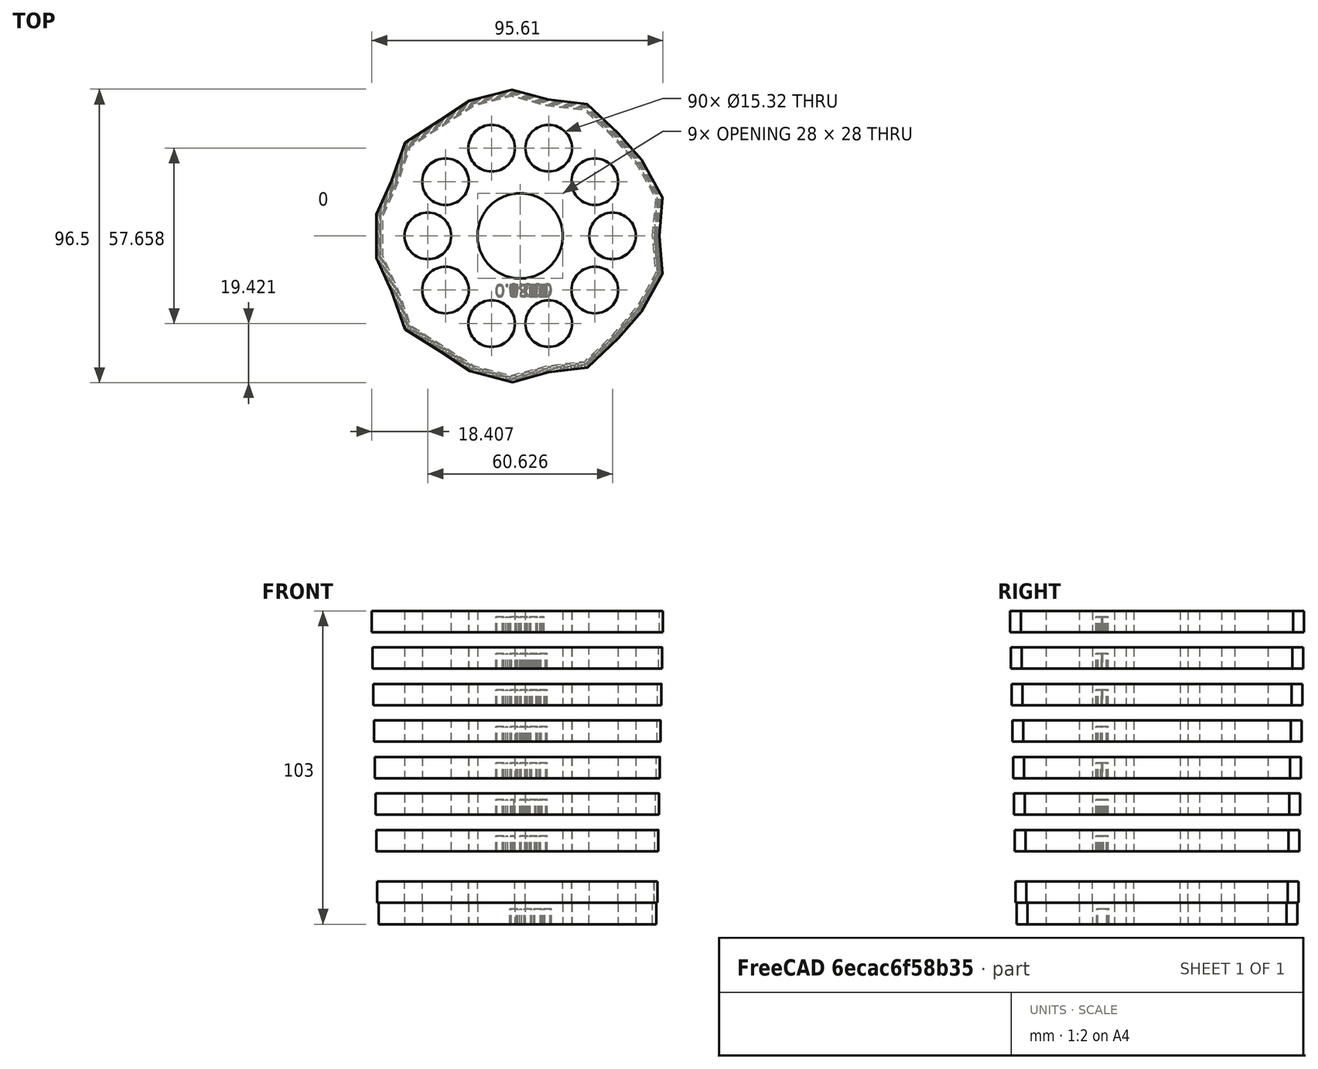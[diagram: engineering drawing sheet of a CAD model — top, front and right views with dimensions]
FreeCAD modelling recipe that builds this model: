
FCSTD DOCUMENT  (FreeCAD 1.0R39109 (Git))
Label: All gears
License: Creative Commons Attribution 4.0
LicenseURL: https://creativecommons.org/licenses/by/4.0/
objects: Sketcher::SketchObject×27, PartDesign::Pocket×17, PartDesign::Pad×9, PartDesign::PolarPattern×9, PartDesign::Body×9, Part::Part2DObjectPython×8
note: 167 computed .brp shape members not serialized (recipe doc carries the construction recipe); baked Part::Feature solids carry a one-line shape summary decoded from their .brp

FEATURE [Part::Part2DObjectPython] ShapeString  # Draft 2D object (typed FeaturePython)
  FontFile = <userpath>/Documents/DV_Projects/8_Cycloidal_gearbox_paper/0_Modelling_FILES/V 0_000/OpenSans-Regular.ttf
  Fuse = false
  Justification = 6
  JustificationReference = 0
  KeepLeftMargin = false
  MakeFace = true
  ObliqueAngle = 0
  Placement = pos=(-141.05,-92.68,0) rot=(-1,0,0;1.5708rad)
  ScaleToSize = true
  Size = 4
  String = 0
  Tracking = 0
FEATURE [Sketcher::SketchObject] Sketch  label="IF E Change001"
  ArcFitTolerance = 1e-06
  AttachmentSupport = -> [XZ_Plane]
  FullyConstrained = false
  MakeInternals = false
  MapMode = 5
  Placement = pos=(0,0,0) rot=(1,0,0;1.5708rad)
  sketch-geometry (7):
    g0: Circle CenterX=0 CenterY=0 CenterZ=0 NormalX=0 NormalY=0 NormalZ=1 AngleXU=0 Radius=14
    g1: Circle [constr] CenterX=0 CenterY=0 CenterZ=0 NormalX=0 NormalY=0 NormalZ=1 AngleXU=0 Radius=46.6255
    g2: LineSegment [constr] StartX=14 StartY=0 StartZ=0 EndX=46.6255 EndY=0 EndZ=0
    g3: GeomPoint [constr] X=30.3128 Y=0 Z=0
    g4: Circle [constr] CenterX=0 CenterY=0 CenterZ=0 NormalX=0 NormalY=0 NormalZ=1 AngleXU=0 Radius=30.3128
    g5: Circle CenterX=-30.3128 CenterY=0 CenterZ=0 NormalX=0 NormalY=0 NormalZ=1 AngleXU=0 Radius=7.66
    g6: Circle [constr] CenterX=-31.4728 CenterY=0 CenterZ=0 NormalX=0 NormalY=0 NormalZ=1 AngleXU=0 Radius=6.5
  constraints (20):
    c: Diameter(g0) = 28  'Dia Bearing'
    c: Coincident(g0,g-1)
    c: Coincident(g1,g0)
    c: PointOnObject(g2,g0)
    c: PointOnObject(g2,g1)
    c: PointOnObject(g2,g-1)
    c: PointOnObject(g2,g-1)
    c: Symmetric(g2,g2,g3)
    c: Coincident(g4,g0)
    c: PointOnObject(g3,g4)
    c: Diameter(g5) = 15.32  'DPinOut+E+2dc'
    c: Diameter(g1) = 93.251
    c: Block(g1)
    c: Block(g4)
    c: PointOnObject(g6,g-1)
    c: Diameter(g6) = 13
    c: Tangent(g5,g6)
    c: PointOnObject(g5,g4)
    c: DistanceX(g6,g5) = 1.16
    c: Diameter(g4) = 60.6255
FEATURE [Sketcher::SketchObject] USE_Macro_v6_gear_profile001
  ArcFitTolerance = 1e-06
  AttachmentSupport = -> [XZ_Plane]
  FullyConstrained = false
  MakeInternals = false
  MapMode = 5
  Placement = pos=(0,0,0) rot=(1,0,0;1.5708rad)
  sketch-geometry (1):
    g0: BSplineCurve PolesCount=3241 KnotsCount=3242 Degree=3 IsPeriodic=1
FEATURE [PartDesign::Pad] Pad  label="HERE"
  Direction = (0,-1,2e-16)
  Length = 7
  Length2 = 10
  Placement = pos=(0,0,0) rot=(1,0,0;1.5708rad)
  Profile = -> USE_Macro_v6_gear_profile001
  ReferenceAxis = -> USE_Macro_v6_gear_profile001 [N_Axis]
  Refine = true
  Suppressed = false
  Type = 0
FEATURE [PartDesign::Pocket] Pocket
  BaseFeature = -> Pad
  Direction = (0,1,-2e-16)
  Length = 5
  Length2 = 5
  Midplane = true
  Placement = pos=(0,0,0) rot=(1,0,0;1.5708rad)
  Profile = -> Sketch
  ReferenceAxis = -> Sketch [N_Axis]
  Refine = true
  Suppressed = false
  Type = 1
FEATURE [PartDesign::PolarPattern] PolarPattern
  Angle = 360
  Axis = -> Sketch [N_Axis]
  BaseFeature = -> Pocket
  Mode = 0
  Occurrences = 10
  Offset = 120
  Originals = -> [Pocket]
  Placement = pos=(0,0,0) rot=(1,0,0;1.5708rad)
  Refine = true
  Suppressed = false
  TransformMode = 0
FEATURE [Sketcher::SketchObject] Sketch037
  ArcFitTolerance = 1e-06
  AttachmentSupport = -> [PolarPattern]
  FullyConstrained = false
  MakeInternals = false
  MapMode = 5
  Placement = pos=(0,-7,0) rot=(1,0,0;1.5708rad)
  sketch-geometry (108):
    g0: BSplineCurve PolesCount=3 KnotsCount=2 Degree=2 IsPeriodic=0
    g1: BSplineCurve PolesCount=3 KnotsCount=2 Degree=2 IsPeriodic=0
    g2: BSplineCurve PolesCount=3 KnotsCount=2 Degree=2 IsPeriodic=0
    g3: BSplineCurve PolesCount=3 KnotsCount=2 Degree=2 IsPeriodic=0
    g4: BSplineCurve PolesCount=3 KnotsCount=2 Degree=2 IsPeriodic=0
    g5: BSplineCurve PolesCount=3 KnotsCount=2 Degree=2 IsPeriodic=0
    g6: BSplineCurve PolesCount=3 KnotsCount=2 Degree=2 IsPeriodic=0
    g7: BSplineCurve PolesCount=3 KnotsCount=2 Degree=2 IsPeriodic=0
    g8: BSplineCurve PolesCount=3 KnotsCount=2 Degree=2 IsPeriodic=0
    g9: BSplineCurve PolesCount=3 KnotsCount=2 Degree=2 IsPeriodic=0
    g10: BSplineCurve PolesCount=3 KnotsCount=2 Degree=2 IsPeriodic=0
    g11: BSplineCurve PolesCount=3 KnotsCount=2 Degree=2 IsPeriodic=0
    g12: BSplineCurve PolesCount=3 KnotsCount=2 Degree=2 IsPeriodic=0
    g13: BSplineCurve PolesCount=3 KnotsCount=2 Degree=2 IsPeriodic=0
    g14: BSplineCurve PolesCount=3 KnotsCount=2 Degree=2 IsPeriodic=0
    g15: BSplineCurve PolesCount=3 KnotsCount=2 Degree=2 IsPeriodic=0
    g16: BSplineCurve PolesCount=3 KnotsCount=2 Degree=2 IsPeriodic=0
    g17: BSplineCurve PolesCount=3 KnotsCount=2 Degree=2 IsPeriodic=0
    g18: BSplineCurve PolesCount=3 KnotsCount=2 Degree=2 IsPeriodic=0
    g19: BSplineCurve PolesCount=3 KnotsCount=2 Degree=2 IsPeriodic=0
    g20: BSplineCurve PolesCount=3 KnotsCount=2 Degree=2 IsPeriodic=0
    g21: BSplineCurve PolesCount=3 KnotsCount=2 Degree=2 IsPeriodic=0
    g22: BSplineCurve PolesCount=3 KnotsCount=2 Degree=2 IsPeriodic=0
    g23: BSplineCurve PolesCount=3 KnotsCount=2 Degree=2 IsPeriodic=0
    g24: BSplineCurve PolesCount=3 KnotsCount=2 Degree=2 IsPeriodic=0
    g25: BSplineCurve PolesCount=3 KnotsCount=2 Degree=2 IsPeriodic=0
    g26: BSplineCurve PolesCount=3 KnotsCount=2 Degree=2 IsPeriodic=0
    g27: BSplineCurve PolesCount=3 KnotsCount=2 Degree=2 IsPeriodic=0
    g28: BSplineCurve PolesCount=3 KnotsCount=2 Degree=2 IsPeriodic=0
    g29: BSplineCurve PolesCount=3 KnotsCount=2 Degree=2 IsPeriodic=0
    g30: BSplineCurve PolesCount=3 KnotsCount=2 Degree=2 IsPeriodic=0
    g31: BSplineCurve PolesCount=3 KnotsCount=2 Degree=2 IsPeriodic=0
    g32: BSplineCurve PolesCount=3 KnotsCount=2 Degree=2 IsPeriodic=0
    g33: BSplineCurve PolesCount=3 KnotsCount=2 Degree=2 IsPeriodic=0
    g34: BSplineCurve PolesCount=3 KnotsCount=2 Degree=2 IsPeriodic=0
    g35: BSplineCurve PolesCount=3 KnotsCount=2 Degree=2 IsPeriodic=0
    g36: BSplineCurve PolesCount=3 KnotsCount=2 Degree=2 IsPeriodic=0
    g37: BSplineCurve PolesCount=3 KnotsCount=2 Degree=2 IsPeriodic=0
    g38: BSplineCurve PolesCount=3 KnotsCount=2 Degree=2 IsPeriodic=0
    g39: BSplineCurve PolesCount=3 KnotsCount=2 Degree=2 IsPeriodic=0
    g40: BSplineCurve PolesCount=3 KnotsCount=2 Degree=2 IsPeriodic=0
    g41: BSplineCurve PolesCount=3 KnotsCount=2 Degree=2 IsPeriodic=0
    g42: BSplineCurve PolesCount=3 KnotsCount=2 Degree=2 IsPeriodic=0
    g43: BSplineCurve PolesCount=3 KnotsCount=2 Degree=2 IsPeriodic=0
    g44: BSplineCurve PolesCount=3 KnotsCount=2 Degree=2 IsPeriodic=0
    g45: BSplineCurve PolesCount=3 KnotsCount=2 Degree=2 IsPeriodic=0
    g46: BSplineCurve PolesCount=3 KnotsCount=2 Degree=2 IsPeriodic=0
    g47: BSplineCurve PolesCount=3 KnotsCount=2 Degree=2 IsPeriodic=0
    g48: BSplineCurve PolesCount=3 KnotsCount=2 Degree=2 IsPeriodic=0
    g49: BSplineCurve PolesCount=3 KnotsCount=2 Degree=2 IsPeriodic=0
    g50: BSplineCurve PolesCount=3 KnotsCount=2 Degree=2 IsPeriodic=0
    g51: BSplineCurve PolesCount=3 KnotsCount=2 Degree=2 IsPeriodic=0
    g52: BSplineCurve PolesCount=3 KnotsCount=2 Degree=2 IsPeriodic=0
    g53: BSplineCurve PolesCount=3 KnotsCount=2 Degree=2 IsPeriodic=0
    g54: BSplineCurve PolesCount=3 KnotsCount=2 Degree=2 IsPeriodic=0
    g55: BSplineCurve PolesCount=3 KnotsCount=2 Degree=2 IsPeriodic=0
    g56: BSplineCurve PolesCount=3 KnotsCount=2 Degree=2 IsPeriodic=0
    g57: BSplineCurve PolesCount=3 KnotsCount=2 Degree=2 IsPeriodic=0
    g58: BSplineCurve PolesCount=3 KnotsCount=2 Degree=2 IsPeriodic=0
    g59: BSplineCurve PolesCount=3 KnotsCount=2 Degree=2 IsPeriodic=0
    g60: BSplineCurve PolesCount=3 KnotsCount=2 Degree=2 IsPeriodic=0
    g61: BSplineCurve PolesCount=3 KnotsCount=2 Degree=2 IsPeriodic=0
    g62: BSplineCurve PolesCount=3 KnotsCount=2 Degree=2 IsPeriodic=0
    g63: BSplineCurve PolesCount=3 KnotsCount=2 Degree=2 IsPeriodic=0
    g64: BSplineCurve PolesCount=3 KnotsCount=2 Degree=2 IsPeriodic=0
    g65: BSplineCurve PolesCount=3 KnotsCount=2 Degree=2 IsPeriodic=0
    g66: BSplineCurve PolesCount=3 KnotsCount=2 Degree=2 IsPeriodic=0
    g67: BSplineCurve PolesCount=3 KnotsCount=2 Degree=2 IsPeriodic=0
    g68: BSplineCurve PolesCount=3 KnotsCount=2 Degree=2 IsPeriodic=0
    g69: BSplineCurve PolesCount=3 KnotsCount=2 Degree=2 IsPeriodic=0
    g70: BSplineCurve PolesCount=3 KnotsCount=2 Degree=2 IsPeriodic=0
    g71: BSplineCurve PolesCount=3 KnotsCount=2 Degree=2 IsPeriodic=0
    g72: BSplineCurve PolesCount=3 KnotsCount=2 Degree=2 IsPeriodic=0
    g73: BSplineCurve PolesCount=3 KnotsCount=2 Degree=2 IsPeriodic=0
    g74: BSplineCurve PolesCount=3 KnotsCount=2 Degree=2 IsPeriodic=0
    g75: BSplineCurve PolesCount=3 KnotsCount=2 Degree=2 IsPeriodic=0
    g76: BSplineCurve PolesCount=3 KnotsCount=2 Degree=2 IsPeriodic=0
    g77: BSplineCurve PolesCount=3 KnotsCount=2 Degree=2 IsPeriodic=0
    g78: BSplineCurve PolesCount=3 KnotsCount=2 Degree=2 IsPeriodic=0
    g79: BSplineCurve PolesCount=3 KnotsCount=2 Degree=2 IsPeriodic=0
    g80: BSplineCurve PolesCount=3 KnotsCount=2 Degree=2 IsPeriodic=0
    g81: BSplineCurve PolesCount=3 KnotsCount=2 Degree=2 IsPeriodic=0
    g82: BSplineCurve PolesCount=3 KnotsCount=2 Degree=2 IsPeriodic=0
    g83: BSplineCurve PolesCount=3 KnotsCount=2 Degree=2 IsPeriodic=0
    g84: BSplineCurve PolesCount=3 KnotsCount=2 Degree=2 IsPeriodic=0
    g85: BSplineCurve PolesCount=3 KnotsCount=2 Degree=2 IsPeriodic=0
    g86: BSplineCurve PolesCount=3 KnotsCount=2 Degree=2 IsPeriodic=0
    g87: BSplineCurve PolesCount=3 KnotsCount=2 Degree=2 IsPeriodic=0
    g88: BSplineCurve PolesCount=3 KnotsCount=2 Degree=2 IsPeriodic=0
    g89: BSplineCurve PolesCount=3 KnotsCount=2 Degree=2 IsPeriodic=0
    g90: BSplineCurve PolesCount=3 KnotsCount=2 Degree=2 IsPeriodic=0
    g91: BSplineCurve PolesCount=3 KnotsCount=2 Degree=2 IsPeriodic=0
    g92: BSplineCurve PolesCount=3 KnotsCount=2 Degree=2 IsPeriodic=0
    g93: BSplineCurve PolesCount=3 KnotsCount=2 Degree=2 IsPeriodic=0
    g94: BSplineCurve PolesCount=3 KnotsCount=2 Degree=2 IsPeriodic=0
    g95: BSplineCurve PolesCount=3 KnotsCount=2 Degree=2 IsPeriodic=0
    g96: BSplineCurve PolesCount=3 KnotsCount=2 Degree=2 IsPeriodic=0
    g97: BSplineCurve PolesCount=3 KnotsCount=2 Degree=2 IsPeriodic=0
    g98: BSplineCurve PolesCount=3 KnotsCount=2 Degree=2 IsPeriodic=0
    g99: BSplineCurve PolesCount=3 KnotsCount=2 Degree=2 IsPeriodic=0
    g100: BSplineCurve PolesCount=3 KnotsCount=2 Degree=2 IsPeriodic=0
    g101: BSplineCurve PolesCount=3 KnotsCount=2 Degree=2 IsPeriodic=0
    g102: BSplineCurve PolesCount=3 KnotsCount=2 Degree=2 IsPeriodic=0
    g103: BSplineCurve PolesCount=3 KnotsCount=2 Degree=2 IsPeriodic=0
    g104: BSplineCurve PolesCount=3 KnotsCount=2 Degree=2 IsPeriodic=0
    g105: BSplineCurve PolesCount=3 KnotsCount=2 Degree=2 IsPeriodic=0
    g106: BSplineCurve PolesCount=3 KnotsCount=2 Degree=2 IsPeriodic=0
    g107: BSplineCurve PolesCount=3 KnotsCount=2 Degree=2 IsPeriodic=0
  constraints (108):
    c: Coincident(g0,g1)
    c: Coincident(g1,g2)
    c: Coincident(g2,g3)
    c: Coincident(g3,g4)
    c: Coincident(g4,g5)
    c: Coincident(g5,g6)
    c: Coincident(g6,g7)
    c: Coincident(g7,g8)
    c: Coincident(g8,g9)
    c: Coincident(g9,g10)
    c: Coincident(g10,g11)
    c: Coincident(g11,g12)
    c: Coincident(g12,g0)
    c: Coincident(g13,g14)
    c: Coincident(g14,g15)
    c: Coincident(g15,g16)
    c: Coincident(g16,g17)
    c: Coincident(g17,g18)
    c: Coincident(g18,g19)
    c: Coincident(g19,g20)
    c: Coincident(g20,g21)
    c: Coincident(g21,g22)
    c: Coincident(g22,g23)
    c: Coincident(g23,g24)
    c: Coincident(g24,g13)
    c: Coincident(g25,g26)
    c: Coincident(g26,g27)
    c: Coincident(g27,g28)
    c: Coincident(g28,g29)
    c: Coincident(g29,g30)
    c: Coincident(g30,g31)
    c: Coincident(g31,g32)
    c: Coincident(g32,g25)
    c: Coincident(g33,g34)
    c: Coincident(g34,g35)
    c: Coincident(g35,g36)
    c: Coincident(g36,g37)
    c: Coincident(g37,g38)
    c: Coincident(g38,g39)
    c: Coincident(g39,g40)
    c: Coincident(g40,g41)
    c: Coincident(g41,g42)
    c: Coincident(g42,g43)
    c: Coincident(g43,g44)
    c: Coincident(g44,g45)
    c: Coincident(g45,g33)
    c: Coincident(g46,g47)
    c: Coincident(g47,g48)
    c: Coincident(g48,g49)
    c: Coincident(g49,g50)
    c: Coincident(g50,g51)
    c: Coincident(g51,g52)
    c: Coincident(g52,g53)
    c: Coincident(g53,g54)
    c: Coincident(g54,g55)
    c: Coincident(g55,g56)
    c: Coincident(g56,g57)
    c: Coincident(g57,g46)
    c: Coincident(g58,g59)
    c: Coincident(g59,g60)
    c: Coincident(g60,g61)
    c: Coincident(g61,g62)
    c: Coincident(g62,g63)
    c: Coincident(g63,g64)
    c: Coincident(g64,g65)
    c: Coincident(g65,g66)
    c: Coincident(g66,g67)
    c: Coincident(g67,g68)
    c: Coincident(g68,g69)
    c: Coincident(g69,g70)
    c: Coincident(g70,g58)
    c: Coincident(g71,g72)
    c: Coincident(g72,g73)
    c: Coincident(g73,g74)
    c: Coincident(g74,g75)
    c: Coincident(g75,g76)
    c: Coincident(g76,g77)
    c: Coincident(g77,g78)
    c: Coincident(g78,g79)
    c: Coincident(g79,g80)
    c: Coincident(g80,g81)
    c: Coincident(g81,g82)
    c: Coincident(g82,g71)
    c: Coincident(g83,g84)
    c: Coincident(g84,g85)
    c: Coincident(g85,g86)
    c: Coincident(g86,g87)
    c: Coincident(g87,g88)
    c: Coincident(g88,g89)
    c: Coincident(g89,g90)
    c: Coincident(g90,g91)
    c: Coincident(g91,g92)
    c: Coincident(g92,g93)
    c: Coincident(g93,g94)
    c: Coincident(g94,g95)
    c: Coincident(g95,g83)
    c: Coincident(g96,g97)
    c: Coincident(g97,g98)
    c: Coincident(g98,g99)
    c: Coincident(g99,g100)
    c: Coincident(g100,g101)
    c: Coincident(g101,g102)
    c: Coincident(g102,g103)
    c: Coincident(g103,g104)
    c: Coincident(g104,g105)
    c: Coincident(g105,g106)
    c: Coincident(g106,g107)
    c: Coincident(g107,g96)
FEATURE [PartDesign::Pocket] Pocket017
  BaseFeature = -> PolarPattern
  Direction = (0,1,-2e-16)
  Length = 5
  Length2 = 5
  Placement = pos=(0,0,0) rot=(1,0,0;1.5708rad)
  Profile = -> Sketch037
  ReferenceAxis = -> Sketch037 [N_Axis]
  Refine = true
  Suppressed = false
  Type = 0
FEATURE [PartDesign::Body] Body  label="Gear_0_0000"
  AllowCompound = false
  Group = -> [Sketch,USE_Macro_v6_gear_profile001,Pad,Pocket,PolarPattern,ShapeString,Sketch037,Pocket017]
  Origin = -> Origin
  Placement = pos=(0,-3,0) rot=(1,0,0;1.5708rad)
  Tip = -> Pocket017
FEATURE [Sketcher::SketchObject] Sketch038  label="IF E Change002"
  ArcFitTolerance = 1e-06
  AttachmentSupport = -> [XZ_Plane001]
  FullyConstrained = false
  MakeInternals = false
  MapMode = 5
  Placement = pos=(0,0,0) rot=(1,0,0;1.5708rad)
  sketch-geometry (7):
    g0: Circle CenterX=0 CenterY=0 CenterZ=0 NormalX=0 NormalY=0 NormalZ=1 AngleXU=0 Radius=14
    g1: Circle [constr] CenterX=0 CenterY=0 CenterZ=0 NormalX=0 NormalY=0 NormalZ=1 AngleXU=0 Radius=46.6255
    g2: LineSegment [constr] StartX=14 StartY=0 StartZ=0 EndX=46.6255 EndY=0 EndZ=0
    g3: GeomPoint [constr] X=30.3128 Y=0 Z=0
    g4: Circle [constr] CenterX=0 CenterY=0 CenterZ=0 NormalX=0 NormalY=0 NormalZ=1 AngleXU=0 Radius=30.3128
    g5: Circle CenterX=-30.3128 CenterY=0 CenterZ=0 NormalX=0 NormalY=0 NormalZ=1 AngleXU=0 Radius=7.66
    g6: Circle [constr] CenterX=-31.4728 CenterY=0 CenterZ=0 NormalX=0 NormalY=0 NormalZ=1 AngleXU=0 Radius=6.5
  constraints (20):
    c: Diameter(g0) = 28  'Dia Bearing'
    c: Coincident(g0,g-1)
    c: Coincident(g1,g0)
    c: PointOnObject(g2,g0)
    c: PointOnObject(g2,g1)
    c: PointOnObject(g2,g-1)
    c: PointOnObject(g2,g-1)
    c: Symmetric(g2,g2,g3)
    c: Coincident(g4,g0)
    c: PointOnObject(g3,g4)
    c: Diameter(g5) = 15.32  'DPinOut+E+2dc'
    c: Diameter(g1) = 93.251
    c: Block(g1)
    c: Block(g4)
    c: PointOnObject(g6,g-1)
    c: Diameter(g6) = 13
    c: Tangent(g5,g6)
    c: PointOnObject(g5,g4)
    c: DistanceX(g6,g5) = 1.16
    c: Diameter(g4) = 60.6255
FEATURE [Sketcher::SketchObject] USE_Macro_v6_gear_profile  label="USE_Macro_v6_gear_profile_N_6"
  ArcFitTolerance = 1e-06
  AttachmentSupport = -> [XZ_Plane001]
  FullyConstrained = false
  MakeInternals = false
  MapMode = 5
  Placement = pos=(0,0,0) rot=(1,0,0;1.5708rad)
  sketch-geometry (1):
    g0: BSplineCurve PolesCount=1801 KnotsCount=1801 Degree=3 IsPeriodic=1
FEATURE [Sketcher::SketchObject] USE_Macro_v6_gear_profile002
  ArcFitTolerance = 1e-06
  AttachmentSupport = -> [XZ_Plane001]
  FullyConstrained = false
  MakeInternals = false
  MapMode = 5
  Placement = pos=(0,0,0) rot=(1,0,0;1.5708rad)
  sketch-geometry (1):
    g0: BSplineCurve PolesCount=3241 KnotsCount=3241 Degree=3 IsPeriodic=1
FEATURE [PartDesign::Pad] Pad001
  Direction = (0,-1,2e-16)
  Length = 7
  Length2 = 10
  Placement = pos=(0,0,0) rot=(1,0,0;1.5708rad)
  Profile = -> USE_Macro_v6_gear_profile002
  ReferenceAxis = -> USE_Macro_v6_gear_profile002 [N_Axis]
  Refine = true
  Suppressed = false
  Type = 0
FEATURE [PartDesign::Pocket] Pocket018
  BaseFeature = -> Pad001
  Direction = (0,1,-2e-16)
  Length = 5
  Length2 = 5
  Midplane = true
  Placement = pos=(0,0,0) rot=(1,0,0;1.5708rad)
  Profile = -> Sketch038
  ReferenceAxis = -> Sketch038 [N_Axis]
  Refine = true
  Suppressed = false
  Type = 1
FEATURE [PartDesign::PolarPattern] PolarPattern001
  Angle = 360
  Axis = -> Sketch038 [N_Axis]
  BaseFeature = -> Pocket018
  Mode = 0
  Occurrences = 10
  Offset = 120
  Originals = -> [Pocket018]
  Placement = pos=(0,0,0) rot=(1,0,0;1.5708rad)
  Refine = true
  Suppressed = false
  TransformMode = 0
FEATURE [PartDesign::Body] Body001  label="Gear_0_083"
  AllowCompound = false
  Group = -> [USE_Macro_v6_gear_profile,Sketch038,USE_Macro_v6_gear_profile002,Pad001,Pocket018,PolarPattern001]
  Origin = -> Origin001
  Placement = pos=(0,-3,0) rot=(1,0,0;4.71239rad)
  Tip = -> PolarPattern001
FEATURE [Part::Part2DObjectPython] ShapeString001  # Draft 2D object (typed FeaturePython)
  FontFile = <userpath>/Documents/DV_Projects/8_Cycloidal_gearbox_paper/0_testbed/v0/V 0_1339/OpenSans-Regular.ttf
  Fuse = false
  Justification = 6
  JustificationReference = 0
  KeepLeftMargin = false
  MakeFace = true
  ObliqueAngle = 0
  Placement = pos=(-8,3.6e-15,-16) rot=(-1,0,0;1.5708rad)
  ScaleToSize = true
  Size = 4
  String = 0.1339
  Tracking = 0
FEATURE [Sketcher::SketchObject] Sketch039  label="IF E Change003"
  ArcFitTolerance = 1e-06
  AttachmentSupport = -> [XZ_Plane002]
  FullyConstrained = false
  MakeInternals = false
  MapMode = 5
  Placement = pos=(0,0,0) rot=(1,0,0;1.5708rad)
  sketch-geometry (7):
    g0: Circle CenterX=0 CenterY=0 CenterZ=0 NormalX=0 NormalY=0 NormalZ=1 AngleXU=0 Radius=14
    g1: Circle [constr] CenterX=0 CenterY=0 CenterZ=0 NormalX=0 NormalY=0 NormalZ=1 AngleXU=0 Radius=46.6255
    g2: LineSegment [constr] StartX=14 StartY=0 StartZ=0 EndX=46.6255 EndY=0 EndZ=0
    g3: GeomPoint [constr] X=30.3128 Y=0 Z=0
    g4: Circle [constr] CenterX=0 CenterY=0 CenterZ=0 NormalX=0 NormalY=0 NormalZ=1 AngleXU=0 Radius=30.3128
    g5: Circle CenterX=-30.3128 CenterY=0 CenterZ=0 NormalX=0 NormalY=0 NormalZ=1 AngleXU=0 Radius=7.66
    g6: Circle [constr] CenterX=-31.4728 CenterY=0 CenterZ=0 NormalX=0 NormalY=0 NormalZ=1 AngleXU=0 Radius=6.5
  constraints (20):
    c: Diameter(g0) = 28  'Dia Bearing'
    c: Coincident(g0,g-1)
    c: Coincident(g1,g0)
    c: PointOnObject(g2,g0)
    c: PointOnObject(g2,g1)
    c: PointOnObject(g2,g-1)
    c: PointOnObject(g2,g-1)
    c: Symmetric(g2,g2,g3)
    c: Coincident(g4,g0)
    c: PointOnObject(g3,g4)
    c: Diameter(g5) = 15.32  'DPinOut+E+2dc'
    c: Diameter(g1) = 93.251
    c: Block(g1)
    c: Block(g4)
    c: PointOnObject(g6,g-1)
    c: Diameter(g6) = 13
    c: Tangent(g5,g6)
    c: PointOnObject(g5,g4)
    c: DistanceX(g6,g5) = 1.16
    c: Diameter(g4) = 60.6255
FEATURE [Sketcher::SketchObject] USE_Macro_v6_gear_profile003
  ArcFitTolerance = 1e-06
  AttachmentSupport = -> [XZ_Plane002]
  FullyConstrained = false
  MakeInternals = false
  MapMode = 5
  Placement = pos=(0,0,0) rot=(1,0,0;1.5708rad)
  sketch-geometry (1):
    g0: BSplineCurve PolesCount=3241 KnotsCount=3242 Degree=3 IsPeriodic=1
FEATURE [PartDesign::Pad] Pad002
  Direction = (0,-1,2e-16)
  Length = 7
  Length2 = 10
  Placement = pos=(0,0,0) rot=(1,0,0;1.5708rad)
  Profile = -> USE_Macro_v6_gear_profile003
  ReferenceAxis = -> USE_Macro_v6_gear_profile003 [N_Axis]
  Refine = true
  Suppressed = false
  Type = 0
FEATURE [PartDesign::Pocket] Pocket019
  BaseFeature = -> Pad002
  Direction = (0,1,-2e-16)
  Length = 5
  Length2 = 5
  Midplane = true
  Placement = pos=(0,0,0) rot=(1,0,0;1.5708rad)
  Profile = -> Sketch039
  ReferenceAxis = -> Sketch039 [N_Axis]
  Refine = true
  Suppressed = false
  Type = 1
FEATURE [PartDesign::PolarPattern] PolarPattern002
  Angle = 360
  Axis = -> Sketch039 [N_Axis]
  BaseFeature = -> Pocket019
  Mode = 0
  Occurrences = 10
  Offset = 120
  Originals = -> [Pocket019]
  Placement = pos=(0,0,0) rot=(1,0,0;1.5708rad)
  Refine = true
  Suppressed = false
  TransformMode = 0
FEATURE [Sketcher::SketchObject] Sketch040
  ArcFitTolerance = 1e-06
  AttachmentSupport = -> [PolarPattern002]
  FullyConstrained = false
  MakeInternals = false
  MapMode = 5
  Placement = pos=(0,-7,0) rot=(1,0,0;1.5708rad)
  sketch-geometry (153):
    g0: BSplineCurve PolesCount=3 KnotsCount=2 Degree=2 IsPeriodic=0
    g1: BSplineCurve PolesCount=3 KnotsCount=2 Degree=2 IsPeriodic=0
    g2: BSplineCurve PolesCount=3 KnotsCount=2 Degree=2 IsPeriodic=0
    g3: BSplineCurve PolesCount=3 KnotsCount=2 Degree=2 IsPeriodic=0
    g4: BSplineCurve PolesCount=3 KnotsCount=2 Degree=2 IsPeriodic=0
    g5: BSplineCurve PolesCount=3 KnotsCount=2 Degree=2 IsPeriodic=0
    g6: BSplineCurve PolesCount=3 KnotsCount=2 Degree=2 IsPeriodic=0
    g7: BSplineCurve PolesCount=3 KnotsCount=2 Degree=2 IsPeriodic=0
    g8: BSplineCurve PolesCount=3 KnotsCount=2 Degree=2 IsPeriodic=0
    g9: BSplineCurve PolesCount=3 KnotsCount=2 Degree=2 IsPeriodic=0
    g10: BSplineCurve PolesCount=3 KnotsCount=2 Degree=2 IsPeriodic=0
    g11: BSplineCurve PolesCount=3 KnotsCount=2 Degree=2 IsPeriodic=0
    g12: BSplineCurve PolesCount=3 KnotsCount=2 Degree=2 IsPeriodic=0
    g13: BSplineCurve PolesCount=3 KnotsCount=2 Degree=2 IsPeriodic=0
    g14: BSplineCurve PolesCount=3 KnotsCount=2 Degree=2 IsPeriodic=0
    g15: BSplineCurve PolesCount=3 KnotsCount=2 Degree=2 IsPeriodic=0
    g16: BSplineCurve PolesCount=3 KnotsCount=2 Degree=2 IsPeriodic=0
    g17: BSplineCurve PolesCount=3 KnotsCount=2 Degree=2 IsPeriodic=0
    g18: BSplineCurve PolesCount=3 KnotsCount=2 Degree=2 IsPeriodic=0
    g19: BSplineCurve PolesCount=3 KnotsCount=2 Degree=2 IsPeriodic=0
    g20: BSplineCurve PolesCount=3 KnotsCount=2 Degree=2 IsPeriodic=0
    g21: BSplineCurve PolesCount=3 KnotsCount=2 Degree=2 IsPeriodic=0
    g22: BSplineCurve PolesCount=3 KnotsCount=2 Degree=2 IsPeriodic=0
    g23: BSplineCurve PolesCount=3 KnotsCount=2 Degree=2 IsPeriodic=0
    g24: BSplineCurve PolesCount=3 KnotsCount=2 Degree=2 IsPeriodic=0
    g25: BSplineCurve PolesCount=3 KnotsCount=2 Degree=2 IsPeriodic=0
    g26: BSplineCurve PolesCount=3 KnotsCount=2 Degree=2 IsPeriodic=0
    g27: BSplineCurve PolesCount=3 KnotsCount=2 Degree=2 IsPeriodic=0
    g28: BSplineCurve PolesCount=3 KnotsCount=2 Degree=2 IsPeriodic=0
    g29: BSplineCurve PolesCount=3 KnotsCount=2 Degree=2 IsPeriodic=0
    g30: BSplineCurve PolesCount=3 KnotsCount=2 Degree=2 IsPeriodic=0
    g31: BSplineCurve PolesCount=3 KnotsCount=2 Degree=2 IsPeriodic=0
    g32: BSplineCurve PolesCount=3 KnotsCount=2 Degree=2 IsPeriodic=0
    g33: LineSegment StartX=-1.6516 StartY=16 StartZ=0 EndX=-2.09439 EndY=16 EndZ=0
    g34: LineSegment StartX=-1.6516 StartY=20 StartZ=0 EndX=-1.6516 EndY=16 EndZ=0
    g35: LineSegment StartX=-2.02879 StartY=20 StartZ=0 EndX=-1.6516 EndY=20 EndZ=0
    g36: LineSegment StartX=-3.11115 StartY=19.166 StartZ=0 EndX=-2.02879 EndY=20 EndZ=0
    g37: LineSegment StartX=-2.87336 StartY=18.8571 StartZ=0 EndX=-3.11115 EndY=19.166 EndZ=0
    g38: LineSegment StartX=-2.41691 StartY=19.2236 StartZ=0 EndX=-2.87336 EndY=18.8571 EndZ=0
    g39: BSplineCurve PolesCount=3 KnotsCount=2 Degree=2 IsPeriodic=0
    g40: BSplineCurve PolesCount=3 KnotsCount=2 Degree=2 IsPeriodic=0
    g41: BSplineCurve PolesCount=3 KnotsCount=2 Degree=2 IsPeriodic=0
    g42: BSplineCurve PolesCount=3 KnotsCount=2 Degree=2 IsPeriodic=0
    g43: BSplineCurve PolesCount=3 KnotsCount=2 Degree=2 IsPeriodic=0
    g44: LineSegment StartX=-2.09439 StartY=16 StartZ=0 EndX=-2.09439 EndY=18.8349 EndZ=0
    g45: BSplineCurve PolesCount=3 KnotsCount=2 Degree=2 IsPeriodic=0
    g46: BSplineCurve PolesCount=3 KnotsCount=2 Degree=2 IsPeriodic=0
    g47: BSplineCurve PolesCount=3 KnotsCount=2 Degree=2 IsPeriodic=0
    g48: BSplineCurve PolesCount=3 KnotsCount=2 Degree=2 IsPeriodic=0
    g49: BSplineCurve PolesCount=3 KnotsCount=2 Degree=2 IsPeriodic=0
    g50: LineSegment StartX=0.0841838 StartY=19.3342 StartZ=0 EndX=-0.145408 EndY=19.6458 EndZ=0
    g51: BSplineCurve PolesCount=3 KnotsCount=2 Degree=2 IsPeriodic=0
    g52: BSplineCurve PolesCount=3 KnotsCount=2 Degree=2 IsPeriodic=0
    g53: BSplineCurve PolesCount=3 KnotsCount=2 Degree=2 IsPeriodic=0
    g54: BSplineCurve PolesCount=3 KnotsCount=2 Degree=2 IsPeriodic=0
    g55: BSplineCurve PolesCount=3 KnotsCount=2 Degree=2 IsPeriodic=0
    g56: BSplineCurve PolesCount=3 KnotsCount=2 Degree=2 IsPeriodic=0
    g57: BSplineCurve PolesCount=3 KnotsCount=2 Degree=2 IsPeriodic=0
    g58: BSplineCurve PolesCount=3 KnotsCount=2 Degree=2 IsPeriodic=0
    g59: LineSegment StartX=0.439504 StartY=18.254 StartZ=0 EndX=0.84129 EndY=18.254 EndZ=0
    g60: LineSegment StartX=0.439504 StartY=17.8659 StartZ=0 EndX=0.439504 EndY=18.254 EndZ=0
    g61: LineSegment StartX=0.838557 StartY=17.8659 StartZ=0 EndX=0.439504 EndY=17.8659 EndZ=0
    g62: BSplineCurve PolesCount=3 KnotsCount=2 Degree=2 IsPeriodic=0
    g63: BSplineCurve PolesCount=3 KnotsCount=2 Degree=2 IsPeriodic=0
    g64: BSplineCurve PolesCount=3 KnotsCount=2 Degree=2 IsPeriodic=0
    g65: BSplineCurve PolesCount=3 KnotsCount=2 Degree=2 IsPeriodic=0
    g66: BSplineCurve PolesCount=3 KnotsCount=2 Degree=2 IsPeriodic=0
    g67: BSplineCurve PolesCount=3 KnotsCount=2 Degree=2 IsPeriodic=0
    g68: BSplineCurve PolesCount=3 KnotsCount=2 Degree=2 IsPeriodic=0
    g69: LineSegment StartX=-0.170007 StartY=16.1574 StartZ=0 EndX=-0.170007 EndY=16.5838 EndZ=0
    g70: BSplineCurve PolesCount=3 KnotsCount=2 Degree=2 IsPeriodic=0
    g71: BSplineCurve PolesCount=3 KnotsCount=2 Degree=2 IsPeriodic=0
    g72: BSplineCurve PolesCount=3 KnotsCount=2 Degree=2 IsPeriodic=0
    g73: BSplineCurve PolesCount=3 KnotsCount=2 Degree=2 IsPeriodic=0
    g74: BSplineCurve PolesCount=3 KnotsCount=2 Degree=2 IsPeriodic=0
    g75: BSplineCurve PolesCount=3 KnotsCount=2 Degree=2 IsPeriodic=0
    g76: BSplineCurve PolesCount=3 KnotsCount=2 Degree=2 IsPeriodic=0
    g77: LineSegment StartX=1.49453 StartY=18.1009 StartZ=0 EndX=1.49453 EndY=18.0791 EndZ=0
    g78: BSplineCurve PolesCount=3 KnotsCount=2 Degree=2 IsPeriodic=0
    g79: BSplineCurve PolesCount=3 KnotsCount=2 Degree=2 IsPeriodic=0
    g80: BSplineCurve PolesCount=3 KnotsCount=2 Degree=2 IsPeriodic=0
    g81: BSplineCurve PolesCount=3 KnotsCount=2 Degree=2 IsPeriodic=0
    g82: BSplineCurve PolesCount=3 KnotsCount=2 Degree=2 IsPeriodic=0
    g83: BSplineCurve PolesCount=3 KnotsCount=2 Degree=2 IsPeriodic=0
    g84: BSplineCurve PolesCount=3 KnotsCount=2 Degree=2 IsPeriodic=0
    g85: LineSegment StartX=3.27952 StartY=19.3342 StartZ=0 EndX=3.04993 EndY=19.6458 EndZ=0
    g86: BSplineCurve PolesCount=3 KnotsCount=2 Degree=2 IsPeriodic=0
    g87: BSplineCurve PolesCount=3 KnotsCount=2 Degree=2 IsPeriodic=0
    g88: BSplineCurve PolesCount=3 KnotsCount=2 Degree=2 IsPeriodic=0
    g89: BSplineCurve PolesCount=3 KnotsCount=2 Degree=2 IsPeriodic=0
    g90: BSplineCurve PolesCount=3 KnotsCount=2 Degree=2 IsPeriodic=0
    g91: BSplineCurve PolesCount=3 KnotsCount=2 Degree=2 IsPeriodic=0
    g92: BSplineCurve PolesCount=3 KnotsCount=2 Degree=2 IsPeriodic=0
    g93: BSplineCurve PolesCount=3 KnotsCount=2 Degree=2 IsPeriodic=0
    g94: LineSegment StartX=3.63484 StartY=18.254 StartZ=0 EndX=4.03663 EndY=18.254 EndZ=0
    g95: LineSegment StartX=3.63484 StartY=17.8659 StartZ=0 EndX=3.63484 EndY=18.254 EndZ=0
    g96: LineSegment StartX=4.03389 StartY=17.8659 StartZ=0 EndX=3.63484 EndY=17.8659 EndZ=0
    g97: BSplineCurve PolesCount=3 KnotsCount=2 Degree=2 IsPeriodic=0
    g98: BSplineCurve PolesCount=3 KnotsCount=2 Degree=2 IsPeriodic=0
    g99: BSplineCurve PolesCount=3 KnotsCount=2 Degree=2 IsPeriodic=0
    g100: BSplineCurve PolesCount=3 KnotsCount=2 Degree=2 IsPeriodic=0
    g101: BSplineCurve PolesCount=3 KnotsCount=2 Degree=2 IsPeriodic=0
    g102: BSplineCurve PolesCount=3 KnotsCount=2 Degree=2 IsPeriodic=0
    g103: BSplineCurve PolesCount=3 KnotsCount=2 Degree=2 IsPeriodic=0
    g104: LineSegment StartX=3.02533 StartY=16.1574 StartZ=0 EndX=3.02533 EndY=16.5838 EndZ=0
    g105: BSplineCurve PolesCount=3 KnotsCount=2 Degree=2 IsPeriodic=0
    g106: BSplineCurve PolesCount=3 KnotsCount=2 Degree=2 IsPeriodic=0
    g107: BSplineCurve PolesCount=3 KnotsCount=2 Degree=2 IsPeriodic=0
    g108: BSplineCurve PolesCount=3 KnotsCount=2 Degree=2 IsPeriodic=0
    g109: BSplineCurve PolesCount=3 KnotsCount=2 Degree=2 IsPeriodic=0
    g110: BSplineCurve PolesCount=3 KnotsCount=2 Degree=2 IsPeriodic=0
    g111: BSplineCurve PolesCount=3 KnotsCount=2 Degree=2 IsPeriodic=0
    g112: LineSegment StartX=4.68987 StartY=18.1009 StartZ=0 EndX=4.68987 EndY=18.0791 EndZ=0
    g113: BSplineCurve PolesCount=3 KnotsCount=2 Degree=2 IsPeriodic=0
    g114: BSplineCurve PolesCount=3 KnotsCount=2 Degree=2 IsPeriodic=0
    g115: BSplineCurve PolesCount=3 KnotsCount=2 Degree=2 IsPeriodic=0
    g116: BSplineCurve PolesCount=3 KnotsCount=2 Degree=2 IsPeriodic=0
    g117: BSplineCurve PolesCount=3 KnotsCount=2 Degree=2 IsPeriodic=0
    g118: BSplineCurve PolesCount=3 KnotsCount=2 Degree=2 IsPeriodic=0
    g119: BSplineCurve PolesCount=3 KnotsCount=2 Degree=2 IsPeriodic=0
    g120: BSplineCurve PolesCount=3 KnotsCount=2 Degree=2 IsPeriodic=0
    g121: BSplineCurve PolesCount=3 KnotsCount=2 Degree=2 IsPeriodic=0
    g122: BSplineCurve PolesCount=3 KnotsCount=2 Degree=2 IsPeriodic=0
    g123: BSplineCurve PolesCount=3 KnotsCount=2 Degree=2 IsPeriodic=0
    g124: BSplineCurve PolesCount=3 KnotsCount=2 Degree=2 IsPeriodic=0
    g125: BSplineCurve PolesCount=3 KnotsCount=2 Degree=2 IsPeriodic=0
    g126: BSplineCurve PolesCount=3 KnotsCount=2 Degree=2 IsPeriodic=0
    g127: BSplineCurve PolesCount=3 KnotsCount=2 Degree=2 IsPeriodic=0
    g128: BSplineCurve PolesCount=3 KnotsCount=2 Degree=2 IsPeriodic=0
    g129: LineSegment StartX=8.40999 StartY=17.9909 StartZ=0 EndX=8.37719 EndY=17.9909 EndZ=0
    g130: BSplineCurve PolesCount=3 KnotsCount=2 Degree=2 IsPeriodic=0
    g131: BSplineCurve PolesCount=3 KnotsCount=2 Degree=2 IsPeriodic=0
    g132: BSplineCurve PolesCount=3 KnotsCount=2 Degree=2 IsPeriodic=0
    g133: BSplineCurve PolesCount=3 KnotsCount=2 Degree=2 IsPeriodic=0
    g134: BSplineCurve PolesCount=3 KnotsCount=2 Degree=2 IsPeriodic=0
    g135: LineSegment StartX=6.53499 StartY=15.9962 StartZ=0 EndX=6.53499 EndY=16.3898 EndZ=0
    g136: BSplineCurve PolesCount=3 KnotsCount=2 Degree=2 IsPeriodic=0
    g137: BSplineCurve PolesCount=3 KnotsCount=2 Degree=2 IsPeriodic=0
    g138: BSplineCurve PolesCount=3 KnotsCount=2 Degree=2 IsPeriodic=0
    g139: BSplineCurve PolesCount=3 KnotsCount=2 Degree=2 IsPeriodic=0
    g140: BSplineCurve PolesCount=3 KnotsCount=2 Degree=2 IsPeriodic=0
    g141: BSplineCurve PolesCount=3 KnotsCount=2 Degree=2 IsPeriodic=0
    g142: BSplineCurve PolesCount=3 KnotsCount=2 Degree=2 IsPeriodic=0
    g143: BSplineCurve PolesCount=3 KnotsCount=2 Degree=2 IsPeriodic=0
    g144: BSplineCurve PolesCount=3 KnotsCount=2 Degree=2 IsPeriodic=0
    g145: BSplineCurve PolesCount=3 KnotsCount=2 Degree=2 IsPeriodic=0
    g146: BSplineCurve PolesCount=3 KnotsCount=2 Degree=2 IsPeriodic=0
    g147: BSplineCurve PolesCount=3 KnotsCount=2 Degree=2 IsPeriodic=0
    g148: BSplineCurve PolesCount=3 KnotsCount=2 Degree=2 IsPeriodic=0
    g149: BSplineCurve PolesCount=3 KnotsCount=2 Degree=2 IsPeriodic=0
    g150: BSplineCurve PolesCount=3 KnotsCount=2 Degree=2 IsPeriodic=0
    g151: BSplineCurve PolesCount=3 KnotsCount=2 Degree=2 IsPeriodic=0
    g152: BSplineCurve PolesCount=3 KnotsCount=2 Degree=2 IsPeriodic=0
  constraints (169):
    c: Coincident(g0,g1)
    c: Coincident(g1,g2)
    c: Coincident(g2,g3)
    c: Coincident(g3,g4)
    c: Coincident(g4,g5)
    c: Coincident(g5,g6)
    c: Coincident(g6,g7)
    c: Coincident(g7,g8)
    c: Coincident(g8,g9)
    c: Coincident(g9,g10)
    c: Coincident(g10,g11)
    c: Coincident(g11,g12)
    c: Coincident(g12,g0)
    c: Coincident(g13,g14)
    c: Coincident(g14,g15)
    c: Coincident(g15,g16)
    c: Coincident(g16,g17)
    c: Coincident(g17,g18)
    c: Coincident(g18,g19)
    c: Coincident(g19,g20)
    c: Coincident(g20,g21)
    c: Coincident(g21,g22)
    c: Coincident(g22,g23)
    c: Coincident(g23,g24)
    c: Coincident(g24,g13)
    c: Coincident(g25,g26)
    c: Coincident(g26,g27)
    c: Coincident(g27,g28)
    c: Coincident(g28,g29)
    c: Coincident(g29,g30)
    c: Coincident(g30,g31)
    c: Coincident(g31,g32)
    c: Coincident(g32,g25)
    c: Horizontal(g33)
    c: Coincident(g33,g34)
    c: Vertical(g34)
    c: Coincident(g34,g35)
    c: Horizontal(g35)
    c: Coincident(g35,g36)
    c: Coincident(g36,g37)
    c: Coincident(g37,g38)
    c: Coincident(g38,g39)
    c: Coincident(g39,g40)
    c: Coincident(g40,g41)
    c: Coincident(g41,g42)
    c: Coincident(g42,g43)
    c: Coincident(g43,g44)
    c: Vertical(g44)
    c: Coincident(g44,g33)
    c: Coincident(g45,g46)
    c: Coincident(g46,g47)
    c: Coincident(g47,g48)
    c: Coincident(g48,g49)
    c: Coincident(g49,g50)
    c: Coincident(g50,g51)
    c: Coincident(g51,g52)
    c: Coincident(g52,g53)
    c: Coincident(g53,g54)
    c: Coincident(g54,g55)
    c: Coincident(g55,g56)
    c: Coincident(g56,g57)
    c: Coincident(g57,g58)
    c: Coincident(g58,g59)
    c: Horizontal(g59)
    c: Coincident(g59,g60)
    c: Vertical(g60)
    c: Coincident(g60,g61)
    c: Horizontal(g61)
    c: Coincident(g61,g62)
    c: Coincident(g62,g63)
    c: Coincident(g63,g64)
    c: Coincident(g64,g65)
    c: Coincident(g65,g66)
    c: Coincident(g66,g67)
    c: Coincident(g67,g68)
    c: Coincident(g68,g69)
    c: Vertical(g69)
    c: Coincident(g69,g70)
    c: Coincident(g70,g71)
    c: Coincident(g71,g72)
    c: Coincident(g72,g73)
    c: Coincident(g73,g74)
    c: Coincident(g74,g75)
    c: Coincident(g75,g76)
    c: Coincident(g76,g77)
    c: Vertical(g77)
    c: Coincident(g77,g78)
    c: Coincident(g78,g79)
    c: Coincident(g79,g45)
    c: Coincident(g80,g81)
    c: Coincident(g81,g82)
    c: Coincident(g82,g83)
    c: Coincident(g83,g84)
    c: Coincident(g84,g85)
    c: Coincident(g85,g86)
    c: Coincident(g86,g87)
    c: Coincident(g87,g88)
    c: Coincident(g88,g89)
    c: Coincident(g89,g90)
    c: Coincident(g90,g91)
    c: Coincident(g91,g92)
    c: Coincident(g92,g93)
    c: Coincident(g93,g94)
    c: Horizontal(g94)
    c: Coincident(g94,g95)
    c: Vertical(g95)
    c: Coincident(g95,g96)
    c: Horizontal(g96)
    c: Coincident(g96,g97)
    c: Coincident(g97,g98)
    c: Coincident(g98,g99)
    c: Coincident(g99,g100)
    c: Coincident(g100,g101)
    c: Coincident(g101,g102)
    c: Coincident(g102,g103)
    c: Coincident(g103,g104)
    c: Vertical(g104)
    c: Coincident(g104,g105)
    c: Coincident(g105,g106)
    c: Coincident(g106,g107)
    c: Coincident(g107,g108)
    c: Coincident(g108,g109)
    c: Coincident(g109,g110)
    c: Coincident(g110,g111)
    c: Coincident(g111,g112)
    c: Vertical(g112)
    c: Coincident(g112,g113)
    c: Coincident(g113,g114)
    c: Coincident(g114,g80)
    c: Coincident(g115,g116)
    c: Coincident(g116,g117)
    c: Coincident(g117,g118)
    c: Coincident(g118,g119)
    c: Coincident(g119,g120)
    c: Coincident(g120,g121)
    c: Coincident(g121,g122)
    c: Coincident(g122,g123)
    c: Coincident(g123,g124)
    c: Coincident(g124,g125)
    c: Coincident(g125,g126)
    c: Coincident(g126,g127)
    c: Coincident(g127,g128)
    c: Coincident(g128,g129)
    c: Horizontal(g129)
    c: Coincident(g129,g130)
    c: Coincident(g130,g131)
    c: Coincident(g131,g132)
    c: Coincident(g132,g133)
    c: Coincident(g133,g134)
    c: Coincident(g134,g135)
    c: Vertical(g135)
    c: Coincident(g135,g136)
    c: Coincident(g136,g137)
    c: Coincident(g137,g138)
    c: Coincident(g138,g139)
    c: Coincident(g139,g140)
    c: Coincident(g140,g141)
    c: Coincident(g141,g115)
    c: Coincident(g142,g143)
    c: Coincident(g143,g144)
    c: Coincident(g144,g145)
    c: Coincident(g145,g146)
    c: Coincident(g146,g147)
    c: Coincident(g147,g148)
    c: Coincident(g148,g149)
    c: Coincident(g149,g150)
    c: Coincident(g150,g151)
    c: Coincident(g151,g152)
    c: Coincident(g152,g142)
FEATURE [PartDesign::Pocket] Pocket020
  BaseFeature = -> PolarPattern002
  Direction = (0,1,-2e-16)
  Length = 5
  Length2 = 5
  Placement = pos=(0,0,0) rot=(1,0,0;1.5708rad)
  Profile = -> Sketch040
  ReferenceAxis = -> Sketch040 [N_Axis]
  Refine = true
  Suppressed = false
  Type = 0
FEATURE [PartDesign::Body] Body002  label="Gear_0_1339"
  AllowCompound = false
  Group = -> [Sketch039,USE_Macro_v6_gear_profile003,Pad002,Pocket019,PolarPattern002,ShapeString001,Sketch040,Pocket020]
  Origin = -> Origin002
  Placement = pos=(0,-3,24) rot=(1,0,0;1.5708rad)
  Tip = -> Pocket020
FEATURE [Part::Part2DObjectPython] ShapeString002  # Draft 2D object (typed FeaturePython)
  FontFile = <userpath>/Documents/DV_Projects/8_Cycloidal_gearbox_paper/0_testbed/v0/V 0_1339/OpenSans-Regular.ttf
  Fuse = false
  Justification = 6
  JustificationReference = 0
  KeepLeftMargin = false
  MakeFace = true
  ObliqueAngle = 0
  Placement = pos=(-8,0,-16) rot=(-1,0,0;1.5708rad)
  ScaleToSize = true
  Size = 4
  String = 0.1847
  Tracking = 0
FEATURE [Sketcher::SketchObject] Sketch041  label="IF E Change004"
  ArcFitTolerance = 1e-06
  AttachmentSupport = -> [XZ_Plane003]
  FullyConstrained = false
  MakeInternals = false
  MapMode = 5
  Placement = pos=(0,0,0) rot=(1,0,0;1.5708rad)
  sketch-geometry (7):
    g0: Circle CenterX=0 CenterY=0 CenterZ=0 NormalX=0 NormalY=0 NormalZ=1 AngleXU=0 Radius=14
    g1: Circle [constr] CenterX=0 CenterY=0 CenterZ=0 NormalX=0 NormalY=0 NormalZ=1 AngleXU=0 Radius=46.6255
    g2: LineSegment [constr] StartX=14 StartY=0 StartZ=0 EndX=46.6255 EndY=0 EndZ=0
    g3: GeomPoint [constr] X=30.3128 Y=0 Z=0
    g4: Circle [constr] CenterX=0 CenterY=0 CenterZ=0 NormalX=0 NormalY=0 NormalZ=1 AngleXU=0 Radius=30.3128
    g5: Circle CenterX=-30.3128 CenterY=0 CenterZ=0 NormalX=0 NormalY=0 NormalZ=1 AngleXU=0 Radius=7.66
    g6: Circle [constr] CenterX=-31.4728 CenterY=0 CenterZ=0 NormalX=0 NormalY=0 NormalZ=1 AngleXU=0 Radius=6.5
  constraints (20):
    c: Diameter(g0) = 28  'Dia Bearing'
    c: Coincident(g0,g-1)
    c: Coincident(g1,g0)
    c: PointOnObject(g2,g0)
    c: PointOnObject(g2,g1)
    c: PointOnObject(g2,g-1)
    c: PointOnObject(g2,g-1)
    c: Symmetric(g2,g2,g3)
    c: Coincident(g4,g0)
    c: PointOnObject(g3,g4)
    c: Diameter(g5) = 15.32  'DPinOut+E+2dc'
    c: Diameter(g1) = 93.251
    c: Block(g1)
    c: Block(g4)
    c: PointOnObject(g6,g-1)
    c: Diameter(g6) = 13
    c: Tangent(g5,g6)
    c: PointOnObject(g5,g4)
    c: DistanceX(g6,g5) = 1.16
    c: Diameter(g4) = 60.6255
FEATURE [Sketcher::SketchObject] USE_Macro_v6_gear_profile004
  ArcFitTolerance = 1e-06
  AttachmentSupport = -> [XZ_Plane003]
  FullyConstrained = false
  MakeInternals = false
  MapMode = 5
  Placement = pos=(0,0,0) rot=(1,0,0;1.5708rad)
  sketch-geometry (1):
    g0: BSplineCurve PolesCount=3241 KnotsCount=3242 Degree=3 IsPeriodic=1
FEATURE [PartDesign::Pad] Pad003
  Direction = (0,-1,2e-16)
  Length = 7
  Length2 = 10
  Placement = pos=(0,0,0) rot=(1,0,0;1.5708rad)
  Profile = -> USE_Macro_v6_gear_profile004
  ReferenceAxis = -> USE_Macro_v6_gear_profile004 [N_Axis]
  Refine = true
  Suppressed = false
  Type = 0
FEATURE [PartDesign::Pocket] Pocket021
  BaseFeature = -> Pad003
  Direction = (0,1,-2e-16)
  Length = 5
  Length2 = 5
  Midplane = true
  Placement = pos=(0,0,0) rot=(1,0,0;1.5708rad)
  Profile = -> Sketch041
  ReferenceAxis = -> Sketch041 [N_Axis]
  Refine = true
  Suppressed = false
  Type = 1
FEATURE [PartDesign::PolarPattern] PolarPattern003
  Angle = 360
  Axis = -> Sketch041 [N_Axis]
  BaseFeature = -> Pocket021
  Mode = 0
  Occurrences = 10
  Offset = 120
  Originals = -> [Pocket021]
  Placement = pos=(0,0,0) rot=(1,0,0;1.5708rad)
  Refine = true
  Suppressed = false
  TransformMode = 0
FEATURE [Sketcher::SketchObject] Sketch042
  ArcFitTolerance = 1e-06
  AttachmentSupport = -> [PolarPattern003]
  FullyConstrained = false
  MakeInternals = false
  MapMode = 5
  Placement = pos=(0,-7,0) rot=(1,0,0;1.5708rad)
  sketch-geometry (118):
    g0: BSplineCurve PolesCount=3 KnotsCount=2 Degree=2 IsPeriodic=0
    g1: BSplineCurve PolesCount=3 KnotsCount=2 Degree=2 IsPeriodic=0
    g2: BSplineCurve PolesCount=3 KnotsCount=2 Degree=2 IsPeriodic=0
    g3: BSplineCurve PolesCount=3 KnotsCount=2 Degree=2 IsPeriodic=0
    g4: BSplineCurve PolesCount=3 KnotsCount=2 Degree=2 IsPeriodic=0
    g5: BSplineCurve PolesCount=3 KnotsCount=2 Degree=2 IsPeriodic=0
    g6: BSplineCurve PolesCount=3 KnotsCount=2 Degree=2 IsPeriodic=0
    g7: BSplineCurve PolesCount=3 KnotsCount=2 Degree=2 IsPeriodic=0
    g8: BSplineCurve PolesCount=3 KnotsCount=2 Degree=2 IsPeriodic=0
    g9: BSplineCurve PolesCount=3 KnotsCount=2 Degree=2 IsPeriodic=0
    g10: BSplineCurve PolesCount=3 KnotsCount=2 Degree=2 IsPeriodic=0
    g11: BSplineCurve PolesCount=3 KnotsCount=2 Degree=2 IsPeriodic=0
    g12: BSplineCurve PolesCount=3 KnotsCount=2 Degree=2 IsPeriodic=0
    g13: BSplineCurve PolesCount=3 KnotsCount=2 Degree=2 IsPeriodic=0
    g14: BSplineCurve PolesCount=3 KnotsCount=2 Degree=2 IsPeriodic=0
    g15: BSplineCurve PolesCount=3 KnotsCount=2 Degree=2 IsPeriodic=0
    g16: BSplineCurve PolesCount=3 KnotsCount=2 Degree=2 IsPeriodic=0
    g17: BSplineCurve PolesCount=3 KnotsCount=2 Degree=2 IsPeriodic=0
    g18: BSplineCurve PolesCount=3 KnotsCount=2 Degree=2 IsPeriodic=0
    g19: BSplineCurve PolesCount=3 KnotsCount=2 Degree=2 IsPeriodic=0
    g20: BSplineCurve PolesCount=3 KnotsCount=2 Degree=2 IsPeriodic=0
    g21: BSplineCurve PolesCount=3 KnotsCount=2 Degree=2 IsPeriodic=0
    g22: BSplineCurve PolesCount=3 KnotsCount=2 Degree=2 IsPeriodic=0
    g23: BSplineCurve PolesCount=3 KnotsCount=2 Degree=2 IsPeriodic=0
    g24: BSplineCurve PolesCount=3 KnotsCount=2 Degree=2 IsPeriodic=0
    g25: BSplineCurve PolesCount=3 KnotsCount=2 Degree=2 IsPeriodic=0
    g26: BSplineCurve PolesCount=3 KnotsCount=2 Degree=2 IsPeriodic=0
    g27: BSplineCurve PolesCount=3 KnotsCount=2 Degree=2 IsPeriodic=0
    g28: BSplineCurve PolesCount=3 KnotsCount=2 Degree=2 IsPeriodic=0
    g29: BSplineCurve PolesCount=3 KnotsCount=2 Degree=2 IsPeriodic=0
    g30: BSplineCurve PolesCount=3 KnotsCount=2 Degree=2 IsPeriodic=0
    g31: BSplineCurve PolesCount=3 KnotsCount=2 Degree=2 IsPeriodic=0
    g32: BSplineCurve PolesCount=3 KnotsCount=2 Degree=2 IsPeriodic=0
    g33: LineSegment StartX=-1.6516 StartY=16 StartZ=0 EndX=-2.09439 EndY=16 EndZ=0
    g34: LineSegment StartX=-1.6516 StartY=20 StartZ=0 EndX=-1.6516 EndY=16 EndZ=0
    g35: LineSegment StartX=-2.02879 StartY=20 StartZ=0 EndX=-1.6516 EndY=20 EndZ=0
    g36: LineSegment StartX=-3.11115 StartY=19.166 StartZ=0 EndX=-2.02879 EndY=20 EndZ=0
    g37: LineSegment StartX=-2.87336 StartY=18.8571 StartZ=0 EndX=-3.11115 EndY=19.166 EndZ=0
    g38: LineSegment StartX=-2.41691 StartY=19.2236 StartZ=0 EndX=-2.87336 EndY=18.8571 EndZ=0
    g39: BSplineCurve PolesCount=3 KnotsCount=2 Degree=2 IsPeriodic=0
    g40: BSplineCurve PolesCount=3 KnotsCount=2 Degree=2 IsPeriodic=0
    g41: BSplineCurve PolesCount=3 KnotsCount=2 Degree=2 IsPeriodic=0
    g42: BSplineCurve PolesCount=3 KnotsCount=2 Degree=2 IsPeriodic=0
    g43: BSplineCurve PolesCount=3 KnotsCount=2 Degree=2 IsPeriodic=0
    g44: LineSegment StartX=-2.09439 StartY=16 StartZ=0 EndX=-2.09439 EndY=18.8349 EndZ=0
    g45: BSplineCurve PolesCount=3 KnotsCount=2 Degree=2 IsPeriodic=0
    g46: BSplineCurve PolesCount=3 KnotsCount=2 Degree=2 IsPeriodic=0
    g47: BSplineCurve PolesCount=3 KnotsCount=2 Degree=2 IsPeriodic=0
    g48: BSplineCurve PolesCount=3 KnotsCount=2 Degree=2 IsPeriodic=0
    g49: BSplineCurve PolesCount=3 KnotsCount=2 Degree=2 IsPeriodic=0
    g50: BSplineCurve PolesCount=3 KnotsCount=2 Degree=2 IsPeriodic=0
    g51: BSplineCurve PolesCount=3 KnotsCount=2 Degree=2 IsPeriodic=0
    g52: BSplineCurve PolesCount=3 KnotsCount=2 Degree=2 IsPeriodic=0
    g53: BSplineCurve PolesCount=3 KnotsCount=2 Degree=2 IsPeriodic=0
    g54: BSplineCurve PolesCount=3 KnotsCount=2 Degree=2 IsPeriodic=0
    g55: BSplineCurve PolesCount=3 KnotsCount=2 Degree=2 IsPeriodic=0
    g56: BSplineCurve PolesCount=3 KnotsCount=2 Degree=2 IsPeriodic=0
    g57: BSplineCurve PolesCount=3 KnotsCount=2 Degree=2 IsPeriodic=0
    g58: BSplineCurve PolesCount=3 KnotsCount=2 Degree=2 IsPeriodic=0
    g59: BSplineCurve PolesCount=3 KnotsCount=2 Degree=2 IsPeriodic=0
    g60: BSplineCurve PolesCount=3 KnotsCount=2 Degree=2 IsPeriodic=0
    g61: BSplineCurve PolesCount=3 KnotsCount=2 Degree=2 IsPeriodic=0
    g62: BSplineCurve PolesCount=3 KnotsCount=2 Degree=2 IsPeriodic=0
    g63: BSplineCurve PolesCount=3 KnotsCount=2 Degree=2 IsPeriodic=0
    g64: BSplineCurve PolesCount=3 KnotsCount=2 Degree=2 IsPeriodic=0
    g65: BSplineCurve PolesCount=3 KnotsCount=2 Degree=2 IsPeriodic=0
    g66: BSplineCurve PolesCount=3 KnotsCount=2 Degree=2 IsPeriodic=0
    g67: BSplineCurve PolesCount=3 KnotsCount=2 Degree=2 IsPeriodic=0
    g68: BSplineCurve PolesCount=3 KnotsCount=2 Degree=2 IsPeriodic=0
    g69: BSplineCurve PolesCount=3 KnotsCount=2 Degree=2 IsPeriodic=0
    g70: BSplineCurve PolesCount=3 KnotsCount=2 Degree=2 IsPeriodic=0
    g71: BSplineCurve PolesCount=3 KnotsCount=2 Degree=2 IsPeriodic=0
    g72: BSplineCurve PolesCount=3 KnotsCount=2 Degree=2 IsPeriodic=0
    g73: LineSegment StartX=1.19388 StartY=17.8697 StartZ=0 EndX=1.09548 EndY=17.9054 EndZ=0
    g74: BSplineCurve PolesCount=3 KnotsCount=2 Degree=2 IsPeriodic=0
    g75: BSplineCurve PolesCount=3 KnotsCount=2 Degree=2 IsPeriodic=0
    g76: BSplineCurve PolesCount=3 KnotsCount=2 Degree=2 IsPeriodic=0
    g77: BSplineCurve PolesCount=3 KnotsCount=2 Degree=2 IsPeriodic=0
    g78: BSplineCurve PolesCount=3 KnotsCount=2 Degree=2 IsPeriodic=0
    g79: BSplineCurve PolesCount=3 KnotsCount=2 Degree=2 IsPeriodic=0
    g80: BSplineCurve PolesCount=3 KnotsCount=2 Degree=2 IsPeriodic=0
    g81: BSplineCurve PolesCount=3 KnotsCount=2 Degree=2 IsPeriodic=0
    g82: BSplineCurve PolesCount=3 KnotsCount=2 Degree=2 IsPeriodic=0
    g83: BSplineCurve PolesCount=3 KnotsCount=2 Degree=2 IsPeriodic=0
    g84: BSplineCurve PolesCount=3 KnotsCount=2 Degree=2 IsPeriodic=0
    g85: BSplineCurve PolesCount=3 KnotsCount=2 Degree=2 IsPeriodic=0
    g86: BSplineCurve PolesCount=3 KnotsCount=2 Degree=2 IsPeriodic=0
    g87: BSplineCurve PolesCount=3 KnotsCount=2 Degree=2 IsPeriodic=0
    g88: BSplineCurve PolesCount=3 KnotsCount=2 Degree=2 IsPeriodic=0
    g89: BSplineCurve PolesCount=3 KnotsCount=2 Degree=2 IsPeriodic=0
    g90: LineSegment StartX=5.86789 StartY=16.9213 StartZ=0 EndX=5.26931 EndY=16.9213 EndZ=0
    g91: LineSegment StartX=5.86789 StartY=17.3313 StartZ=0 EndX=5.86789 EndY=16.9213 EndZ=0
    g92: LineSegment StartX=5.26931 StartY=17.3313 StartZ=0 EndX=5.86789 EndY=17.3313 EndZ=0
    g93: LineSegment StartX=5.26931 StartY=20 StartZ=0 EndX=5.26931 EndY=17.3313 EndZ=0
    g94: LineSegment StartX=4.79647 StartY=20 StartZ=0 EndX=5.26931 EndY=20 EndZ=0
    g95: LineSegment StartX=2.89413 StartY=17.3039 StartZ=0 EndX=4.79647 EndY=20 EndZ=0
    g96: LineSegment StartX=2.89413 StartY=16.9213 StartZ=0 EndX=2.89413 EndY=17.3039 EndZ=0
    g97: LineSegment StartX=4.82653 StartY=16.9213 StartZ=0 EndX=2.89413 EndY=16.9213 EndZ=0
    g98: LineSegment StartX=4.82653 StartY=16 StartZ=0 EndX=4.82653 EndY=16.9213 EndZ=0
    g99: LineSegment StartX=5.26931 StartY=16 StartZ=0 EndX=4.82653 EndY=16 EndZ=0
    g100: LineSegment StartX=5.26931 StartY=16.9213 StartZ=0 EndX=5.26931 EndY=16 EndZ=0
    g101: LineSegment StartX=4.82653 StartY=17.3313 StartZ=0 EndX=4.82653 EndY=18.6303 EndZ=0
    g102: LineSegment StartX=3.34512 StartY=17.3313 StartZ=0 EndX=4.82653 EndY=17.3313 EndZ=0
    g103: LineSegment StartX=4.57781 StartY=19.0678 StartZ=0 EndX=3.34512 EndY=17.3313 EndZ=0
    g104: BSplineCurve PolesCount=3 KnotsCount=2 Degree=2 IsPeriodic=0
    g105: BSplineCurve PolesCount=3 KnotsCount=2 Degree=2 IsPeriodic=0
    g106: LineSegment StartX=4.85386 StartY=19.5135 StartZ=0 EndX=4.832 EndY=19.5135 EndZ=0
    g107: BSplineCurve PolesCount=3 KnotsCount=2 Degree=2 IsPeriodic=0
    g108: BSplineCurve PolesCount=3 KnotsCount=2 Degree=2 IsPeriodic=0
    g109: BSplineCurve PolesCount=3 KnotsCount=2 Degree=2 IsPeriodic=0
    g110: BSplineCurve PolesCount=3 KnotsCount=2 Degree=2 IsPeriodic=0
    g111: LineSegment StartX=6.76184 StartY=16 StartZ=0 EndX=8.40179 EndY=19.5845 EndZ=0
    g112: LineSegment StartX=7.25929 StartY=16 StartZ=0 EndX=6.76184 EndY=16 EndZ=0
    g113: LineSegment StartX=8.8883 StartY=19.6501 StartZ=0 EndX=7.25929 EndY=16 EndZ=0
    g114: LineSegment StartX=8.8883 StartY=20 StartZ=0 EndX=8.8883 EndY=19.6501 EndZ=0
    g115: LineSegment StartX=6.2234 StartY=20 StartZ=0 EndX=8.8883 EndY=20 EndZ=0
    g116: LineSegment StartX=6.2234 StartY=19.5845 StartZ=0 EndX=6.2234 EndY=20 EndZ=0
    g117: LineSegment StartX=8.40179 StartY=19.5845 StartZ=0 EndX=6.2234 EndY=19.5845 EndZ=0
  constraints (140):
    c: Coincident(g0,g1)
    c: Coincident(g1,g2)
    c: Coincident(g2,g3)
    c: Coincident(g3,g4)
    c: Coincident(g4,g5)
    c: Coincident(g5,g6)
    c: Coincident(g6,g7)
    c: Coincident(g7,g8)
    c: Coincident(g8,g9)
    c: Coincident(g9,g10)
    c: Coincident(g10,g11)
    c: Coincident(g11,g12)
    c: Coincident(g12,g0)
    c: Coincident(g13,g14)
    c: Coincident(g14,g15)
    c: Coincident(g15,g16)
    c: Coincident(g16,g17)
    c: Coincident(g17,g18)
    c: Coincident(g18,g19)
    c: Coincident(g19,g20)
    c: Coincident(g20,g21)
    c: Coincident(g21,g22)
    c: Coincident(g22,g23)
    c: Coincident(g23,g24)
    c: Coincident(g24,g13)
    c: Coincident(g25,g26)
    c: Coincident(g26,g27)
    c: Coincident(g27,g28)
    c: Coincident(g28,g29)
    c: Coincident(g29,g30)
    c: Coincident(g30,g31)
    c: Coincident(g31,g32)
    c: Coincident(g32,g25)
    c: Horizontal(g33)
    c: Coincident(g33,g34)
    c: Vertical(g34)
    c: Coincident(g34,g35)
    c: Horizontal(g35)
    c: Coincident(g35,g36)
    c: Coincident(g36,g37)
    c: Coincident(g37,g38)
    c: Coincident(g38,g39)
    c: Coincident(g39,g40)
    c: Coincident(g40,g41)
    c: Coincident(g41,g42)
    c: Coincident(g42,g43)
    c: Coincident(g43,g44)
    c: Vertical(g44)
    c: Coincident(g44,g33)
    c: Coincident(g45,g46)
    c: Coincident(g46,g47)
    c: Coincident(g47,g48)
    c: Coincident(g48,g49)
    c: Coincident(g49,g50)
    c: Coincident(g50,g51)
    c: Coincident(g51,g52)
    c: Coincident(g52,g53)
    c: Coincident(g53,g54)
    c: Coincident(g54,g55)
    c: Coincident(g55,g56)
    c: Coincident(g56,g57)
    c: Coincident(g57,g58)
    c: Coincident(g58,g59)
    c: Coincident(g59,g60)
    c: Coincident(g60,g61)
    c: Coincident(g61,g62)
    c: Coincident(g62,g63)
    c: Coincident(g63,g64)
    c: Coincident(g64,g65)
    c: Coincident(g65,g66)
    c: Coincident(g66,g67)
    c: Coincident(g67,g68)
    c: Coincident(g68,g45)
    c: Coincident(g69,g70)
    c: Coincident(g70,g71)
    c: Coincident(g71,g72)
    c: Coincident(g72,g73)
    c: Coincident(g73,g74)
    c: Coincident(g74,g75)
    c: Coincident(g75,g76)
    c: Coincident(g76,g77)
    c: Coincident(g77,g78)
    c: Coincident(g78,g79)
    c: Coincident(g79,g69)
    c: Coincident(g80,g81)
    c: Coincident(g81,g82)
    c: Coincident(g82,g83)
    c: Coincident(g83,g84)
    c: Coincident(g84,g85)
    c: Coincident(g85,g86)
    c: Coincident(g86,g87)
    c: Coincident(g87,g88)
    c: Coincident(g88,g89)
    c: Coincident(g89,g80)
    c: Horizontal(g90)
    c: Coincident(g90,g91)
    c: Vertical(g91)
    c: Coincident(g91,g92)
    c: Horizontal(g92)
    c: Coincident(g92,g93)
    c: Vertical(g93)
    c: Coincident(g93,g94)
    c: Horizontal(g94)
    c: Coincident(g94,g95)
    c: Coincident(g95,g96)
    c: Vertical(g96)
    c: Coincident(g96,g97)
    c: Horizontal(g97)
    c: Coincident(g97,g98)
    c: Vertical(g98)
    c: Coincident(g98,g99)
    c: Horizontal(g99)
    c: Coincident(g99,g100)
    c: Vertical(g100)
    c: Coincident(g100,g90)
    c: Vertical(g101)
    c: Coincident(g101,g102)
    c: Horizontal(g102)
    c: Coincident(g102,g103)
    c: Coincident(g103,g104)
    c: Coincident(g104,g105)
    c: Coincident(g105,g106)
    c: Horizontal(g106)
    c: Coincident(g106,g107)
    c: Coincident(g107,g108)
    c: Coincident(g108,g109)
    c: Coincident(g109,g110)
    c: Coincident(g110,g101)
    c: Coincident(g111,g112)
    c: Horizontal(g112)
    c: Coincident(g112,g113)
    c: Coincident(g113,g114)
    c: Vertical(g114)
    c: Coincident(g114,g115)
    c: Horizontal(g115)
    c: Coincident(g115,g116)
    c: Vertical(g116)
    c: Coincident(g116,g117)
    c: Horizontal(g117)
    c: Coincident(g117,g111)
FEATURE [PartDesign::Pocket] Pocket022
  BaseFeature = -> PolarPattern003
  Direction = (0,1,-2e-16)
  Length = 5
  Length2 = 5
  Placement = pos=(0,0,0) rot=(1,0,0;1.5708rad)
  Profile = -> Sketch042
  ReferenceAxis = -> Sketch042 [N_Axis]
  Refine = true
  Suppressed = false
  Type = 0
FEATURE [PartDesign::Body] Body003  label="Gear_0_1847"
  AllowCompound = false
  Group = -> [Sketch041,USE_Macro_v6_gear_profile004,Pad003,Pocket021,PolarPattern003,ShapeString002,Sketch042,Pocket022]
  Origin = -> Origin003
  Placement = pos=(0,-3,36) rot=(1,0,0;1.5708rad)
  Tip = -> Pocket022
FEATURE [Part::Part2DObjectPython] ShapeString003  # Draft 2D object (typed FeaturePython)
  FontFile = <userpath>/Documents/DV_Projects/8_Cycloidal_gearbox_paper/0_testbed/v0/V 0_1339/OpenSans-Regular.ttf
  Fuse = false
  Justification = 6
  JustificationReference = 0
  KeepLeftMargin = false
  MakeFace = true
  ObliqueAngle = 0
  Placement = pos=(-8,0,-16) rot=(-1,0,0;1.5708rad)
  ScaleToSize = true
  Size = 4
  String = 0.2356
  Tracking = 0
FEATURE [Sketcher::SketchObject] Sketch043  label="IF E Change005"
  ArcFitTolerance = 1e-06
  AttachmentSupport = -> [XZ_Plane004]
  FullyConstrained = false
  MakeInternals = false
  MapMode = 5
  Placement = pos=(0,0,0) rot=(1,0,0;1.5708rad)
  sketch-geometry (7):
    g0: Circle CenterX=0 CenterY=0 CenterZ=0 NormalX=0 NormalY=0 NormalZ=1 AngleXU=0 Radius=14
    g1: Circle [constr] CenterX=0 CenterY=0 CenterZ=0 NormalX=0 NormalY=0 NormalZ=1 AngleXU=0 Radius=46.6255
    g2: LineSegment [constr] StartX=14 StartY=0 StartZ=0 EndX=46.6255 EndY=0 EndZ=0
    g3: GeomPoint [constr] X=30.3128 Y=0 Z=0
    g4: Circle [constr] CenterX=0 CenterY=0 CenterZ=0 NormalX=0 NormalY=0 NormalZ=1 AngleXU=0 Radius=30.3128
    g5: Circle CenterX=-30.3128 CenterY=0 CenterZ=0 NormalX=0 NormalY=0 NormalZ=1 AngleXU=0 Radius=7.66
    g6: Circle [constr] CenterX=-31.4728 CenterY=0 CenterZ=0 NormalX=0 NormalY=0 NormalZ=1 AngleXU=0 Radius=6.5
  constraints (20):
    c: Diameter(g0) = 28  'Dia Bearing'
    c: Coincident(g0,g-1)
    c: Coincident(g1,g0)
    c: PointOnObject(g2,g0)
    c: PointOnObject(g2,g1)
    c: PointOnObject(g2,g-1)
    c: PointOnObject(g2,g-1)
    c: Symmetric(g2,g2,g3)
    c: Coincident(g4,g0)
    c: PointOnObject(g3,g4)
    c: Diameter(g5) = 15.32  'DPinOut+E+2dc'
    c: Diameter(g1) = 93.251
    c: Block(g1)
    c: Block(g4)
    c: PointOnObject(g6,g-1)
    c: Diameter(g6) = 13
    c: Tangent(g5,g6)
    c: PointOnObject(g5,g4)
    c: DistanceX(g6,g5) = 1.16
    c: Diameter(g4) = 60.6255
FEATURE [Sketcher::SketchObject] USE_Macro_v6_gear_profile005
  ArcFitTolerance = 1e-06
  AttachmentSupport = -> [XZ_Plane004]
  FullyConstrained = false
  MakeInternals = false
  MapMode = 5
  Placement = pos=(0,0,0) rot=(1,0,0;1.5708rad)
  sketch-geometry (1):
    g0: BSplineCurve PolesCount=3241 KnotsCount=3242 Degree=3 IsPeriodic=1
FEATURE [PartDesign::Pad] Pad004
  Direction = (0,-1,2e-16)
  Length = 7
  Length2 = 10
  Placement = pos=(0,0,0) rot=(1,0,0;1.5708rad)
  Profile = -> USE_Macro_v6_gear_profile005
  ReferenceAxis = -> USE_Macro_v6_gear_profile005 [N_Axis]
  Refine = true
  Suppressed = false
  Type = 0
FEATURE [PartDesign::Pocket] Pocket023
  BaseFeature = -> Pad004
  Direction = (0,1,-2e-16)
  Length = 5
  Length2 = 5
  Midplane = true
  Placement = pos=(0,0,0) rot=(1,0,0;1.5708rad)
  Profile = -> Sketch043
  ReferenceAxis = -> Sketch043 [N_Axis]
  Refine = true
  Suppressed = false
  Type = 1
FEATURE [PartDesign::PolarPattern] PolarPattern004
  Angle = 360
  Axis = -> Sketch043 [N_Axis]
  BaseFeature = -> Pocket023
  Mode = 0
  Occurrences = 10
  Offset = 120
  Originals = -> [Pocket023]
  Placement = pos=(0,0,0) rot=(1,0,0;1.5708rad)
  Refine = true
  Suppressed = false
  TransformMode = 0
FEATURE [Sketcher::SketchObject] Sketch044
  ArcFitTolerance = 1e-06
  AttachmentSupport = -> [PolarPattern004]
  FullyConstrained = false
  MakeInternals = false
  MapMode = 5
  Placement = pos=(0,-7,0) rot=(1,0,0;1.5708rad)
  sketch-geometry (156):
    g0: BSplineCurve PolesCount=3 KnotsCount=2 Degree=2 IsPeriodic=0
    g1: BSplineCurve PolesCount=3 KnotsCount=2 Degree=2 IsPeriodic=0
    g2: BSplineCurve PolesCount=3 KnotsCount=2 Degree=2 IsPeriodic=0
    g3: BSplineCurve PolesCount=3 KnotsCount=2 Degree=2 IsPeriodic=0
    g4: BSplineCurve PolesCount=3 KnotsCount=2 Degree=2 IsPeriodic=0
    g5: BSplineCurve PolesCount=3 KnotsCount=2 Degree=2 IsPeriodic=0
    g6: BSplineCurve PolesCount=3 KnotsCount=2 Degree=2 IsPeriodic=0
    g7: BSplineCurve PolesCount=3 KnotsCount=2 Degree=2 IsPeriodic=0
    g8: BSplineCurve PolesCount=3 KnotsCount=2 Degree=2 IsPeriodic=0
    g9: BSplineCurve PolesCount=3 KnotsCount=2 Degree=2 IsPeriodic=0
    g10: BSplineCurve PolesCount=3 KnotsCount=2 Degree=2 IsPeriodic=0
    g11: BSplineCurve PolesCount=3 KnotsCount=2 Degree=2 IsPeriodic=0
    g12: BSplineCurve PolesCount=3 KnotsCount=2 Degree=2 IsPeriodic=0
    g13: BSplineCurve PolesCount=3 KnotsCount=2 Degree=2 IsPeriodic=0
    g14: BSplineCurve PolesCount=3 KnotsCount=2 Degree=2 IsPeriodic=0
    g15: BSplineCurve PolesCount=3 KnotsCount=2 Degree=2 IsPeriodic=0
    g16: BSplineCurve PolesCount=3 KnotsCount=2 Degree=2 IsPeriodic=0
    g17: BSplineCurve PolesCount=3 KnotsCount=2 Degree=2 IsPeriodic=0
    g18: BSplineCurve PolesCount=3 KnotsCount=2 Degree=2 IsPeriodic=0
    g19: BSplineCurve PolesCount=3 KnotsCount=2 Degree=2 IsPeriodic=0
    g20: BSplineCurve PolesCount=3 KnotsCount=2 Degree=2 IsPeriodic=0
    g21: BSplineCurve PolesCount=3 KnotsCount=2 Degree=2 IsPeriodic=0
    g22: BSplineCurve PolesCount=3 KnotsCount=2 Degree=2 IsPeriodic=0
    g23: BSplineCurve PolesCount=3 KnotsCount=2 Degree=2 IsPeriodic=0
    g24: BSplineCurve PolesCount=3 KnotsCount=2 Degree=2 IsPeriodic=0
    g25: BSplineCurve PolesCount=3 KnotsCount=2 Degree=2 IsPeriodic=0
    g26: BSplineCurve PolesCount=3 KnotsCount=2 Degree=2 IsPeriodic=0
    g27: BSplineCurve PolesCount=3 KnotsCount=2 Degree=2 IsPeriodic=0
    g28: BSplineCurve PolesCount=3 KnotsCount=2 Degree=2 IsPeriodic=0
    g29: BSplineCurve PolesCount=3 KnotsCount=2 Degree=2 IsPeriodic=0
    g30: BSplineCurve PolesCount=3 KnotsCount=2 Degree=2 IsPeriodic=0
    g31: BSplineCurve PolesCount=3 KnotsCount=2 Degree=2 IsPeriodic=0
    g32: BSplineCurve PolesCount=3 KnotsCount=2 Degree=2 IsPeriodic=0
    g33: LineSegment StartX=-0.722303 StartY=16 StartZ=0 EndX=-3.34074 EndY=16 EndZ=0
    g34: LineSegment StartX=-0.722303 StartY=16.4155 StartZ=0 EndX=-0.722303 EndY=16 EndZ=0
    g35: LineSegment StartX=-2.76403 StartY=16.4155 StartZ=0 EndX=-0.722303 EndY=16.4155 EndZ=0
    g36: LineSegment StartX=-2.76403 StartY=16.4346 StartZ=0 EndX=-2.76403 EndY=16.4155 EndZ=0
    g37: LineSegment StartX=-1.89486 StartY=17.3028 StartZ=0 EndX=-2.76403 EndY=16.4346 EndZ=0
    g38: BSplineCurve PolesCount=3 KnotsCount=2 Degree=2 IsPeriodic=0
    g39: BSplineCurve PolesCount=3 KnotsCount=2 Degree=2 IsPeriodic=0
    g40: BSplineCurve PolesCount=3 KnotsCount=2 Degree=2 IsPeriodic=0
    g41: BSplineCurve PolesCount=3 KnotsCount=2 Degree=2 IsPeriodic=0
    g42: BSplineCurve PolesCount=3 KnotsCount=2 Degree=2 IsPeriodic=0
    g43: BSplineCurve PolesCount=3 KnotsCount=2 Degree=2 IsPeriodic=0
    g44: BSplineCurve PolesCount=3 KnotsCount=2 Degree=2 IsPeriodic=0
    g45: BSplineCurve PolesCount=3 KnotsCount=2 Degree=2 IsPeriodic=0
    g46: BSplineCurve PolesCount=3 KnotsCount=2 Degree=2 IsPeriodic=0
    g47: LineSegment StartX=-3.04555 StartY=19.2932 StartZ=0 EndX=-3.28881 EndY=19.5993 EndZ=0
    g48: BSplineCurve PolesCount=3 KnotsCount=2 Degree=2 IsPeriodic=0
    g49: BSplineCurve PolesCount=3 KnotsCount=2 Degree=2 IsPeriodic=0
    g50: BSplineCurve PolesCount=3 KnotsCount=2 Degree=2 IsPeriodic=0
    g51: BSplineCurve PolesCount=3 KnotsCount=2 Degree=2 IsPeriodic=0
    g52: BSplineCurve PolesCount=3 KnotsCount=2 Degree=2 IsPeriodic=0
    g53: BSplineCurve PolesCount=3 KnotsCount=2 Degree=2 IsPeriodic=0
    g54: BSplineCurve PolesCount=3 KnotsCount=2 Degree=2 IsPeriodic=0
    g55: LineSegment StartX=-3.34074 StartY=16.3799 StartZ=0 EndX=-2.27205 EndY=17.4676 EndZ=0
    g56: LineSegment StartX=-3.34074 StartY=16 StartZ=0 EndX=-3.34074 EndY=16.3799 EndZ=0
    g57: BSplineCurve PolesCount=3 KnotsCount=2 Degree=2 IsPeriodic=0
    g58: BSplineCurve PolesCount=3 KnotsCount=2 Degree=2 IsPeriodic=0
    g59: BSplineCurve PolesCount=3 KnotsCount=2 Degree=2 IsPeriodic=0
    g60: BSplineCurve PolesCount=3 KnotsCount=2 Degree=2 IsPeriodic=0
    g61: BSplineCurve PolesCount=3 KnotsCount=2 Degree=2 IsPeriodic=0
    g62: LineSegment StartX=0.084184 StartY=19.3342 StartZ=0 EndX=-0.145408 EndY=19.6458 EndZ=0
    g63: BSplineCurve PolesCount=3 KnotsCount=2 Degree=2 IsPeriodic=0
    g64: BSplineCurve PolesCount=3 KnotsCount=2 Degree=2 IsPeriodic=0
    g65: BSplineCurve PolesCount=3 KnotsCount=2 Degree=2 IsPeriodic=0
    g66: BSplineCurve PolesCount=3 KnotsCount=2 Degree=2 IsPeriodic=0
    g67: BSplineCurve PolesCount=3 KnotsCount=2 Degree=2 IsPeriodic=0
    g68: BSplineCurve PolesCount=3 KnotsCount=2 Degree=2 IsPeriodic=0
    g69: BSplineCurve PolesCount=3 KnotsCount=2 Degree=2 IsPeriodic=0
    g70: BSplineCurve PolesCount=3 KnotsCount=2 Degree=2 IsPeriodic=0
    g71: LineSegment StartX=0.439504 StartY=18.254 StartZ=0 EndX=0.84129 EndY=18.254 EndZ=0
    g72: LineSegment StartX=0.439504 StartY=17.8659 StartZ=0 EndX=0.439504 EndY=18.254 EndZ=0
    g73: LineSegment StartX=0.838557 StartY=17.8659 StartZ=0 EndX=0.439504 EndY=17.8659 EndZ=0
    g74: BSplineCurve PolesCount=3 KnotsCount=2 Degree=2 IsPeriodic=0
    g75: BSplineCurve PolesCount=3 KnotsCount=2 Degree=2 IsPeriodic=0
    g76: BSplineCurve PolesCount=3 KnotsCount=2 Degree=2 IsPeriodic=0
    g77: BSplineCurve PolesCount=3 KnotsCount=2 Degree=2 IsPeriodic=0
    g78: BSplineCurve PolesCount=3 KnotsCount=2 Degree=2 IsPeriodic=0
    g79: BSplineCurve PolesCount=3 KnotsCount=2 Degree=2 IsPeriodic=0
    g80: BSplineCurve PolesCount=3 KnotsCount=2 Degree=2 IsPeriodic=0
    g81: LineSegment StartX=-0.170007 StartY=16.1574 StartZ=0 EndX=-0.170007 EndY=16.5838 EndZ=0
    g82: BSplineCurve PolesCount=3 KnotsCount=2 Degree=2 IsPeriodic=0
    g83: BSplineCurve PolesCount=3 KnotsCount=2 Degree=2 IsPeriodic=0
    g84: BSplineCurve PolesCount=3 KnotsCount=2 Degree=2 IsPeriodic=0
    g85: BSplineCurve PolesCount=3 KnotsCount=2 Degree=2 IsPeriodic=0
    g86: BSplineCurve PolesCount=3 KnotsCount=2 Degree=2 IsPeriodic=0
    g87: BSplineCurve PolesCount=3 KnotsCount=2 Degree=2 IsPeriodic=0
    g88: BSplineCurve PolesCount=3 KnotsCount=2 Degree=2 IsPeriodic=0
    g89: LineSegment StartX=1.49453 StartY=18.1009 StartZ=0 EndX=1.49453 EndY=18.0791 EndZ=0
    g90: BSplineCurve PolesCount=3 KnotsCount=2 Degree=2 IsPeriodic=0
    g91: BSplineCurve PolesCount=3 KnotsCount=2 Degree=2 IsPeriodic=0
    g92: BSplineCurve PolesCount=3 KnotsCount=2 Degree=2 IsPeriodic=0
    g93: BSplineCurve PolesCount=3 KnotsCount=2 Degree=2 IsPeriodic=0
    g94: BSplineCurve PolesCount=3 KnotsCount=2 Degree=2 IsPeriodic=0
    g95: LineSegment StartX=3.77424 StartY=19.5845 StartZ=0 EndX=3.67311 EndY=18.3806 EndZ=0
    g96: LineSegment StartX=5.37318 StartY=19.5845 StartZ=0 EndX=3.77424 EndY=19.5845 EndZ=0
    g97: LineSegment StartX=5.37318 StartY=20 StartZ=0 EndX=5.37318 EndY=19.5845 EndZ=0
    g98: LineSegment StartX=3.38612 StartY=20 StartZ=0 EndX=5.37318 EndY=20 EndZ=0
    g99: LineSegment StartX=3.23305 StartY=18.1265 StartZ=0 EndX=3.38612 EndY=20 EndZ=0
    g100: LineSegment StartX=3.46265 StartY=17.9761 StartZ=0 EndX=3.23305 EndY=18.1265 EndZ=0
    g101: BSplineCurve PolesCount=3 KnotsCount=2 Degree=2 IsPeriodic=0
    g102: BSplineCurve PolesCount=3 KnotsCount=2 Degree=2 IsPeriodic=0
    g103: BSplineCurve PolesCount=3 KnotsCount=2 Degree=2 IsPeriodic=0
    g104: BSplineCurve PolesCount=3 KnotsCount=2 Degree=2 IsPeriodic=0
    g105: BSplineCurve PolesCount=3 KnotsCount=2 Degree=2 IsPeriodic=0
    g106: BSplineCurve PolesCount=3 KnotsCount=2 Degree=2 IsPeriodic=0
    g107: BSplineCurve PolesCount=3 KnotsCount=2 Degree=2 IsPeriodic=0
    g108: BSplineCurve PolesCount=3 KnotsCount=2 Degree=2 IsPeriodic=0
    g109: BSplineCurve PolesCount=3 KnotsCount=2 Degree=2 IsPeriodic=0
    g110: LineSegment StartX=3.13466 StartY=16.1574 StartZ=0 EndX=3.13466 EndY=16.5893 EndZ=0
    g111: BSplineCurve PolesCount=3 KnotsCount=2 Degree=2 IsPeriodic=0
    g112: BSplineCurve PolesCount=3 KnotsCount=2 Degree=2 IsPeriodic=0
    g113: BSplineCurve PolesCount=3 KnotsCount=2 Degree=2 IsPeriodic=0
    g114: BSplineCurve PolesCount=3 KnotsCount=2 Degree=2 IsPeriodic=0
    g115: BSplineCurve PolesCount=3 KnotsCount=2 Degree=2 IsPeriodic=0
    g116: BSplineCurve PolesCount=3 KnotsCount=2 Degree=2 IsPeriodic=0
    g117: BSplineCurve PolesCount=3 KnotsCount=2 Degree=2 IsPeriodic=0
    g118: BSplineCurve PolesCount=3 KnotsCount=2 Degree=2 IsPeriodic=0
    g119: BSplineCurve PolesCount=3 KnotsCount=2 Degree=2 IsPeriodic=0
    g120: BSplineCurve PolesCount=3 KnotsCount=2 Degree=2 IsPeriodic=0
    g121: BSplineCurve PolesCount=3 KnotsCount=2 Degree=2 IsPeriodic=0
    g122: BSplineCurve PolesCount=3 KnotsCount=2 Degree=2 IsPeriodic=0
    g123: BSplineCurve PolesCount=3 KnotsCount=2 Degree=2 IsPeriodic=0
    g124: BSplineCurve PolesCount=3 KnotsCount=2 Degree=2 IsPeriodic=0
    g125: BSplineCurve PolesCount=3 KnotsCount=2 Degree=2 IsPeriodic=0
    g126: BSplineCurve PolesCount=3 KnotsCount=2 Degree=2 IsPeriodic=0
    g127: BSplineCurve PolesCount=3 KnotsCount=2 Degree=2 IsPeriodic=0
    g128: BSplineCurve PolesCount=3 KnotsCount=2 Degree=2 IsPeriodic=0
    g129: BSplineCurve PolesCount=3 KnotsCount=2 Degree=2 IsPeriodic=0
    g130: BSplineCurve PolesCount=3 KnotsCount=2 Degree=2 IsPeriodic=0
    g131: BSplineCurve PolesCount=3 KnotsCount=2 Degree=2 IsPeriodic=0
    g132: LineSegment StartX=6.73998 StartY=18.0064 StartZ=0 EndX=6.77004 EndY=18.0064 EndZ=0
    g133: BSplineCurve PolesCount=3 KnotsCount=2 Degree=2 IsPeriodic=0
    g134: BSplineCurve PolesCount=3 KnotsCount=2 Degree=2 IsPeriodic=0
    g135: BSplineCurve PolesCount=3 KnotsCount=2 Degree=2 IsPeriodic=0
    g136: BSplineCurve PolesCount=3 KnotsCount=2 Degree=2 IsPeriodic=0
    g137: BSplineCurve PolesCount=3 KnotsCount=2 Degree=2 IsPeriodic=0
    g138: LineSegment StartX=8.59858 StartY=20.0093 StartZ=0 EndX=8.59858 EndY=19.6184 EndZ=0
    g139: BSplineCurve PolesCount=3 KnotsCount=2 Degree=2 IsPeriodic=0
    g140: BSplineCurve PolesCount=3 KnotsCount=2 Degree=2 IsPeriodic=0
    g141: BSplineCurve PolesCount=3 KnotsCount=2 Degree=2 IsPeriodic=0
    g142: BSplineCurve PolesCount=3 KnotsCount=2 Degree=2 IsPeriodic=0
    g143: BSplineCurve PolesCount=3 KnotsCount=2 Degree=2 IsPeriodic=0
    g144: BSplineCurve PolesCount=3 KnotsCount=2 Degree=2 IsPeriodic=0
    g145: BSplineCurve PolesCount=3 KnotsCount=2 Degree=2 IsPeriodic=0
    g146: BSplineCurve PolesCount=3 KnotsCount=2 Degree=2 IsPeriodic=0
    g147: BSplineCurve PolesCount=3 KnotsCount=2 Degree=2 IsPeriodic=0
    g148: BSplineCurve PolesCount=3 KnotsCount=2 Degree=2 IsPeriodic=0
    g149: BSplineCurve PolesCount=3 KnotsCount=2 Degree=2 IsPeriodic=0
    g150: BSplineCurve PolesCount=3 KnotsCount=2 Degree=2 IsPeriodic=0
    g151: BSplineCurve PolesCount=3 KnotsCount=2 Degree=2 IsPeriodic=0
    g152: BSplineCurve PolesCount=3 KnotsCount=2 Degree=2 IsPeriodic=0
    g153: BSplineCurve PolesCount=3 KnotsCount=2 Degree=2 IsPeriodic=0
    g154: BSplineCurve PolesCount=3 KnotsCount=2 Degree=2 IsPeriodic=0
    g155: BSplineCurve PolesCount=3 KnotsCount=2 Degree=2 IsPeriodic=0
  constraints (172):
    c: Coincident(g0,g1)
    c: Coincident(g1,g2)
    c: Coincident(g2,g3)
    c: Coincident(g3,g4)
    c: Coincident(g4,g5)
    c: Coincident(g5,g6)
    c: Coincident(g6,g7)
    c: Coincident(g7,g8)
    c: Coincident(g8,g9)
    c: Coincident(g9,g10)
    c: Coincident(g10,g11)
    c: Coincident(g11,g12)
    c: Coincident(g12,g0)
    c: Coincident(g13,g14)
    c: Coincident(g14,g15)
    c: Coincident(g15,g16)
    c: Coincident(g16,g17)
    c: Coincident(g17,g18)
    c: Coincident(g18,g19)
    c: Coincident(g19,g20)
    c: Coincident(g20,g21)
    c: Coincident(g21,g22)
    c: Coincident(g22,g23)
    c: Coincident(g23,g24)
    c: Coincident(g24,g13)
    c: Coincident(g25,g26)
    c: Coincident(g26,g27)
    c: Coincident(g27,g28)
    c: Coincident(g28,g29)
    c: Coincident(g29,g30)
    c: Coincident(g30,g31)
    c: Coincident(g31,g32)
    c: Coincident(g32,g25)
    c: Horizontal(g33)
    c: Coincident(g33,g34)
    c: Vertical(g34)
    c: Coincident(g34,g35)
    c: Horizontal(g35)
    c: Coincident(g35,g36)
    c: Vertical(g36)
    c: Coincident(g36,g37)
    c: Coincident(g37,g38)
    c: Coincident(g38,g39)
    c: Coincident(g39,g40)
    c: Coincident(g40,g41)
    c: Coincident(g41,g42)
    c: Coincident(g42,g43)
    c: Coincident(g43,g44)
    c: Coincident(g44,g45)
    c: Coincident(g45,g46)
    c: Coincident(g46,g47)
    c: Coincident(g47,g48)
    c: Coincident(g48,g49)
    c: Coincident(g49,g50)
    c: Coincident(g50,g51)
    c: Coincident(g51,g52)
    c: Coincident(g52,g53)
    c: Coincident(g53,g54)
    c: Coincident(g54,g55)
    c: Coincident(g55,g56)
    c: Vertical(g56)
    c: Coincident(g56,g33)
    c: Coincident(g57,g58)
    c: Coincident(g58,g59)
    c: Coincident(g59,g60)
    c: Coincident(g60,g61)
    c: Coincident(g61,g62)
    c: Coincident(g62,g63)
    c: Coincident(g63,g64)
    c: Coincident(g64,g65)
    c: Coincident(g65,g66)
    c: Coincident(g66,g67)
    c: Coincident(g67,g68)
    c: Coincident(g68,g69)
    c: Coincident(g69,g70)
    c: Coincident(g70,g71)
    c: Horizontal(g71)
    c: Coincident(g71,g72)
    c: Vertical(g72)
    c: Coincident(g72,g73)
    c: Horizontal(g73)
    c: Coincident(g73,g74)
    c: Coincident(g74,g75)
    c: Coincident(g75,g76)
    c: Coincident(g76,g77)
    c: Coincident(g77,g78)
    c: Coincident(g78,g79)
    c: Coincident(g79,g80)
    c: Coincident(g80,g81)
    c: Vertical(g81)
    c: Coincident(g81,g82)
    c: Coincident(g82,g83)
    c: Coincident(g83,g84)
    c: Coincident(g84,g85)
    c: Coincident(g85,g86)
    c: Coincident(g86,g87)
    c: Coincident(g87,g88)
    c: Coincident(g88,g89)
    c: Vertical(g89)
    c: Coincident(g89,g90)
    c: Coincident(g90,g91)
    c: Coincident(g91,g57)
    c: Coincident(g92,g93)
    c: Coincident(g93,g94)
    c: Coincident(g94,g95)
    c: Coincident(g95,g96)
    c: Horizontal(g96)
    c: Coincident(g96,g97)
    c: Vertical(g97)
    c: Coincident(g97,g98)
    c: Horizontal(g98)
    c: Coincident(g98,g99)
    c: Coincident(g99,g100)
    c: Coincident(g100,g101)
    c: Coincident(g101,g102)
    c: Coincident(g102,g103)
    c: Coincident(g103,g104)
    c: Coincident(g104,g105)
    c: Coincident(g105,g106)
    c: Coincident(g106,g107)
    c: Coincident(g107,g108)
    c: Coincident(g108,g109)
    c: Coincident(g109,g110)
    c: Vertical(g110)
    c: Coincident(g110,g111)
    c: Coincident(g111,g112)
    c: Coincident(g112,g113)
    c: Coincident(g113,g114)
    c: Coincident(g114,g115)
    c: Coincident(g115,g116)
    c: Coincident(g116,g117)
    c: Coincident(g117,g92)
    c: Coincident(g118,g119)
    c: Coincident(g119,g120)
    c: Coincident(g120,g121)
    c: Coincident(g121,g122)
    c: Coincident(g122,g123)
    c: Coincident(g123,g124)
    c: Coincident(g124,g125)
    c: Coincident(g125,g126)
    c: Coincident(g126,g127)
    c: Coincident(g127,g128)
    c: Coincident(g128,g129)
    c: Coincident(g129,g130)
    c: Coincident(g130,g131)
    c: Coincident(g131,g132)
    c: Horizontal(g132)
    c: Coincident(g132,g133)
    c: Coincident(g133,g134)
    c: Coincident(g134,g135)
    c: Coincident(g135,g136)
    c: Coincident(g136,g137)
    c: Coincident(g137,g138)
    c: Vertical(g138)
    c: Coincident(g138,g139)
    c: Coincident(g139,g140)
    c: Coincident(g140,g141)
    c: Coincident(g141,g142)
    c: Coincident(g142,g143)
    c: Coincident(g143,g144)
    c: Coincident(g144,g118)
    c: Coincident(g145,g146)
    c: Coincident(g146,g147)
    c: Coincident(g147,g148)
    c: Coincident(g148,g149)
    c: Coincident(g149,g150)
    c: Coincident(g150,g151)
    c: Coincident(g151,g152)
    c: Coincident(g152,g153)
    c: Coincident(g153,g154)
    c: Coincident(g154,g155)
    c: Coincident(g155,g145)
FEATURE [PartDesign::Pocket] Pocket024
  BaseFeature = -> PolarPattern004
  Direction = (0,1,-2e-16)
  Length = 5
  Length2 = 5
  Placement = pos=(0,0,0) rot=(1,0,0;1.5708rad)
  Profile = -> Sketch044
  ReferenceAxis = -> Sketch044 [N_Axis]
  Refine = true
  Suppressed = false
  Type = 0
FEATURE [PartDesign::Body] Body004  label="Gear_0_2356"
  AllowCompound = false
  Group = -> [Sketch043,USE_Macro_v6_gear_profile005,Pad004,Pocket023,PolarPattern004,ShapeString003,Sketch044,Pocket024]
  Origin = -> Origin004
  Placement = pos=(0,-3,48) rot=(1,0,0;1.5708rad)
  Tip = -> Pocket024
FEATURE [Part::Part2DObjectPython] ShapeString004  # Draft 2D object (typed FeaturePython)
  FontFile = <userpath>/Documents/DV_Projects/8_Cycloidal_gearbox_paper/0_testbed/v0/V 0_1339/OpenSans-Regular.ttf
  Fuse = false
  Justification = 6
  JustificationReference = 0
  KeepLeftMargin = false
  MakeFace = true
  ObliqueAngle = 0
  Placement = pos=(-8,0,-16) rot=(-1,0,0;1.5708rad)
  ScaleToSize = true
  Size = 4
  String = 0.2865
  Tracking = 0
FEATURE [Sketcher::SketchObject] Sketch045  label="IF E Change006"
  ArcFitTolerance = 1e-06
  AttachmentSupport = -> [XZ_Plane005]
  FullyConstrained = false
  MakeInternals = false
  MapMode = 5
  Placement = pos=(0,0,0) rot=(1,0,0;1.5708rad)
  sketch-geometry (7):
    g0: Circle CenterX=0 CenterY=0 CenterZ=0 NormalX=0 NormalY=0 NormalZ=1 AngleXU=0 Radius=14
    g1: Circle [constr] CenterX=0 CenterY=0 CenterZ=0 NormalX=0 NormalY=0 NormalZ=1 AngleXU=0 Radius=46.6255
    g2: LineSegment [constr] StartX=14 StartY=0 StartZ=0 EndX=46.6255 EndY=0 EndZ=0
    g3: GeomPoint [constr] X=30.3128 Y=0 Z=0
    g4: Circle [constr] CenterX=0 CenterY=0 CenterZ=0 NormalX=0 NormalY=0 NormalZ=1 AngleXU=0 Radius=30.3128
    g5: Circle CenterX=-30.3128 CenterY=0 CenterZ=0 NormalX=0 NormalY=0 NormalZ=1 AngleXU=0 Radius=7.66
    g6: Circle [constr] CenterX=-31.4728 CenterY=0 CenterZ=0 NormalX=0 NormalY=0 NormalZ=1 AngleXU=0 Radius=6.5
  constraints (20):
    c: Diameter(g0) = 28  'Dia Bearing'
    c: Coincident(g0,g-1)
    c: Coincident(g1,g0)
    c: PointOnObject(g2,g0)
    c: PointOnObject(g2,g1)
    c: PointOnObject(g2,g-1)
    c: PointOnObject(g2,g-1)
    c: Symmetric(g2,g2,g3)
    c: Coincident(g4,g0)
    c: PointOnObject(g3,g4)
    c: Diameter(g5) = 15.32  'DPinOut+E+2dc'
    c: Diameter(g1) = 93.251
    c: Block(g1)
    c: Block(g4)
    c: PointOnObject(g6,g-1)
    c: Diameter(g6) = 13
    c: Tangent(g5,g6)
    c: PointOnObject(g5,g4)
    c: DistanceX(g6,g5) = 1.16
    c: Diameter(g4) = 60.6255
FEATURE [Sketcher::SketchObject] USE_Macro_v6_gear_profile006
  ArcFitTolerance = 1e-06
  AttachmentSupport = -> [XZ_Plane005]
  FullyConstrained = false
  MakeInternals = false
  MapMode = 5
  Placement = pos=(0,0,0) rot=(1,0,0;1.5708rad)
  sketch-geometry (1):
    g0: BSplineCurve PolesCount=3241 KnotsCount=3242 Degree=3 IsPeriodic=1
FEATURE [PartDesign::Pad] Pad005
  Direction = (0,-1,2e-16)
  Length = 7
  Length2 = 10
  Placement = pos=(0,0,0) rot=(1,0,0;1.5708rad)
  Profile = -> USE_Macro_v6_gear_profile006
  ReferenceAxis = -> USE_Macro_v6_gear_profile006 [N_Axis]
  Refine = true
  Suppressed = false
  Type = 0
FEATURE [PartDesign::Pocket] Pocket025
  BaseFeature = -> Pad005
  Direction = (0,1,-2e-16)
  Length = 5
  Length2 = 5
  Midplane = true
  Placement = pos=(0,0,0) rot=(1,0,0;1.5708rad)
  Profile = -> Sketch045
  ReferenceAxis = -> Sketch045 [N_Axis]
  Refine = true
  Suppressed = false
  Type = 1
FEATURE [PartDesign::PolarPattern] PolarPattern005
  Angle = 360
  Axis = -> Sketch045 [N_Axis]
  BaseFeature = -> Pocket025
  Mode = 0
  Occurrences = 10
  Offset = 120
  Originals = -> [Pocket025]
  Placement = pos=(0,0,0) rot=(1,0,0;1.5708rad)
  Refine = true
  Suppressed = false
  TransformMode = 0
FEATURE [Sketcher::SketchObject] Sketch046
  ArcFitTolerance = 1e-06
  AttachmentSupport = -> [PolarPattern005]
  FullyConstrained = false
  MakeInternals = false
  MapMode = 5
  Placement = pos=(0,-7,0) rot=(1,0,0;1.5708rad)
  sketch-geometry (166):
    g0: BSplineCurve PolesCount=3 KnotsCount=2 Degree=2 IsPeriodic=0
    g1: BSplineCurve PolesCount=3 KnotsCount=2 Degree=2 IsPeriodic=0
    g2: BSplineCurve PolesCount=3 KnotsCount=2 Degree=2 IsPeriodic=0
    g3: BSplineCurve PolesCount=3 KnotsCount=2 Degree=2 IsPeriodic=0
    g4: BSplineCurve PolesCount=3 KnotsCount=2 Degree=2 IsPeriodic=0
    g5: BSplineCurve PolesCount=3 KnotsCount=2 Degree=2 IsPeriodic=0
    g6: BSplineCurve PolesCount=3 KnotsCount=2 Degree=2 IsPeriodic=0
    g7: BSplineCurve PolesCount=3 KnotsCount=2 Degree=2 IsPeriodic=0
    g8: BSplineCurve PolesCount=3 KnotsCount=2 Degree=2 IsPeriodic=0
    g9: BSplineCurve PolesCount=3 KnotsCount=2 Degree=2 IsPeriodic=0
    g10: BSplineCurve PolesCount=3 KnotsCount=2 Degree=2 IsPeriodic=0
    g11: BSplineCurve PolesCount=3 KnotsCount=2 Degree=2 IsPeriodic=0
    g12: BSplineCurve PolesCount=3 KnotsCount=2 Degree=2 IsPeriodic=0
    g13: BSplineCurve PolesCount=3 KnotsCount=2 Degree=2 IsPeriodic=0
    g14: BSplineCurve PolesCount=3 KnotsCount=2 Degree=2 IsPeriodic=0
    g15: BSplineCurve PolesCount=3 KnotsCount=2 Degree=2 IsPeriodic=0
    g16: BSplineCurve PolesCount=3 KnotsCount=2 Degree=2 IsPeriodic=0
    g17: BSplineCurve PolesCount=3 KnotsCount=2 Degree=2 IsPeriodic=0
    g18: BSplineCurve PolesCount=3 KnotsCount=2 Degree=2 IsPeriodic=0
    g19: BSplineCurve PolesCount=3 KnotsCount=2 Degree=2 IsPeriodic=0
    g20: BSplineCurve PolesCount=3 KnotsCount=2 Degree=2 IsPeriodic=0
    g21: BSplineCurve PolesCount=3 KnotsCount=2 Degree=2 IsPeriodic=0
    g22: BSplineCurve PolesCount=3 KnotsCount=2 Degree=2 IsPeriodic=0
    g23: BSplineCurve PolesCount=3 KnotsCount=2 Degree=2 IsPeriodic=0
    g24: BSplineCurve PolesCount=3 KnotsCount=2 Degree=2 IsPeriodic=0
    g25: BSplineCurve PolesCount=3 KnotsCount=2 Degree=2 IsPeriodic=0
    g26: BSplineCurve PolesCount=3 KnotsCount=2 Degree=2 IsPeriodic=0
    g27: BSplineCurve PolesCount=3 KnotsCount=2 Degree=2 IsPeriodic=0
    g28: BSplineCurve PolesCount=3 KnotsCount=2 Degree=2 IsPeriodic=0
    g29: BSplineCurve PolesCount=3 KnotsCount=2 Degree=2 IsPeriodic=0
    g30: BSplineCurve PolesCount=3 KnotsCount=2 Degree=2 IsPeriodic=0
    g31: BSplineCurve PolesCount=3 KnotsCount=2 Degree=2 IsPeriodic=0
    g32: BSplineCurve PolesCount=3 KnotsCount=2 Degree=2 IsPeriodic=0
    g33: LineSegment StartX=-0.722303 StartY=16 StartZ=0 EndX=-3.34074 EndY=16 EndZ=0
    g34: LineSegment StartX=-0.722303 StartY=16.4155 StartZ=0 EndX=-0.722303 EndY=16 EndZ=0
    g35: LineSegment StartX=-2.76403 StartY=16.4155 StartZ=0 EndX=-0.722303 EndY=16.4155 EndZ=0
    g36: LineSegment StartX=-2.76403 StartY=16.4346 StartZ=0 EndX=-2.76403 EndY=16.4155 EndZ=0
    g37: LineSegment StartX=-1.89486 StartY=17.3028 StartZ=0 EndX=-2.76403 EndY=16.4346 EndZ=0
    g38: BSplineCurve PolesCount=3 KnotsCount=2 Degree=2 IsPeriodic=0
    g39: BSplineCurve PolesCount=3 KnotsCount=2 Degree=2 IsPeriodic=0
    g40: BSplineCurve PolesCount=3 KnotsCount=2 Degree=2 IsPeriodic=0
    g41: BSplineCurve PolesCount=3 KnotsCount=2 Degree=2 IsPeriodic=0
    g42: BSplineCurve PolesCount=3 KnotsCount=2 Degree=2 IsPeriodic=0
    g43: BSplineCurve PolesCount=3 KnotsCount=2 Degree=2 IsPeriodic=0
    g44: BSplineCurve PolesCount=3 KnotsCount=2 Degree=2 IsPeriodic=0
    g45: BSplineCurve PolesCount=3 KnotsCount=2 Degree=2 IsPeriodic=0
    g46: BSplineCurve PolesCount=3 KnotsCount=2 Degree=2 IsPeriodic=0
    g47: LineSegment StartX=-3.04555 StartY=19.2932 StartZ=0 EndX=-3.28881 EndY=19.5993 EndZ=0
    g48: BSplineCurve PolesCount=3 KnotsCount=2 Degree=2 IsPeriodic=0
    g49: BSplineCurve PolesCount=3 KnotsCount=2 Degree=2 IsPeriodic=0
    g50: BSplineCurve PolesCount=3 KnotsCount=2 Degree=2 IsPeriodic=0
    g51: BSplineCurve PolesCount=3 KnotsCount=2 Degree=2 IsPeriodic=0
    g52: BSplineCurve PolesCount=3 KnotsCount=2 Degree=2 IsPeriodic=0
    g53: BSplineCurve PolesCount=3 KnotsCount=2 Degree=2 IsPeriodic=0
    g54: BSplineCurve PolesCount=3 KnotsCount=2 Degree=2 IsPeriodic=0
    g55: LineSegment StartX=-3.34074 StartY=16.3799 StartZ=0 EndX=-2.27205 EndY=17.4676 EndZ=0
    g56: LineSegment StartX=-3.34074 StartY=16 StartZ=0 EndX=-3.34074 EndY=16.3799 EndZ=0
    g57: BSplineCurve PolesCount=3 KnotsCount=2 Degree=2 IsPeriodic=0
    g58: BSplineCurve PolesCount=3 KnotsCount=2 Degree=2 IsPeriodic=0
    g59: BSplineCurve PolesCount=3 KnotsCount=2 Degree=2 IsPeriodic=0
    g60: BSplineCurve PolesCount=3 KnotsCount=2 Degree=2 IsPeriodic=0
    g61: BSplineCurve PolesCount=3 KnotsCount=2 Degree=2 IsPeriodic=0
    g62: BSplineCurve PolesCount=3 KnotsCount=2 Degree=2 IsPeriodic=0
    g63: BSplineCurve PolesCount=3 KnotsCount=2 Degree=2 IsPeriodic=0
    g64: BSplineCurve PolesCount=3 KnotsCount=2 Degree=2 IsPeriodic=0
    g65: BSplineCurve PolesCount=3 KnotsCount=2 Degree=2 IsPeriodic=0
    g66: BSplineCurve PolesCount=3 KnotsCount=2 Degree=2 IsPeriodic=0
    g67: BSplineCurve PolesCount=3 KnotsCount=2 Degree=2 IsPeriodic=0
    g68: BSplineCurve PolesCount=3 KnotsCount=2 Degree=2 IsPeriodic=0
    g69: BSplineCurve PolesCount=3 KnotsCount=2 Degree=2 IsPeriodic=0
    g70: BSplineCurve PolesCount=3 KnotsCount=2 Degree=2 IsPeriodic=0
    g71: BSplineCurve PolesCount=3 KnotsCount=2 Degree=2 IsPeriodic=0
    g72: BSplineCurve PolesCount=3 KnotsCount=2 Degree=2 IsPeriodic=0
    g73: BSplineCurve PolesCount=3 KnotsCount=2 Degree=2 IsPeriodic=0
    g74: BSplineCurve PolesCount=3 KnotsCount=2 Degree=2 IsPeriodic=0
    g75: BSplineCurve PolesCount=3 KnotsCount=2 Degree=2 IsPeriodic=0
    g76: BSplineCurve PolesCount=3 KnotsCount=2 Degree=2 IsPeriodic=0
    g77: BSplineCurve PolesCount=3 KnotsCount=2 Degree=2 IsPeriodic=0
    g78: BSplineCurve PolesCount=3 KnotsCount=2 Degree=2 IsPeriodic=0
    g79: BSplineCurve PolesCount=3 KnotsCount=2 Degree=2 IsPeriodic=0
    g80: BSplineCurve PolesCount=3 KnotsCount=2 Degree=2 IsPeriodic=0
    g81: BSplineCurve PolesCount=3 KnotsCount=2 Degree=2 IsPeriodic=0
    g82: BSplineCurve PolesCount=3 KnotsCount=2 Degree=2 IsPeriodic=0
    g83: BSplineCurve PolesCount=3 KnotsCount=2 Degree=2 IsPeriodic=0
    g84: BSplineCurve PolesCount=3 KnotsCount=2 Degree=2 IsPeriodic=0
    g85: LineSegment StartX=1.19388 StartY=17.8697 StartZ=0 EndX=1.09548 EndY=17.9054 EndZ=0
    g86: BSplineCurve PolesCount=3 KnotsCount=2 Degree=2 IsPeriodic=0
    g87: BSplineCurve PolesCount=3 KnotsCount=2 Degree=2 IsPeriodic=0
    g88: BSplineCurve PolesCount=3 KnotsCount=2 Degree=2 IsPeriodic=0
    g89: BSplineCurve PolesCount=3 KnotsCount=2 Degree=2 IsPeriodic=0
    g90: BSplineCurve PolesCount=3 KnotsCount=2 Degree=2 IsPeriodic=0
    g91: BSplineCurve PolesCount=3 KnotsCount=2 Degree=2 IsPeriodic=0
    g92: BSplineCurve PolesCount=3 KnotsCount=2 Degree=2 IsPeriodic=0
    g93: BSplineCurve PolesCount=3 KnotsCount=2 Degree=2 IsPeriodic=0
    g94: BSplineCurve PolesCount=3 KnotsCount=2 Degree=2 IsPeriodic=0
    g95: BSplineCurve PolesCount=3 KnotsCount=2 Degree=2 IsPeriodic=0
    g96: BSplineCurve PolesCount=3 KnotsCount=2 Degree=2 IsPeriodic=0
    g97: BSplineCurve PolesCount=3 KnotsCount=2 Degree=2 IsPeriodic=0
    g98: BSplineCurve PolesCount=3 KnotsCount=2 Degree=2 IsPeriodic=0
    g99: BSplineCurve PolesCount=3 KnotsCount=2 Degree=2 IsPeriodic=0
    g100: BSplineCurve PolesCount=3 KnotsCount=2 Degree=2 IsPeriodic=0
    g101: BSplineCurve PolesCount=3 KnotsCount=2 Degree=2 IsPeriodic=0
    g102: BSplineCurve PolesCount=3 KnotsCount=2 Degree=2 IsPeriodic=0
    g103: BSplineCurve PolesCount=3 KnotsCount=2 Degree=2 IsPeriodic=0
    g104: BSplineCurve PolesCount=3 KnotsCount=2 Degree=2 IsPeriodic=0
    g105: BSplineCurve PolesCount=3 KnotsCount=2 Degree=2 IsPeriodic=0
    g106: BSplineCurve PolesCount=3 KnotsCount=2 Degree=2 IsPeriodic=0
    g107: BSplineCurve PolesCount=3 KnotsCount=2 Degree=2 IsPeriodic=0
    g108: BSplineCurve PolesCount=3 KnotsCount=2 Degree=2 IsPeriodic=0
    g109: BSplineCurve PolesCount=3 KnotsCount=2 Degree=2 IsPeriodic=0
    g110: BSplineCurve PolesCount=3 KnotsCount=2 Degree=2 IsPeriodic=0
    g111: BSplineCurve PolesCount=3 KnotsCount=2 Degree=2 IsPeriodic=0
    g112: BSplineCurve PolesCount=3 KnotsCount=2 Degree=2 IsPeriodic=0
    g113: BSplineCurve PolesCount=3 KnotsCount=2 Degree=2 IsPeriodic=0
    g114: BSplineCurve PolesCount=3 KnotsCount=2 Degree=2 IsPeriodic=0
    g115: BSplineCurve PolesCount=3 KnotsCount=2 Degree=2 IsPeriodic=0
    g116: LineSegment StartX=3.54464 StartY=18.0064 StartZ=0 EndX=3.57471 EndY=18.0064 EndZ=0
    g117: BSplineCurve PolesCount=3 KnotsCount=2 Degree=2 IsPeriodic=0
    g118: BSplineCurve PolesCount=3 KnotsCount=2 Degree=2 IsPeriodic=0
    g119: BSplineCurve PolesCount=3 KnotsCount=2 Degree=2 IsPeriodic=0
    g120: BSplineCurve PolesCount=3 KnotsCount=2 Degree=2 IsPeriodic=0
    g121: BSplineCurve PolesCount=3 KnotsCount=2 Degree=2 IsPeriodic=0
    g122: LineSegment StartX=5.40324 StartY=20.0093 StartZ=0 EndX=5.40324 EndY=19.6184 EndZ=0
    g123: BSplineCurve PolesCount=3 KnotsCount=2 Degree=2 IsPeriodic=0
    g124: BSplineCurve PolesCount=3 KnotsCount=2 Degree=2 IsPeriodic=0
    g125: BSplineCurve PolesCount=3 KnotsCount=2 Degree=2 IsPeriodic=0
    g126: BSplineCurve PolesCount=3 KnotsCount=2 Degree=2 IsPeriodic=0
    g127: BSplineCurve PolesCount=3 KnotsCount=2 Degree=2 IsPeriodic=0
    g128: BSplineCurve PolesCount=3 KnotsCount=2 Degree=2 IsPeriodic=0
    g129: BSplineCurve PolesCount=3 KnotsCount=2 Degree=2 IsPeriodic=0
    g130: BSplineCurve PolesCount=3 KnotsCount=2 Degree=2 IsPeriodic=0
    g131: BSplineCurve PolesCount=3 KnotsCount=2 Degree=2 IsPeriodic=0
    g132: BSplineCurve PolesCount=3 KnotsCount=2 Degree=2 IsPeriodic=0
    g133: BSplineCurve PolesCount=3 KnotsCount=2 Degree=2 IsPeriodic=0
    g134: BSplineCurve PolesCount=3 KnotsCount=2 Degree=2 IsPeriodic=0
    g135: BSplineCurve PolesCount=3 KnotsCount=2 Degree=2 IsPeriodic=0
    g136: BSplineCurve PolesCount=3 KnotsCount=2 Degree=2 IsPeriodic=0
    g137: BSplineCurve PolesCount=3 KnotsCount=2 Degree=2 IsPeriodic=0
    g138: BSplineCurve PolesCount=3 KnotsCount=2 Degree=2 IsPeriodic=0
    g139: BSplineCurve PolesCount=3 KnotsCount=2 Degree=2 IsPeriodic=0
    g140: BSplineCurve PolesCount=3 KnotsCount=2 Degree=2 IsPeriodic=0
    g141: BSplineCurve PolesCount=3 KnotsCount=2 Degree=2 IsPeriodic=0
    g142: BSplineCurve PolesCount=3 KnotsCount=2 Degree=2 IsPeriodic=0
    g143: LineSegment StartX=6.96957 StartY=19.5845 StartZ=0 EndX=6.86844 EndY=18.3806 EndZ=0
    g144: LineSegment StartX=8.56851 StartY=19.5845 StartZ=0 EndX=6.96957 EndY=19.5845 EndZ=0
    g145: LineSegment StartX=8.56851 StartY=20 StartZ=0 EndX=8.56851 EndY=19.5845 EndZ=0
    g146: LineSegment StartX=6.58145 StartY=20 StartZ=0 EndX=8.56851 EndY=20 EndZ=0
    g147: LineSegment StartX=6.42839 StartY=18.1265 StartZ=0 EndX=6.58145 EndY=20 EndZ=0
    g148: LineSegment StartX=6.65798 StartY=17.9761 StartZ=0 EndX=6.42839 EndY=18.1265 EndZ=0
    g149: BSplineCurve PolesCount=3 KnotsCount=2 Degree=2 IsPeriodic=0
    g150: BSplineCurve PolesCount=3 KnotsCount=2 Degree=2 IsPeriodic=0
    g151: BSplineCurve PolesCount=3 KnotsCount=2 Degree=2 IsPeriodic=0
    g152: BSplineCurve PolesCount=3 KnotsCount=2 Degree=2 IsPeriodic=0
    g153: BSplineCurve PolesCount=3 KnotsCount=2 Degree=2 IsPeriodic=0
    g154: BSplineCurve PolesCount=3 KnotsCount=2 Degree=2 IsPeriodic=0
    g155: BSplineCurve PolesCount=3 KnotsCount=2 Degree=2 IsPeriodic=0
    g156: BSplineCurve PolesCount=3 KnotsCount=2 Degree=2 IsPeriodic=0
    g157: BSplineCurve PolesCount=3 KnotsCount=2 Degree=2 IsPeriodic=0
    g158: LineSegment StartX=6.32999 StartY=16.1574 StartZ=0 EndX=6.32999 EndY=16.5893 EndZ=0
    g159: BSplineCurve PolesCount=3 KnotsCount=2 Degree=2 IsPeriodic=0
    g160: BSplineCurve PolesCount=3 KnotsCount=2 Degree=2 IsPeriodic=0
    g161: BSplineCurve PolesCount=3 KnotsCount=2 Degree=2 IsPeriodic=0
    g162: BSplineCurve PolesCount=3 KnotsCount=2 Degree=2 IsPeriodic=0
    g163: BSplineCurve PolesCount=3 KnotsCount=2 Degree=2 IsPeriodic=0
    g164: BSplineCurve PolesCount=3 KnotsCount=2 Degree=2 IsPeriodic=0
    g165: BSplineCurve PolesCount=3 KnotsCount=2 Degree=2 IsPeriodic=0
  constraints (177):
    c: Coincident(g0,g1)
    c: Coincident(g1,g2)
    c: Coincident(g2,g3)
    c: Coincident(g3,g4)
    c: Coincident(g4,g5)
    c: Coincident(g5,g6)
    c: Coincident(g6,g7)
    c: Coincident(g7,g8)
    c: Coincident(g8,g9)
    c: Coincident(g9,g10)
    c: Coincident(g10,g11)
    c: Coincident(g11,g12)
    c: Coincident(g12,g0)
    c: Coincident(g13,g14)
    c: Coincident(g14,g15)
    c: Coincident(g15,g16)
    c: Coincident(g16,g17)
    c: Coincident(g17,g18)
    c: Coincident(g18,g19)
    c: Coincident(g19,g20)
    c: Coincident(g20,g21)
    c: Coincident(g21,g22)
    c: Coincident(g22,g23)
    c: Coincident(g23,g24)
    c: Coincident(g24,g13)
    c: Coincident(g25,g26)
    c: Coincident(g26,g27)
    c: Coincident(g27,g28)
    c: Coincident(g28,g29)
    c: Coincident(g29,g30)
    c: Coincident(g30,g31)
    c: Coincident(g31,g32)
    c: Coincident(g32,g25)
    c: Horizontal(g33)
    c: Coincident(g33,g34)
    c: Vertical(g34)
    c: Coincident(g34,g35)
    c: Horizontal(g35)
    c: Coincident(g35,g36)
    c: Vertical(g36)
    c: Coincident(g36,g37)
    c: Coincident(g37,g38)
    c: Coincident(g38,g39)
    c: Coincident(g39,g40)
    c: Coincident(g40,g41)
    c: Coincident(g41,g42)
    c: Coincident(g42,g43)
    c: Coincident(g43,g44)
    c: Coincident(g44,g45)
    c: Coincident(g45,g46)
    c: Coincident(g46,g47)
    c: Coincident(g47,g48)
    c: Coincident(g48,g49)
    c: Coincident(g49,g50)
    c: Coincident(g50,g51)
    c: Coincident(g51,g52)
    c: Coincident(g52,g53)
    c: Coincident(g53,g54)
    c: Coincident(g54,g55)
    c: Coincident(g55,g56)
    c: Vertical(g56)
    c: Coincident(g56,g33)
    c: Coincident(g57,g58)
    c: Coincident(g58,g59)
    c: Coincident(g59,g60)
    c: Coincident(g60,g61)
    c: Coincident(g61,g62)
    c: Coincident(g62,g63)
    c: Coincident(g63,g64)
    c: Coincident(g64,g65)
    c: Coincident(g65,g66)
    c: Coincident(g66,g67)
    c: Coincident(g67,g68)
    c: Coincident(g68,g69)
    c: Coincident(g69,g70)
    c: Coincident(g70,g71)
    c: Coincident(g71,g72)
    c: Coincident(g72,g73)
    c: Coincident(g73,g74)
    c: Coincident(g74,g75)
    c: Coincident(g75,g76)
    c: Coincident(g76,g77)
    c: Coincident(g77,g78)
    c: Coincident(g78,g79)
    c: Coincident(g79,g80)
    c: Coincident(g80,g57)
    c: Coincident(g81,g82)
    c: Coincident(g82,g83)
    c: Coincident(g83,g84)
    c: Coincident(g84,g85)
    c: Coincident(g85,g86)
    c: Coincident(g86,g87)
    c: Coincident(g87,g88)
    c: Coincident(g88,g89)
    c: Coincident(g89,g90)
    c: Coincident(g90,g91)
    c: Coincident(g91,g81)
    c: Coincident(g92,g93)
    c: Coincident(g93,g94)
    c: Coincident(g94,g95)
    c: Coincident(g95,g96)
    c: Coincident(g96,g97)
    c: Coincident(g97,g98)
    c: Coincident(g98,g99)
    c: Coincident(g99,g100)
    c: Coincident(g100,g101)
    c: Coincident(g101,g92)
    c: Coincident(g102,g103)
    c: Coincident(g103,g104)
    c: Coincident(g104,g105)
    c: Coincident(g105,g106)
    c: Coincident(g106,g107)
    c: Coincident(g107,g108)
    c: Coincident(g108,g109)
    c: Coincident(g109,g110)
    c: Coincident(g110,g111)
    c: Coincident(g111,g112)
    c: Coincident(g112,g113)
    c: Coincident(g113,g114)
    c: Coincident(g114,g115)
    c: Coincident(g115,g116)
    c: Horizontal(g116)
    c: Coincident(g116,g117)
    c: Coincident(g117,g118)
    c: Coincident(g118,g119)
    c: Coincident(g119,g120)
    c: Coincident(g120,g121)
    c: Coincident(g121,g122)
    c: Vertical(g122)
    c: Coincident(g122,g123)
    c: Coincident(g123,g124)
    c: Coincident(g124,g125)
    c: Coincident(g125,g126)
    c: Coincident(g126,g127)
    c: Coincident(g127,g128)
    c: Coincident(g128,g102)
    c: Coincident(g129,g130)
    c: Coincident(g130,g131)
    c: Coincident(g131,g132)
    c: Coincident(g132,g133)
    c: Coincident(g133,g134)
    c: Coincident(g134,g135)
    c: Coincident(g135,g136)
    c: Coincident(g136,g137)
    c: Coincident(g137,g138)
    c: Coincident(g138,g139)
    c: Coincident(g139,g129)
    c: Coincident(g140,g141)
    c: Coincident(g141,g142)
    c: Coincident(g142,g143)
    c: Coincident(g143,g144)
    c: Horizontal(g144)
    c: Coincident(g144,g145)
    c: Vertical(g145)
    c: Coincident(g145,g146)
    c: Horizontal(g146)
    c: Coincident(g146,g147)
    c: Coincident(g147,g148)
    c: Coincident(g148,g149)
    c: Coincident(g149,g150)
    c: Coincident(g150,g151)
    c: Coincident(g151,g152)
    c: Coincident(g152,g153)
    c: Coincident(g153,g154)
    c: Coincident(g154,g155)
    c: Coincident(g155,g156)
    c: Coincident(g156,g157)
    c: Coincident(g157,g158)
    c: Vertical(g158)
    c: Coincident(g158,g159)
    c: Coincident(g159,g160)
    c: Coincident(g160,g161)
    c: Coincident(g161,g162)
    c: Coincident(g162,g163)
    c: Coincident(g163,g164)
    c: Coincident(g164,g165)
    c: Coincident(g165,g140)
FEATURE [PartDesign::Pocket] Pocket026
  BaseFeature = -> PolarPattern005
  Direction = (0,1,-2e-16)
  Length = 5
  Length2 = 5
  Placement = pos=(0,0,0) rot=(1,0,0;1.5708rad)
  Profile = -> Sketch046
  ReferenceAxis = -> Sketch046 [N_Axis]
  Refine = true
  Suppressed = false
  Type = 0
FEATURE [PartDesign::Body] Body005  label="Gear_0_2865"
  AllowCompound = false
  Group = -> [Sketch045,USE_Macro_v6_gear_profile006,Pad005,Pocket025,PolarPattern005,ShapeString004,Sketch046,Pocket026]
  Origin = -> Origin005
  Placement = pos=(0,-3,60) rot=(1,0,0;1.5708rad)
  Tip = -> Pocket026
FEATURE [Part::Part2DObjectPython] ShapeString005  # Draft 2D object (typed FeaturePython)
  FontFile = <userpath>/Documents/DV_Projects/8_Cycloidal_gearbox_paper/0_testbed/v0/V 0_1339/OpenSans-Regular.ttf
  Fuse = false
  Justification = 6
  JustificationReference = 0
  KeepLeftMargin = false
  MakeFace = true
  ObliqueAngle = 0
  Placement = pos=(-8,0,-16) rot=(-1,0,0;1.5708rad)
  ScaleToSize = true
  Size = 4
  String = 0.3373
  Tracking = 0
FEATURE [Sketcher::SketchObject] Sketch047  label="IF E Change007"
  ArcFitTolerance = 1e-06
  AttachmentSupport = -> [XZ_Plane006]
  FullyConstrained = false
  MakeInternals = false
  MapMode = 5
  Placement = pos=(0,0,0) rot=(1,0,0;1.5708rad)
  sketch-geometry (7):
    g0: Circle CenterX=0 CenterY=0 CenterZ=0 NormalX=0 NormalY=0 NormalZ=1 AngleXU=0 Radius=14
    g1: Circle [constr] CenterX=0 CenterY=0 CenterZ=0 NormalX=0 NormalY=0 NormalZ=1 AngleXU=0 Radius=46.6255
    g2: LineSegment [constr] StartX=14 StartY=0 StartZ=0 EndX=46.6255 EndY=0 EndZ=0
    g3: GeomPoint [constr] X=30.3128 Y=0 Z=0
    g4: Circle [constr] CenterX=0 CenterY=0 CenterZ=0 NormalX=0 NormalY=0 NormalZ=1 AngleXU=0 Radius=30.3128
    g5: Circle CenterX=-30.3128 CenterY=0 CenterZ=0 NormalX=0 NormalY=0 NormalZ=1 AngleXU=0 Radius=7.66
    g6: Circle [constr] CenterX=-31.4728 CenterY=0 CenterZ=0 NormalX=0 NormalY=0 NormalZ=1 AngleXU=0 Radius=6.5
  constraints (20):
    c: Diameter(g0) = 28  'Dia Bearing'
    c: Coincident(g0,g-1)
    c: Coincident(g1,g0)
    c: PointOnObject(g2,g0)
    c: PointOnObject(g2,g1)
    c: PointOnObject(g2,g-1)
    c: PointOnObject(g2,g-1)
    c: Symmetric(g2,g2,g3)
    c: Coincident(g4,g0)
    c: PointOnObject(g3,g4)
    c: Diameter(g5) = 15.32  'DPinOut+E+2dc'
    c: Diameter(g1) = 93.251
    c: Block(g1)
    c: Block(g4)
    c: PointOnObject(g6,g-1)
    c: Diameter(g6) = 13
    c: Tangent(g5,g6)
    c: PointOnObject(g5,g4)
    c: DistanceX(g6,g5) = 1.16
    c: Diameter(g4) = 60.6255
FEATURE [Sketcher::SketchObject] USE_Macro_v6_gear_profile007
  ArcFitTolerance = 1e-06
  AttachmentSupport = -> [XZ_Plane006]
  FullyConstrained = false
  MakeInternals = false
  MapMode = 5
  Placement = pos=(0,0,0) rot=(1,0,0;1.5708rad)
  sketch-geometry (1):
    g0: BSplineCurve PolesCount=3241 KnotsCount=3242 Degree=3 IsPeriodic=1
FEATURE [PartDesign::Pad] Pad006  label="HERE001"
  Direction = (0,-1,2e-16)
  Length = 7
  Length2 = 10
  Placement = pos=(0,0,0) rot=(1,0,0;1.5708rad)
  Profile = -> USE_Macro_v6_gear_profile007
  ReferenceAxis = -> USE_Macro_v6_gear_profile007 [N_Axis]
  Refine = true
  Suppressed = false
  Type = 0
FEATURE [PartDesign::Pocket] Pocket027
  BaseFeature = -> Pad006
  Direction = (0,1,-2e-16)
  Length = 5
  Length2 = 5
  Midplane = true
  Placement = pos=(0,0,0) rot=(1,0,0;1.5708rad)
  Profile = -> Sketch047
  ReferenceAxis = -> Sketch047 [N_Axis]
  Refine = true
  Suppressed = false
  Type = 1
FEATURE [PartDesign::PolarPattern] PolarPattern006
  Angle = 360
  Axis = -> Sketch047 [N_Axis]
  BaseFeature = -> Pocket027
  Mode = 0
  Occurrences = 10
  Offset = 120
  Originals = -> [Pocket027]
  Placement = pos=(0,0,0) rot=(1,0,0;1.5708rad)
  Refine = true
  Suppressed = false
  TransformMode = 0
FEATURE [Sketcher::SketchObject] Sketch048
  ArcFitTolerance = 1e-06
  AttachmentSupport = -> [PolarPattern006]
  FullyConstrained = false
  MakeInternals = false
  MapMode = 5
  Placement = pos=(0,-7,0) rot=(1,0,0;1.5708rad)
  sketch-geometry (145):
    g0: BSplineCurve PolesCount=3 KnotsCount=2 Degree=2 IsPeriodic=0
    g1: BSplineCurve PolesCount=3 KnotsCount=2 Degree=2 IsPeriodic=0
    g2: BSplineCurve PolesCount=3 KnotsCount=2 Degree=2 IsPeriodic=0
    g3: BSplineCurve PolesCount=3 KnotsCount=2 Degree=2 IsPeriodic=0
    g4: BSplineCurve PolesCount=3 KnotsCount=2 Degree=2 IsPeriodic=0
    g5: BSplineCurve PolesCount=3 KnotsCount=2 Degree=2 IsPeriodic=0
    g6: BSplineCurve PolesCount=3 KnotsCount=2 Degree=2 IsPeriodic=0
    g7: BSplineCurve PolesCount=3 KnotsCount=2 Degree=2 IsPeriodic=0
    g8: BSplineCurve PolesCount=3 KnotsCount=2 Degree=2 IsPeriodic=0
    g9: BSplineCurve PolesCount=3 KnotsCount=2 Degree=2 IsPeriodic=0
    g10: BSplineCurve PolesCount=3 KnotsCount=2 Degree=2 IsPeriodic=0
    g11: BSplineCurve PolesCount=3 KnotsCount=2 Degree=2 IsPeriodic=0
    g12: BSplineCurve PolesCount=3 KnotsCount=2 Degree=2 IsPeriodic=0
    g13: BSplineCurve PolesCount=3 KnotsCount=2 Degree=2 IsPeriodic=0
    g14: BSplineCurve PolesCount=3 KnotsCount=2 Degree=2 IsPeriodic=0
    g15: BSplineCurve PolesCount=3 KnotsCount=2 Degree=2 IsPeriodic=0
    g16: BSplineCurve PolesCount=3 KnotsCount=2 Degree=2 IsPeriodic=0
    g17: BSplineCurve PolesCount=3 KnotsCount=2 Degree=2 IsPeriodic=0
    g18: BSplineCurve PolesCount=3 KnotsCount=2 Degree=2 IsPeriodic=0
    g19: BSplineCurve PolesCount=3 KnotsCount=2 Degree=2 IsPeriodic=0
    g20: BSplineCurve PolesCount=3 KnotsCount=2 Degree=2 IsPeriodic=0
    g21: BSplineCurve PolesCount=3 KnotsCount=2 Degree=2 IsPeriodic=0
    g22: BSplineCurve PolesCount=3 KnotsCount=2 Degree=2 IsPeriodic=0
    g23: BSplineCurve PolesCount=3 KnotsCount=2 Degree=2 IsPeriodic=0
    g24: BSplineCurve PolesCount=3 KnotsCount=2 Degree=2 IsPeriodic=0
    g25: BSplineCurve PolesCount=3 KnotsCount=2 Degree=2 IsPeriodic=0
    g26: BSplineCurve PolesCount=3 KnotsCount=2 Degree=2 IsPeriodic=0
    g27: BSplineCurve PolesCount=3 KnotsCount=2 Degree=2 IsPeriodic=0
    g28: BSplineCurve PolesCount=3 KnotsCount=2 Degree=2 IsPeriodic=0
    g29: BSplineCurve PolesCount=3 KnotsCount=2 Degree=2 IsPeriodic=0
    g30: BSplineCurve PolesCount=3 KnotsCount=2 Degree=2 IsPeriodic=0
    g31: BSplineCurve PolesCount=3 KnotsCount=2 Degree=2 IsPeriodic=0
    g32: BSplineCurve PolesCount=3 KnotsCount=2 Degree=2 IsPeriodic=0
    g33: BSplineCurve PolesCount=3 KnotsCount=2 Degree=2 IsPeriodic=0
    g34: BSplineCurve PolesCount=3 KnotsCount=2 Degree=2 IsPeriodic=0
    g35: BSplineCurve PolesCount=3 KnotsCount=2 Degree=2 IsPeriodic=0
    g36: BSplineCurve PolesCount=3 KnotsCount=2 Degree=2 IsPeriodic=0
    g37: BSplineCurve PolesCount=3 KnotsCount=2 Degree=2 IsPeriodic=0
    g38: LineSegment StartX=-3.11115 StartY=19.3342 StartZ=0 EndX=-3.34074 EndY=19.6458 EndZ=0
    g39: BSplineCurve PolesCount=3 KnotsCount=2 Degree=2 IsPeriodic=0
    g40: BSplineCurve PolesCount=3 KnotsCount=2 Degree=2 IsPeriodic=0
    g41: BSplineCurve PolesCount=3 KnotsCount=2 Degree=2 IsPeriodic=0
    g42: BSplineCurve PolesCount=3 KnotsCount=2 Degree=2 IsPeriodic=0
    g43: BSplineCurve PolesCount=3 KnotsCount=2 Degree=2 IsPeriodic=0
    g44: BSplineCurve PolesCount=3 KnotsCount=2 Degree=2 IsPeriodic=0
    g45: BSplineCurve PolesCount=3 KnotsCount=2 Degree=2 IsPeriodic=0
    g46: BSplineCurve PolesCount=3 KnotsCount=2 Degree=2 IsPeriodic=0
    g47: LineSegment StartX=-2.75583 StartY=18.254 StartZ=0 EndX=-2.35405 EndY=18.254 EndZ=0
    g48: LineSegment StartX=-2.75583 StartY=17.8659 StartZ=0 EndX=-2.75583 EndY=18.254 EndZ=0
    g49: LineSegment StartX=-2.35678 StartY=17.8659 StartZ=0 EndX=-2.75583 EndY=17.8659 EndZ=0
    g50: BSplineCurve PolesCount=3 KnotsCount=2 Degree=2 IsPeriodic=0
    g51: BSplineCurve PolesCount=3 KnotsCount=2 Degree=2 IsPeriodic=0
    g52: BSplineCurve PolesCount=3 KnotsCount=2 Degree=2 IsPeriodic=0
    g53: BSplineCurve PolesCount=3 KnotsCount=2 Degree=2 IsPeriodic=0
    g54: BSplineCurve PolesCount=3 KnotsCount=2 Degree=2 IsPeriodic=0
    g55: BSplineCurve PolesCount=3 KnotsCount=2 Degree=2 IsPeriodic=0
    g56: BSplineCurve PolesCount=3 KnotsCount=2 Degree=2 IsPeriodic=0
    g57: LineSegment StartX=-3.36534 StartY=16.1574 StartZ=0 EndX=-3.36534 EndY=16.5838 EndZ=0
    g58: BSplineCurve PolesCount=3 KnotsCount=2 Degree=2 IsPeriodic=0
    g59: BSplineCurve PolesCount=3 KnotsCount=2 Degree=2 IsPeriodic=0
    g60: BSplineCurve PolesCount=3 KnotsCount=2 Degree=2 IsPeriodic=0
    g61: BSplineCurve PolesCount=3 KnotsCount=2 Degree=2 IsPeriodic=0
    g62: BSplineCurve PolesCount=3 KnotsCount=2 Degree=2 IsPeriodic=0
    g63: BSplineCurve PolesCount=3 KnotsCount=2 Degree=2 IsPeriodic=0
    g64: BSplineCurve PolesCount=3 KnotsCount=2 Degree=2 IsPeriodic=0
    g65: LineSegment StartX=-1.7008 StartY=18.1009 StartZ=0 EndX=-1.7008 EndY=18.0791 EndZ=0
    g66: BSplineCurve PolesCount=3 KnotsCount=2 Degree=2 IsPeriodic=0
    g67: BSplineCurve PolesCount=3 KnotsCount=2 Degree=2 IsPeriodic=0
    g68: BSplineCurve PolesCount=3 KnotsCount=2 Degree=2 IsPeriodic=0
    g69: BSplineCurve PolesCount=3 KnotsCount=2 Degree=2 IsPeriodic=0
    g70: BSplineCurve PolesCount=3 KnotsCount=2 Degree=2 IsPeriodic=0
    g71: BSplineCurve PolesCount=3 KnotsCount=2 Degree=2 IsPeriodic=0
    g72: BSplineCurve PolesCount=3 KnotsCount=2 Degree=2 IsPeriodic=0
    g73: LineSegment StartX=0.084184 StartY=19.3342 StartZ=0 EndX=-0.145408 EndY=19.6458 EndZ=0
    g74: BSplineCurve PolesCount=3 KnotsCount=2 Degree=2 IsPeriodic=0
    g75: BSplineCurve PolesCount=3 KnotsCount=2 Degree=2 IsPeriodic=0
    g76: BSplineCurve PolesCount=3 KnotsCount=2 Degree=2 IsPeriodic=0
    g77: BSplineCurve PolesCount=3 KnotsCount=2 Degree=2 IsPeriodic=0
    g78: BSplineCurve PolesCount=3 KnotsCount=2 Degree=2 IsPeriodic=0
    g79: BSplineCurve PolesCount=3 KnotsCount=2 Degree=2 IsPeriodic=0
    g80: BSplineCurve PolesCount=3 KnotsCount=2 Degree=2 IsPeriodic=0
    g81: BSplineCurve PolesCount=3 KnotsCount=2 Degree=2 IsPeriodic=0
    g82: LineSegment StartX=0.439504 StartY=18.254 StartZ=0 EndX=0.84129 EndY=18.254 EndZ=0
    g83: LineSegment StartX=0.439504 StartY=17.8659 StartZ=0 EndX=0.439504 EndY=18.254 EndZ=0
    g84: LineSegment StartX=0.838557 StartY=17.8659 StartZ=0 EndX=0.439504 EndY=17.8659 EndZ=0
    g85: BSplineCurve PolesCount=3 KnotsCount=2 Degree=2 IsPeriodic=0
    g86: BSplineCurve PolesCount=3 KnotsCount=2 Degree=2 IsPeriodic=0
    g87: BSplineCurve PolesCount=3 KnotsCount=2 Degree=2 IsPeriodic=0
    g88: BSplineCurve PolesCount=3 KnotsCount=2 Degree=2 IsPeriodic=0
    g89: BSplineCurve PolesCount=3 KnotsCount=2 Degree=2 IsPeriodic=0
    g90: BSplineCurve PolesCount=3 KnotsCount=2 Degree=2 IsPeriodic=0
    g91: BSplineCurve PolesCount=3 KnotsCount=2 Degree=2 IsPeriodic=0
    g92: LineSegment StartX=-0.170007 StartY=16.1574 StartZ=0 EndX=-0.170007 EndY=16.5838 EndZ=0
    g93: BSplineCurve PolesCount=3 KnotsCount=2 Degree=2 IsPeriodic=0
    g94: BSplineCurve PolesCount=3 KnotsCount=2 Degree=2 IsPeriodic=0
    g95: BSplineCurve PolesCount=3 KnotsCount=2 Degree=2 IsPeriodic=0
    g96: BSplineCurve PolesCount=3 KnotsCount=2 Degree=2 IsPeriodic=0
    g97: BSplineCurve PolesCount=3 KnotsCount=2 Degree=2 IsPeriodic=0
    g98: BSplineCurve PolesCount=3 KnotsCount=2 Degree=2 IsPeriodic=0
    g99: BSplineCurve PolesCount=3 KnotsCount=2 Degree=2 IsPeriodic=0
    g100: LineSegment StartX=1.49453 StartY=18.1009 StartZ=0 EndX=1.49453 EndY=18.0791 EndZ=0
    g101: BSplineCurve PolesCount=3 KnotsCount=2 Degree=2 IsPeriodic=0
    g102: BSplineCurve PolesCount=3 KnotsCount=2 Degree=2 IsPeriodic=0
    g103: LineSegment StartX=3.56651 StartY=16 StartZ=0 EndX=5.20645 EndY=19.5845 EndZ=0
    g104: LineSegment StartX=4.06396 StartY=16 StartZ=0 EndX=3.56651 EndY=16 EndZ=0
    g105: LineSegment StartX=5.69297 StartY=19.6501 StartZ=0 EndX=4.06396 EndY=16 EndZ=0
    g106: LineSegment StartX=5.69297 StartY=20 StartZ=0 EndX=5.69297 EndY=19.6501 EndZ=0
    g107: LineSegment StartX=3.02806 StartY=20 StartZ=0 EndX=5.69297 EndY=20 EndZ=0
    g108: LineSegment StartX=3.02806 StartY=19.5845 StartZ=0 EndX=3.02806 EndY=20 EndZ=0
    g109: LineSegment StartX=5.20645 StartY=19.5845 StartZ=0 EndX=3.02806 EndY=19.5845 EndZ=0
    g110: BSplineCurve PolesCount=3 KnotsCount=2 Degree=2 IsPeriodic=0
    g111: BSplineCurve PolesCount=3 KnotsCount=2 Degree=2 IsPeriodic=0
    g112: BSplineCurve PolesCount=3 KnotsCount=2 Degree=2 IsPeriodic=0
    g113: BSplineCurve PolesCount=3 KnotsCount=2 Degree=2 IsPeriodic=0
    g114: BSplineCurve PolesCount=3 KnotsCount=2 Degree=2 IsPeriodic=0
    g115: LineSegment StartX=6.47485 StartY=19.3342 StartZ=0 EndX=6.24526 EndY=19.6458 EndZ=0
    g116: BSplineCurve PolesCount=3 KnotsCount=2 Degree=2 IsPeriodic=0
    g117: BSplineCurve PolesCount=3 KnotsCount=2 Degree=2 IsPeriodic=0
    g118: BSplineCurve PolesCount=3 KnotsCount=2 Degree=2 IsPeriodic=0
    g119: BSplineCurve PolesCount=3 KnotsCount=2 Degree=2 IsPeriodic=0
    g120: BSplineCurve PolesCount=3 KnotsCount=2 Degree=2 IsPeriodic=0
    g121: BSplineCurve PolesCount=3 KnotsCount=2 Degree=2 IsPeriodic=0
    g122: BSplineCurve PolesCount=3 KnotsCount=2 Degree=2 IsPeriodic=0
    g123: BSplineCurve PolesCount=3 KnotsCount=2 Degree=2 IsPeriodic=0
    g124: LineSegment StartX=6.83017 StartY=18.254 StartZ=0 EndX=7.23196 EndY=18.254 EndZ=0
    g125: LineSegment StartX=6.83017 StartY=17.8659 StartZ=0 EndX=6.83017 EndY=18.254 EndZ=0
    g126: LineSegment StartX=7.22923 StartY=17.8659 StartZ=0 EndX=6.83017 EndY=17.8659 EndZ=0
    g127: BSplineCurve PolesCount=3 KnotsCount=2 Degree=2 IsPeriodic=0
    g128: BSplineCurve PolesCount=3 KnotsCount=2 Degree=2 IsPeriodic=0
    g129: BSplineCurve PolesCount=3 KnotsCount=2 Degree=2 IsPeriodic=0
    g130: BSplineCurve PolesCount=3 KnotsCount=2 Degree=2 IsPeriodic=0
    g131: BSplineCurve PolesCount=3 KnotsCount=2 Degree=2 IsPeriodic=0
    g132: BSplineCurve PolesCount=3 KnotsCount=2 Degree=2 IsPeriodic=0
    g133: BSplineCurve PolesCount=3 KnotsCount=2 Degree=2 IsPeriodic=0
    g134: LineSegment StartX=6.22066 StartY=16.1574 StartZ=0 EndX=6.22066 EndY=16.5838 EndZ=0
    g135: BSplineCurve PolesCount=3 KnotsCount=2 Degree=2 IsPeriodic=0
    g136: BSplineCurve PolesCount=3 KnotsCount=2 Degree=2 IsPeriodic=0
    g137: BSplineCurve PolesCount=3 KnotsCount=2 Degree=2 IsPeriodic=0
    g138: BSplineCurve PolesCount=3 KnotsCount=2 Degree=2 IsPeriodic=0
    g139: BSplineCurve PolesCount=3 KnotsCount=2 Degree=2 IsPeriodic=0
    g140: BSplineCurve PolesCount=3 KnotsCount=2 Degree=2 IsPeriodic=0
    g141: BSplineCurve PolesCount=3 KnotsCount=2 Degree=2 IsPeriodic=0
    g142: LineSegment StartX=7.8852 StartY=18.1009 StartZ=0 EndX=7.8852 EndY=18.0791 EndZ=0
    g143: BSplineCurve PolesCount=3 KnotsCount=2 Degree=2 IsPeriodic=0
    g144: BSplineCurve PolesCount=3 KnotsCount=2 Degree=2 IsPeriodic=0
  constraints (165):
    c: Coincident(g0,g1)
    c: Coincident(g1,g2)
    c: Coincident(g2,g3)
    c: Coincident(g3,g4)
    c: Coincident(g4,g5)
    c: Coincident(g5,g6)
    c: Coincident(g6,g7)
    c: Coincident(g7,g8)
    c: Coincident(g8,g9)
    c: Coincident(g9,g10)
    c: Coincident(g10,g11)
    c: Coincident(g11,g12)
    c: Coincident(g12,g0)
    c: Coincident(g13,g14)
    c: Coincident(g14,g15)
    c: Coincident(g15,g16)
    c: Coincident(g16,g17)
    c: Coincident(g17,g18)
    c: Coincident(g18,g19)
    c: Coincident(g19,g20)
    c: Coincident(g20,g21)
    c: Coincident(g21,g22)
    c: Coincident(g22,g23)
    c: Coincident(g23,g24)
    c: Coincident(g24,g13)
    c: Coincident(g25,g26)
    c: Coincident(g26,g27)
    c: Coincident(g27,g28)
    c: Coincident(g28,g29)
    c: Coincident(g29,g30)
    c: Coincident(g30,g31)
    c: Coincident(g31,g32)
    c: Coincident(g32,g25)
    c: Coincident(g33,g34)
    c: Coincident(g34,g35)
    c: Coincident(g35,g36)
    c: Coincident(g36,g37)
    c: Coincident(g37,g38)
    c: Coincident(g38,g39)
    c: Coincident(g39,g40)
    c: Coincident(g40,g41)
    c: Coincident(g41,g42)
    c: Coincident(g42,g43)
    c: Coincident(g43,g44)
    c: Coincident(g44,g45)
    c: Coincident(g45,g46)
    c: Coincident(g46,g47)
    c: Horizontal(g47)
    c: Coincident(g47,g48)
    c: Vertical(g48)
    c: Coincident(g48,g49)
    c: Horizontal(g49)
    c: Coincident(g49,g50)
    c: Coincident(g50,g51)
    c: Coincident(g51,g52)
    c: Coincident(g52,g53)
    c: Coincident(g53,g54)
    c: Coincident(g54,g55)
    c: Coincident(g55,g56)
    c: Coincident(g56,g57)
    c: Vertical(g57)
    c: Coincident(g57,g58)
    c: Coincident(g58,g59)
    c: Coincident(g59,g60)
    c: Coincident(g60,g61)
    c: Coincident(g61,g62)
    c: Coincident(g62,g63)
    c: Coincident(g63,g64)
    c: Coincident(g64,g65)
    c: Vertical(g65)
    c: Coincident(g65,g66)
    c: Coincident(g66,g67)
    c: Coincident(g67,g33)
    c: Coincident(g68,g69)
    c: Coincident(g69,g70)
    c: Coincident(g70,g71)
    c: Coincident(g71,g72)
    c: Coincident(g72,g73)
    c: Coincident(g73,g74)
    c: Coincident(g74,g75)
    c: Coincident(g75,g76)
    c: Coincident(g76,g77)
    c: Coincident(g77,g78)
    c: Coincident(g78,g79)
    c: Coincident(g79,g80)
    c: Coincident(g80,g81)
    c: Coincident(g81,g82)
    c: Horizontal(g82)
    c: Coincident(g82,g83)
    c: Vertical(g83)
    c: Coincident(g83,g84)
    c: Horizontal(g84)
    c: Coincident(g84,g85)
    c: Coincident(g85,g86)
    c: Coincident(g86,g87)
    c: Coincident(g87,g88)
    c: Coincident(g88,g89)
    c: Coincident(g89,g90)
    c: Coincident(g90,g91)
    c: Coincident(g91,g92)
    c: Vertical(g92)
    c: Coincident(g92,g93)
    c: Coincident(g93,g94)
    c: Coincident(g94,g95)
    c: Coincident(g95,g96)
    c: Coincident(g96,g97)
    c: Coincident(g97,g98)
    c: Coincident(g98,g99)
    c: Coincident(g99,g100)
    c: Vertical(g100)
    c: Coincident(g100,g101)
    c: Coincident(g101,g102)
    c: Coincident(g102,g68)
    c: Coincident(g103,g104)
    c: Horizontal(g104)
    c: Coincident(g104,g105)
    c: Coincident(g105,g106)
    c: Vertical(g106)
    c: Coincident(g106,g107)
    c: Horizontal(g107)
    c: Coincident(g107,g108)
    c: Vertical(g108)
    c: Coincident(g108,g109)
    c: Horizontal(g109)
    c: Coincident(g109,g103)
    c: Coincident(g110,g111)
    c: Coincident(g111,g112)
    c: Coincident(g112,g113)
    c: Coincident(g113,g114)
    c: Coincident(g114,g115)
    c: Coincident(g115,g116)
    c: Coincident(g116,g117)
    c: Coincident(g117,g118)
    c: Coincident(g118,g119)
    c: Coincident(g119,g120)
    c: Coincident(g120,g121)
    c: Coincident(g121,g122)
    c: Coincident(g122,g123)
    c: Coincident(g123,g124)
    c: Horizontal(g124)
    c: Coincident(g124,g125)
    c: Vertical(g125)
    c: Coincident(g125,g126)
    c: Horizontal(g126)
    c: Coincident(g126,g127)
    c: Coincident(g127,g128)
    c: Coincident(g128,g129)
    c: Coincident(g129,g130)
    c: Coincident(g130,g131)
    c: Coincident(g131,g132)
    c: Coincident(g132,g133)
    c: Coincident(g133,g134)
    c: Vertical(g134)
    c: Coincident(g134,g135)
    c: Coincident(g135,g136)
    c: Coincident(g136,g137)
    c: Coincident(g137,g138)
    c: Coincident(g138,g139)
    c: Coincident(g139,g140)
    c: Coincident(g140,g141)
    c: Coincident(g141,g142)
    c: Vertical(g142)
    c: Coincident(g142,g143)
    c: Coincident(g143,g144)
    c: Coincident(g144,g110)
FEATURE [PartDesign::Pocket] Pocket028
  BaseFeature = -> PolarPattern006
  Direction = (0,1,-2e-16)
  Length = 5
  Length2 = 5
  Placement = pos=(0,0,0) rot=(1,0,0;1.5708rad)
  Profile = -> Sketch048
  ReferenceAxis = -> Sketch048 [N_Axis]
  Refine = true
  Suppressed = false
  Type = 0
FEATURE [PartDesign::Body] Body006  label="Gear_0_3373"
  AllowCompound = false
  Group = -> [Sketch047,USE_Macro_v6_gear_profile007,Pad006,Pocket027,PolarPattern006,ShapeString005,Sketch048,Pocket028]
  Origin = -> Origin006
  Placement = pos=(0,-3,72) rot=(1,0,0;1.5708rad)
  Tip = -> Pocket028
FEATURE [Part::Part2DObjectPython] ShapeString006  # Draft 2D object (typed FeaturePython)
  FontFile = <userpath>/Documents/DV_Projects/8_Cycloidal_gearbox_paper/0_testbed/v0/V 0_1339/OpenSans-Regular.ttf
  Fuse = false
  Justification = 6
  JustificationReference = 0
  KeepLeftMargin = false
  MakeFace = true
  ObliqueAngle = 0
  Placement = pos=(-8,0,-16) rot=(-1,0,0;1.5708rad)
  ScaleToSize = true
  Size = 4
  String = 0.3882
  Tracking = 0
FEATURE [Sketcher::SketchObject] Sketch049  label="IF E Change008"
  ArcFitTolerance = 1e-06
  AttachmentSupport = -> [XZ_Plane007]
  FullyConstrained = false
  MakeInternals = false
  MapMode = 5
  Placement = pos=(0,0,0) rot=(1,0,0;1.5708rad)
  sketch-geometry (7):
    g0: Circle CenterX=0 CenterY=0 CenterZ=0 NormalX=0 NormalY=0 NormalZ=1 AngleXU=0 Radius=14
    g1: Circle [constr] CenterX=0 CenterY=0 CenterZ=0 NormalX=0 NormalY=0 NormalZ=1 AngleXU=0 Radius=46.6255
    g2: LineSegment [constr] StartX=14 StartY=0 StartZ=0 EndX=46.6255 EndY=0 EndZ=0
    g3: GeomPoint [constr] X=30.3128 Y=0 Z=0
    g4: Circle [constr] CenterX=0 CenterY=0 CenterZ=0 NormalX=0 NormalY=0 NormalZ=1 AngleXU=0 Radius=30.3128
    g5: Circle CenterX=-30.3128 CenterY=0 CenterZ=0 NormalX=0 NormalY=0 NormalZ=1 AngleXU=0 Radius=7.66
    g6: Circle [constr] CenterX=-31.4728 CenterY=0 CenterZ=0 NormalX=0 NormalY=0 NormalZ=1 AngleXU=0 Radius=6.5
  constraints (20):
    c: Diameter(g0) = 28  'Dia Bearing'
    c: Coincident(g0,g-1)
    c: Coincident(g1,g0)
    c: PointOnObject(g2,g0)
    c: PointOnObject(g2,g1)
    c: PointOnObject(g2,g-1)
    c: PointOnObject(g2,g-1)
    c: Symmetric(g2,g2,g3)
    c: Coincident(g4,g0)
    c: PointOnObject(g3,g4)
    c: Diameter(g5) = 15.32  'DPinOut+E+2dc'
    c: Diameter(g1) = 93.251
    c: Block(g1)
    c: Block(g4)
    c: PointOnObject(g6,g-1)
    c: Diameter(g6) = 13
    c: Tangent(g5,g6)
    c: PointOnObject(g5,g4)
    c: DistanceX(g6,g5) = 1.16
    c: Diameter(g4) = 60.6255
FEATURE [Sketcher::SketchObject] USE_Macro_v6_gear_profile008
  ArcFitTolerance = 1e-06
  AttachmentSupport = -> [XZ_Plane007]
  FullyConstrained = false
  MakeInternals = false
  MapMode = 5
  Placement = pos=(0,0,0) rot=(1,0,0;1.5708rad)
  sketch-geometry (1):
    g0: BSplineCurve PolesCount=3241 KnotsCount=3242 Degree=3 IsPeriodic=1
FEATURE [PartDesign::Pad] Pad007  label="HERE002"
  Direction = (0,-1,2e-16)
  Length = 7
  Length2 = 10
  Placement = pos=(0,0,0) rot=(1,0,0;1.5708rad)
  Profile = -> USE_Macro_v6_gear_profile008
  ReferenceAxis = -> USE_Macro_v6_gear_profile008 [N_Axis]
  Refine = true
  Suppressed = false
  Type = 0
FEATURE [PartDesign::Pocket] Pocket029
  BaseFeature = -> Pad007
  Direction = (0,1,-2e-16)
  Length = 5
  Length2 = 5
  Midplane = true
  Placement = pos=(0,0,0) rot=(1,0,0;1.5708rad)
  Profile = -> Sketch049
  ReferenceAxis = -> Sketch049 [N_Axis]
  Refine = true
  Suppressed = false
  Type = 1
FEATURE [PartDesign::PolarPattern] PolarPattern007
  Angle = 360
  Axis = -> Sketch049 [N_Axis]
  BaseFeature = -> Pocket029
  Mode = 0
  Occurrences = 10
  Offset = 120
  Originals = -> [Pocket029]
  Placement = pos=(0,0,0) rot=(1,0,0;1.5708rad)
  Refine = true
  Suppressed = false
  TransformMode = 0
FEATURE [Sketcher::SketchObject] Sketch050
  ArcFitTolerance = 1e-06
  AttachmentSupport = -> [PolarPattern007]
  FullyConstrained = false
  MakeInternals = false
  MapMode = 5
  Placement = pos=(0,-7,0) rot=(1,0,0;1.5708rad)
  sketch-geometry (182):
    g0: BSplineCurve PolesCount=3 KnotsCount=2 Degree=2 IsPeriodic=0
    g1: BSplineCurve PolesCount=3 KnotsCount=2 Degree=2 IsPeriodic=0
    g2: BSplineCurve PolesCount=3 KnotsCount=2 Degree=2 IsPeriodic=0
    g3: BSplineCurve PolesCount=3 KnotsCount=2 Degree=2 IsPeriodic=0
    g4: BSplineCurve PolesCount=3 KnotsCount=2 Degree=2 IsPeriodic=0
    g5: BSplineCurve PolesCount=3 KnotsCount=2 Degree=2 IsPeriodic=0
    g6: BSplineCurve PolesCount=3 KnotsCount=2 Degree=2 IsPeriodic=0
    g7: BSplineCurve PolesCount=3 KnotsCount=2 Degree=2 IsPeriodic=0
    g8: BSplineCurve PolesCount=3 KnotsCount=2 Degree=2 IsPeriodic=0
    g9: BSplineCurve PolesCount=3 KnotsCount=2 Degree=2 IsPeriodic=0
    g10: BSplineCurve PolesCount=3 KnotsCount=2 Degree=2 IsPeriodic=0
    g11: BSplineCurve PolesCount=3 KnotsCount=2 Degree=2 IsPeriodic=0
    g12: BSplineCurve PolesCount=3 KnotsCount=2 Degree=2 IsPeriodic=0
    g13: BSplineCurve PolesCount=3 KnotsCount=2 Degree=2 IsPeriodic=0
    g14: BSplineCurve PolesCount=3 KnotsCount=2 Degree=2 IsPeriodic=0
    g15: BSplineCurve PolesCount=3 KnotsCount=2 Degree=2 IsPeriodic=0
    g16: BSplineCurve PolesCount=3 KnotsCount=2 Degree=2 IsPeriodic=0
    g17: BSplineCurve PolesCount=3 KnotsCount=2 Degree=2 IsPeriodic=0
    g18: BSplineCurve PolesCount=3 KnotsCount=2 Degree=2 IsPeriodic=0
    g19: BSplineCurve PolesCount=3 KnotsCount=2 Degree=2 IsPeriodic=0
    g20: BSplineCurve PolesCount=3 KnotsCount=2 Degree=2 IsPeriodic=0
    g21: BSplineCurve PolesCount=3 KnotsCount=2 Degree=2 IsPeriodic=0
    g22: BSplineCurve PolesCount=3 KnotsCount=2 Degree=2 IsPeriodic=0
    g23: BSplineCurve PolesCount=3 KnotsCount=2 Degree=2 IsPeriodic=0
    g24: BSplineCurve PolesCount=3 KnotsCount=2 Degree=2 IsPeriodic=0
    g25: BSplineCurve PolesCount=3 KnotsCount=2 Degree=2 IsPeriodic=0
    g26: BSplineCurve PolesCount=3 KnotsCount=2 Degree=2 IsPeriodic=0
    g27: BSplineCurve PolesCount=3 KnotsCount=2 Degree=2 IsPeriodic=0
    g28: BSplineCurve PolesCount=3 KnotsCount=2 Degree=2 IsPeriodic=0
    g29: BSplineCurve PolesCount=3 KnotsCount=2 Degree=2 IsPeriodic=0
    g30: BSplineCurve PolesCount=3 KnotsCount=2 Degree=2 IsPeriodic=0
    g31: BSplineCurve PolesCount=3 KnotsCount=2 Degree=2 IsPeriodic=0
    g32: BSplineCurve PolesCount=3 KnotsCount=2 Degree=2 IsPeriodic=0
    g33: BSplineCurve PolesCount=3 KnotsCount=2 Degree=2 IsPeriodic=0
    g34: BSplineCurve PolesCount=3 KnotsCount=2 Degree=2 IsPeriodic=0
    g35: BSplineCurve PolesCount=3 KnotsCount=2 Degree=2 IsPeriodic=0
    g36: BSplineCurve PolesCount=3 KnotsCount=2 Degree=2 IsPeriodic=0
    g37: BSplineCurve PolesCount=3 KnotsCount=2 Degree=2 IsPeriodic=0
    g38: LineSegment StartX=-3.11115 StartY=19.3342 StartZ=0 EndX=-3.34074 EndY=19.6458 EndZ=0
    g39: BSplineCurve PolesCount=3 KnotsCount=2 Degree=2 IsPeriodic=0
    g40: BSplineCurve PolesCount=3 KnotsCount=2 Degree=2 IsPeriodic=0
    g41: BSplineCurve PolesCount=3 KnotsCount=2 Degree=2 IsPeriodic=0
    g42: BSplineCurve PolesCount=3 KnotsCount=2 Degree=2 IsPeriodic=0
    g43: BSplineCurve PolesCount=3 KnotsCount=2 Degree=2 IsPeriodic=0
    g44: BSplineCurve PolesCount=3 KnotsCount=2 Degree=2 IsPeriodic=0
    g45: BSplineCurve PolesCount=3 KnotsCount=2 Degree=2 IsPeriodic=0
    g46: BSplineCurve PolesCount=3 KnotsCount=2 Degree=2 IsPeriodic=0
    g47: LineSegment StartX=-2.75583 StartY=18.254 StartZ=0 EndX=-2.35405 EndY=18.254 EndZ=0
    g48: LineSegment StartX=-2.75583 StartY=17.8659 StartZ=0 EndX=-2.75583 EndY=18.254 EndZ=0
    g49: LineSegment StartX=-2.35678 StartY=17.8659 StartZ=0 EndX=-2.75583 EndY=17.8659 EndZ=0
    g50: BSplineCurve PolesCount=3 KnotsCount=2 Degree=2 IsPeriodic=0
    g51: BSplineCurve PolesCount=3 KnotsCount=2 Degree=2 IsPeriodic=0
    g52: BSplineCurve PolesCount=3 KnotsCount=2 Degree=2 IsPeriodic=0
    g53: BSplineCurve PolesCount=3 KnotsCount=2 Degree=2 IsPeriodic=0
    g54: BSplineCurve PolesCount=3 KnotsCount=2 Degree=2 IsPeriodic=0
    g55: BSplineCurve PolesCount=3 KnotsCount=2 Degree=2 IsPeriodic=0
    g56: BSplineCurve PolesCount=3 KnotsCount=2 Degree=2 IsPeriodic=0
    g57: LineSegment StartX=-3.36534 StartY=16.1574 StartZ=0 EndX=-3.36534 EndY=16.5838 EndZ=0
    g58: BSplineCurve PolesCount=3 KnotsCount=2 Degree=2 IsPeriodic=0
    g59: BSplineCurve PolesCount=3 KnotsCount=2 Degree=2 IsPeriodic=0
    g60: BSplineCurve PolesCount=3 KnotsCount=2 Degree=2 IsPeriodic=0
    g61: BSplineCurve PolesCount=3 KnotsCount=2 Degree=2 IsPeriodic=0
    g62: BSplineCurve PolesCount=3 KnotsCount=2 Degree=2 IsPeriodic=0
    g63: BSplineCurve PolesCount=3 KnotsCount=2 Degree=2 IsPeriodic=0
    g64: BSplineCurve PolesCount=3 KnotsCount=2 Degree=2 IsPeriodic=0
    g65: LineSegment StartX=-1.7008 StartY=18.1009 StartZ=0 EndX=-1.7008 EndY=18.0791 EndZ=0
    g66: BSplineCurve PolesCount=3 KnotsCount=2 Degree=2 IsPeriodic=0
    g67: BSplineCurve PolesCount=3 KnotsCount=2 Degree=2 IsPeriodic=0
    g68: BSplineCurve PolesCount=3 KnotsCount=2 Degree=2 IsPeriodic=0
    g69: BSplineCurve PolesCount=3 KnotsCount=2 Degree=2 IsPeriodic=0
    g70: BSplineCurve PolesCount=3 KnotsCount=2 Degree=2 IsPeriodic=0
    g71: BSplineCurve PolesCount=3 KnotsCount=2 Degree=2 IsPeriodic=0
    g72: BSplineCurve PolesCount=3 KnotsCount=2 Degree=2 IsPeriodic=0
    g73: BSplineCurve PolesCount=3 KnotsCount=2 Degree=2 IsPeriodic=0
    g74: BSplineCurve PolesCount=3 KnotsCount=2 Degree=2 IsPeriodic=0
    g75: BSplineCurve PolesCount=3 KnotsCount=2 Degree=2 IsPeriodic=0
    g76: BSplineCurve PolesCount=3 KnotsCount=2 Degree=2 IsPeriodic=0
    g77: BSplineCurve PolesCount=3 KnotsCount=2 Degree=2 IsPeriodic=0
    g78: BSplineCurve PolesCount=3 KnotsCount=2 Degree=2 IsPeriodic=0
    g79: BSplineCurve PolesCount=3 KnotsCount=2 Degree=2 IsPeriodic=0
    g80: BSplineCurve PolesCount=3 KnotsCount=2 Degree=2 IsPeriodic=0
    g81: BSplineCurve PolesCount=3 KnotsCount=2 Degree=2 IsPeriodic=0
    g82: BSplineCurve PolesCount=3 KnotsCount=2 Degree=2 IsPeriodic=0
    g83: BSplineCurve PolesCount=3 KnotsCount=2 Degree=2 IsPeriodic=0
    g84: BSplineCurve PolesCount=3 KnotsCount=2 Degree=2 IsPeriodic=0
    g85: BSplineCurve PolesCount=3 KnotsCount=2 Degree=2 IsPeriodic=0
    g86: BSplineCurve PolesCount=3 KnotsCount=2 Degree=2 IsPeriodic=0
    g87: BSplineCurve PolesCount=3 KnotsCount=2 Degree=2 IsPeriodic=0
    g88: BSplineCurve PolesCount=3 KnotsCount=2 Degree=2 IsPeriodic=0
    g89: BSplineCurve PolesCount=3 KnotsCount=2 Degree=2 IsPeriodic=0
    g90: BSplineCurve PolesCount=3 KnotsCount=2 Degree=2 IsPeriodic=0
    g91: BSplineCurve PolesCount=3 KnotsCount=2 Degree=2 IsPeriodic=0
    g92: BSplineCurve PolesCount=3 KnotsCount=2 Degree=2 IsPeriodic=0
    g93: BSplineCurve PolesCount=3 KnotsCount=2 Degree=2 IsPeriodic=0
    g94: BSplineCurve PolesCount=3 KnotsCount=2 Degree=2 IsPeriodic=0
    g95: BSplineCurve PolesCount=3 KnotsCount=2 Degree=2 IsPeriodic=0
    g96: LineSegment StartX=1.19388 StartY=17.8697 StartZ=0 EndX=1.09548 EndY=17.9054 EndZ=0
    g97: BSplineCurve PolesCount=3 KnotsCount=2 Degree=2 IsPeriodic=0
    g98: BSplineCurve PolesCount=3 KnotsCount=2 Degree=2 IsPeriodic=0
    g99: BSplineCurve PolesCount=3 KnotsCount=2 Degree=2 IsPeriodic=0
    g100: BSplineCurve PolesCount=3 KnotsCount=2 Degree=2 IsPeriodic=0
    g101: BSplineCurve PolesCount=3 KnotsCount=2 Degree=2 IsPeriodic=0
    g102: BSplineCurve PolesCount=3 KnotsCount=2 Degree=2 IsPeriodic=0
    g103: BSplineCurve PolesCount=3 KnotsCount=2 Degree=2 IsPeriodic=0
    g104: BSplineCurve PolesCount=3 KnotsCount=2 Degree=2 IsPeriodic=0
    g105: BSplineCurve PolesCount=3 KnotsCount=2 Degree=2 IsPeriodic=0
    g106: BSplineCurve PolesCount=3 KnotsCount=2 Degree=2 IsPeriodic=0
    g107: BSplineCurve PolesCount=3 KnotsCount=2 Degree=2 IsPeriodic=0
    g108: BSplineCurve PolesCount=3 KnotsCount=2 Degree=2 IsPeriodic=0
    g109: BSplineCurve PolesCount=3 KnotsCount=2 Degree=2 IsPeriodic=0
    g110: BSplineCurve PolesCount=3 KnotsCount=2 Degree=2 IsPeriodic=0
    g111: BSplineCurve PolesCount=3 KnotsCount=2 Degree=2 IsPeriodic=0
    g112: BSplineCurve PolesCount=3 KnotsCount=2 Degree=2 IsPeriodic=0
    g113: BSplineCurve PolesCount=3 KnotsCount=2 Degree=2 IsPeriodic=0
    g114: BSplineCurve PolesCount=3 KnotsCount=2 Degree=2 IsPeriodic=0
    g115: BSplineCurve PolesCount=3 KnotsCount=2 Degree=2 IsPeriodic=0
    g116: BSplineCurve PolesCount=3 KnotsCount=2 Degree=2 IsPeriodic=0
    g117: BSplineCurve PolesCount=3 KnotsCount=2 Degree=2 IsPeriodic=0
    g118: BSplineCurve PolesCount=3 KnotsCount=2 Degree=2 IsPeriodic=0
    g119: BSplineCurve PolesCount=3 KnotsCount=2 Degree=2 IsPeriodic=0
    g120: BSplineCurve PolesCount=3 KnotsCount=2 Degree=2 IsPeriodic=0
    g121: BSplineCurve PolesCount=3 KnotsCount=2 Degree=2 IsPeriodic=0
    g122: BSplineCurve PolesCount=3 KnotsCount=2 Degree=2 IsPeriodic=0
    g123: BSplineCurve PolesCount=3 KnotsCount=2 Degree=2 IsPeriodic=0
    g124: BSplineCurve PolesCount=3 KnotsCount=2 Degree=2 IsPeriodic=0
    g125: BSplineCurve PolesCount=3 KnotsCount=2 Degree=2 IsPeriodic=0
    g126: BSplineCurve PolesCount=3 KnotsCount=2 Degree=2 IsPeriodic=0
    g127: BSplineCurve PolesCount=3 KnotsCount=2 Degree=2 IsPeriodic=0
    g128: BSplineCurve PolesCount=3 KnotsCount=2 Degree=2 IsPeriodic=0
    g129: BSplineCurve PolesCount=3 KnotsCount=2 Degree=2 IsPeriodic=0
    g130: BSplineCurve PolesCount=3 KnotsCount=2 Degree=2 IsPeriodic=0
    g131: BSplineCurve PolesCount=3 KnotsCount=2 Degree=2 IsPeriodic=0
    g132: BSplineCurve PolesCount=3 KnotsCount=2 Degree=2 IsPeriodic=0
    g133: BSplineCurve PolesCount=3 KnotsCount=2 Degree=2 IsPeriodic=0
    g134: BSplineCurve PolesCount=3 KnotsCount=2 Degree=2 IsPeriodic=0
    g135: BSplineCurve PolesCount=3 KnotsCount=2 Degree=2 IsPeriodic=0
    g136: BSplineCurve PolesCount=3 KnotsCount=2 Degree=2 IsPeriodic=0
    g137: BSplineCurve PolesCount=3 KnotsCount=2 Degree=2 IsPeriodic=0
    g138: BSplineCurve PolesCount=3 KnotsCount=2 Degree=2 IsPeriodic=0
    g139: BSplineCurve PolesCount=3 KnotsCount=2 Degree=2 IsPeriodic=0
    g140: BSplineCurve PolesCount=3 KnotsCount=2 Degree=2 IsPeriodic=0
    g141: LineSegment StartX=4.38921 StartY=17.8697 StartZ=0 EndX=4.29082 EndY=17.9054 EndZ=0
    g142: BSplineCurve PolesCount=3 KnotsCount=2 Degree=2 IsPeriodic=0
    g143: BSplineCurve PolesCount=3 KnotsCount=2 Degree=2 IsPeriodic=0
    g144: BSplineCurve PolesCount=3 KnotsCount=2 Degree=2 IsPeriodic=0
    g145: BSplineCurve PolesCount=3 KnotsCount=2 Degree=2 IsPeriodic=0
    g146: BSplineCurve PolesCount=3 KnotsCount=2 Degree=2 IsPeriodic=0
    g147: BSplineCurve PolesCount=3 KnotsCount=2 Degree=2 IsPeriodic=0
    g148: BSplineCurve PolesCount=3 KnotsCount=2 Degree=2 IsPeriodic=0
    g149: BSplineCurve PolesCount=3 KnotsCount=2 Degree=2 IsPeriodic=0
    g150: BSplineCurve PolesCount=3 KnotsCount=2 Degree=2 IsPeriodic=0
    g151: BSplineCurve PolesCount=3 KnotsCount=2 Degree=2 IsPeriodic=0
    g152: BSplineCurve PolesCount=3 KnotsCount=2 Degree=2 IsPeriodic=0
    g153: BSplineCurve PolesCount=3 KnotsCount=2 Degree=2 IsPeriodic=0
    g154: BSplineCurve PolesCount=3 KnotsCount=2 Degree=2 IsPeriodic=0
    g155: BSplineCurve PolesCount=3 KnotsCount=2 Degree=2 IsPeriodic=0
    g156: BSplineCurve PolesCount=3 KnotsCount=2 Degree=2 IsPeriodic=0
    g157: BSplineCurve PolesCount=3 KnotsCount=2 Degree=2 IsPeriodic=0
    g158: LineSegment StartX=8.8637 StartY=16 StartZ=0 EndX=6.24526 EndY=16 EndZ=0
    g159: LineSegment StartX=8.8637 StartY=16.4155 StartZ=0 EndX=8.8637 EndY=16 EndZ=0
    g160: LineSegment StartX=6.82198 StartY=16.4155 StartZ=0 EndX=8.8637 EndY=16.4155 EndZ=0
    g161: LineSegment StartX=6.82198 StartY=16.4346 StartZ=0 EndX=6.82198 EndY=16.4155 EndZ=0
    g162: LineSegment StartX=7.69114 StartY=17.3028 StartZ=0 EndX=6.82198 EndY=16.4346 EndZ=0
    g163: BSplineCurve PolesCount=3 KnotsCount=2 Degree=2 IsPeriodic=0
    g164: BSplineCurve PolesCount=3 KnotsCount=2 Degree=2 IsPeriodic=0
    g165: BSplineCurve PolesCount=3 KnotsCount=2 Degree=2 IsPeriodic=0
    g166: BSplineCurve PolesCount=3 KnotsCount=2 Degree=2 IsPeriodic=0
    g167: BSplineCurve PolesCount=3 KnotsCount=2 Degree=2 IsPeriodic=0
    g168: BSplineCurve PolesCount=3 KnotsCount=2 Degree=2 IsPeriodic=0
    g169: BSplineCurve PolesCount=3 KnotsCount=2 Degree=2 IsPeriodic=0
    g170: BSplineCurve PolesCount=3 KnotsCount=2 Degree=2 IsPeriodic=0
    g171: BSplineCurve PolesCount=3 KnotsCount=2 Degree=2 IsPeriodic=0
    g172: LineSegment StartX=6.54045 StartY=19.2932 StartZ=0 EndX=6.29719 EndY=19.5993 EndZ=0
    g173: BSplineCurve PolesCount=3 KnotsCount=2 Degree=2 IsPeriodic=0
    g174: BSplineCurve PolesCount=3 KnotsCount=2 Degree=2 IsPeriodic=0
    g175: BSplineCurve PolesCount=3 KnotsCount=2 Degree=2 IsPeriodic=0
    g176: BSplineCurve PolesCount=3 KnotsCount=2 Degree=2 IsPeriodic=0
    g177: BSplineCurve PolesCount=3 KnotsCount=2 Degree=2 IsPeriodic=0
    g178: BSplineCurve PolesCount=3 KnotsCount=2 Degree=2 IsPeriodic=0
    g179: BSplineCurve PolesCount=3 KnotsCount=2 Degree=2 IsPeriodic=0
    g180: LineSegment StartX=6.24526 StartY=16.3799 StartZ=0 EndX=7.31396 EndY=17.4676 EndZ=0
    g181: LineSegment StartX=6.24526 StartY=16 StartZ=0 EndX=6.24526 EndY=16.3799 EndZ=0
  constraints (192):
    c: Coincident(g0,g1)
    c: Coincident(g1,g2)
    c: Coincident(g2,g3)
    c: Coincident(g3,g4)
    c: Coincident(g4,g5)
    c: Coincident(g5,g6)
    c: Coincident(g6,g7)
    c: Coincident(g7,g8)
    c: Coincident(g8,g9)
    c: Coincident(g9,g10)
    c: Coincident(g10,g11)
    c: Coincident(g11,g12)
    c: Coincident(g12,g0)
    c: Coincident(g13,g14)
    c: Coincident(g14,g15)
    c: Coincident(g15,g16)
    c: Coincident(g16,g17)
    c: Coincident(g17,g18)
    c: Coincident(g18,g19)
    c: Coincident(g19,g20)
    c: Coincident(g20,g21)
    c: Coincident(g21,g22)
    c: Coincident(g22,g23)
    c: Coincident(g23,g24)
    c: Coincident(g24,g13)
    c: Coincident(g25,g26)
    c: Coincident(g26,g27)
    c: Coincident(g27,g28)
    c: Coincident(g28,g29)
    c: Coincident(g29,g30)
    c: Coincident(g30,g31)
    c: Coincident(g31,g32)
    c: Coincident(g32,g25)
    c: Coincident(g33,g34)
    c: Coincident(g34,g35)
    c: Coincident(g35,g36)
    c: Coincident(g36,g37)
    c: Coincident(g37,g38)
    c: Coincident(g38,g39)
    c: Coincident(g39,g40)
    c: Coincident(g40,g41)
    c: Coincident(g41,g42)
    c: Coincident(g42,g43)
    c: Coincident(g43,g44)
    c: Coincident(g44,g45)
    c: Coincident(g45,g46)
    c: Coincident(g46,g47)
    c: Horizontal(g47)
    c: Coincident(g47,g48)
    c: Vertical(g48)
    c: Coincident(g48,g49)
    c: Horizontal(g49)
    c: Coincident(g49,g50)
    c: Coincident(g50,g51)
    c: Coincident(g51,g52)
    c: Coincident(g52,g53)
    c: Coincident(g53,g54)
    c: Coincident(g54,g55)
    c: Coincident(g55,g56)
    c: Coincident(g56,g57)
    c: Vertical(g57)
    c: Coincident(g57,g58)
    c: Coincident(g58,g59)
    c: Coincident(g59,g60)
    c: Coincident(g60,g61)
    c: Coincident(g61,g62)
    c: Coincident(g62,g63)
    c: Coincident(g63,g64)
    c: Coincident(g64,g65)
    c: Vertical(g65)
    c: Coincident(g65,g66)
    c: Coincident(g66,g67)
    c: Coincident(g67,g33)
    c: Coincident(g68,g69)
    c: Coincident(g69,g70)
    c: Coincident(g70,g71)
    c: Coincident(g71,g72)
    c: Coincident(g72,g73)
    c: Coincident(g73,g74)
    c: Coincident(g74,g75)
    c: Coincident(g75,g76)
    c: Coincident(g76,g77)
    c: Coincident(g77,g78)
    c: Coincident(g78,g79)
    c: Coincident(g79,g80)
    c: Coincident(g80,g81)
    c: Coincident(g81,g82)
    c: Coincident(g82,g83)
    c: Coincident(g83,g84)
    c: Coincident(g84,g85)
    c: Coincident(g85,g86)
    c: Coincident(g86,g87)
    c: Coincident(g87,g88)
    c: Coincident(g88,g89)
    c: Coincident(g89,g90)
    c: Coincident(g90,g91)
    c: Coincident(g91,g68)
    c: Coincident(g92,g93)
    c: Coincident(g93,g94)
    c: Coincident(g94,g95)
    c: Coincident(g95,g96)
    c: Coincident(g96,g97)
    c: Coincident(g97,g98)
    c: Coincident(g98,g99)
    c: Coincident(g99,g100)
    c: Coincident(g100,g101)
    c: Coincident(g101,g102)
    c: Coincident(g102,g92)
    c: Coincident(g103,g104)
    c: Coincident(g104,g105)
    c: Coincident(g105,g106)
    c: Coincident(g106,g107)
    c: Coincident(g107,g108)
    c: Coincident(g108,g109)
    c: Coincident(g109,g110)
    c: Coincident(g110,g111)
    c: Coincident(g111,g112)
    c: Coincident(g112,g103)
    c: Coincident(g113,g114)
    c: Coincident(g114,g115)
    c: Coincident(g115,g116)
    c: Coincident(g116,g117)
    c: Coincident(g117,g118)
    c: Coincident(g118,g119)
    c: Coincident(g119,g120)
    c: Coincident(g120,g121)
    c: Coincident(g121,g122)
    c: Coincident(g122,g123)
    c: Coincident(g123,g124)
    c: Coincident(g124,g125)
    c: Coincident(g125,g126)
    c: Coincident(g126,g127)
    c: Coincident(g127,g128)
    c: Coincident(g128,g129)
    c: Coincident(g129,g130)
    c: Coincident(g130,g131)
    c: Coincident(g131,g132)
    c: Coincident(g132,g133)
    c: Coincident(g133,g134)
    c: Coincident(g134,g135)
    c: Coincident(g135,g136)
    c: Coincident(g136,g113)
    c: Coincident(g137,g138)
    c: Coincident(g138,g139)
    c: Coincident(g139,g140)
    c: Coincident(g140,g141)
    c: Coincident(g141,g142)
    c: Coincident(g142,g143)
    c: Coincident(g143,g144)
    c: Coincident(g144,g145)
    c: Coincident(g145,g146)
    c: Coincident(g146,g147)
    c: Coincident(g147,g137)
    c: Coincident(g148,g149)
    c: Coincident(g149,g150)
    c: Coincident(g150,g151)
    c: Coincident(g151,g152)
    c: Coincident(g152,g153)
    c: Coincident(g153,g154)
    c: Coincident(g154,g155)
    c: Coincident(g155,g156)
    c: Coincident(g156,g157)
    c: Coincident(g157,g148)
    c: Horizontal(g158)
    c: Coincident(g158,g159)
    c: Vertical(g159)
    c: Coincident(g159,g160)
    c: Horizontal(g160)
    c: Coincident(g160,g161)
    c: Vertical(g161)
    c: Coincident(g161,g162)
    c: Coincident(g162,g163)
    c: Coincident(g163,g164)
    c: Coincident(g164,g165)
    c: Coincident(g165,g166)
    c: Coincident(g166,g167)
    c: Coincident(g167,g168)
    c: Coincident(g168,g169)
    c: Coincident(g169,g170)
    c: Coincident(g170,g171)
    c: Coincident(g171,g172)
    c: Coincident(g172,g173)
    c: Coincident(g173,g174)
    c: Coincident(g174,g175)
    c: Coincident(g175,g176)
    c: Coincident(g176,g177)
    c: Coincident(g177,g178)
    c: Coincident(g178,g179)
    c: Coincident(g179,g180)
    c: Coincident(g180,g181)
    c: Vertical(g181)
    c: Coincident(g181,g158)
FEATURE [PartDesign::Pocket] Pocket030
  BaseFeature = -> PolarPattern007
  Direction = (0,1,-2e-16)
  Length = 5
  Length2 = 5
  Placement = pos=(0,0,0) rot=(1,0,0;1.5708rad)
  Profile = -> Sketch050
  ReferenceAxis = -> Sketch050 [N_Axis]
  Refine = true
  Suppressed = false
  Type = 0
FEATURE [PartDesign::Body] Body007  label="Gear_0_3882"
  AllowCompound = false
  Group = -> [Sketch049,USE_Macro_v6_gear_profile008,Pad007,Pocket029,PolarPattern007,ShapeString006,Sketch050,Pocket030]
  Origin = -> Origin007
  Placement = pos=(0,-3,84) rot=(1,0,0;1.5708rad)
  Tip = -> Pocket030
FEATURE [Part::Part2DObjectPython] ShapeString007  # Draft 2D object (typed FeaturePython)
  FontFile = <userpath>/Documents/DV_Projects/8_Cycloidal_gearbox_paper/0_testbed/v0/V 0_1339/OpenSans-Regular.ttf
  Fuse = false
  Justification = 6
  JustificationReference = 0
  KeepLeftMargin = false
  MakeFace = true
  ObliqueAngle = 0
  Placement = pos=(-8,0,-16) rot=(-1,0,0;1.5708rad)
  ScaleToSize = true
  Size = 4
  String = 0.4391
  Tracking = 0
FEATURE [Sketcher::SketchObject] Sketch051  label="IF E Change009"
  ArcFitTolerance = 1e-06
  AttachmentSupport = -> [XZ_Plane008]
  FullyConstrained = false
  MakeInternals = false
  MapMode = 5
  Placement = pos=(0,0,0) rot=(1,0,0;1.5708rad)
  sketch-geometry (7):
    g0: Circle CenterX=0 CenterY=0 CenterZ=0 NormalX=0 NormalY=0 NormalZ=1 AngleXU=0 Radius=14
    g1: Circle [constr] CenterX=0 CenterY=0 CenterZ=0 NormalX=0 NormalY=0 NormalZ=1 AngleXU=0 Radius=46.6255
    g2: LineSegment [constr] StartX=14 StartY=0 StartZ=0 EndX=46.6255 EndY=0 EndZ=0
    g3: GeomPoint [constr] X=30.3128 Y=0 Z=0
    g4: Circle [constr] CenterX=0 CenterY=0 CenterZ=0 NormalX=0 NormalY=0 NormalZ=1 AngleXU=0 Radius=30.3128
    g5: Circle CenterX=-30.3128 CenterY=0 CenterZ=0 NormalX=0 NormalY=0 NormalZ=1 AngleXU=0 Radius=7.66
    g6: Circle [constr] CenterX=-31.4728 CenterY=0 CenterZ=0 NormalX=0 NormalY=0 NormalZ=1 AngleXU=0 Radius=6.5
  constraints (20):
    c: Diameter(g0) = 28  'Dia Bearing'
    c: Coincident(g0,g-1)
    c: Coincident(g1,g0)
    c: PointOnObject(g2,g0)
    c: PointOnObject(g2,g1)
    c: PointOnObject(g2,g-1)
    c: PointOnObject(g2,g-1)
    c: Symmetric(g2,g2,g3)
    c: Coincident(g4,g0)
    c: PointOnObject(g3,g4)
    c: Diameter(g5) = 15.32  'DPinOut+E+2dc'
    c: Diameter(g1) = 93.251
    c: Block(g1)
    c: Block(g4)
    c: PointOnObject(g6,g-1)
    c: Diameter(g6) = 13
    c: Tangent(g5,g6)
    c: PointOnObject(g5,g4)
    c: DistanceX(g6,g5) = 1.16
    c: Diameter(g4) = 60.6255
FEATURE [Sketcher::SketchObject] USE_Macro_v6_gear_profile009
  ArcFitTolerance = 1e-06
  AttachmentSupport = -> [XZ_Plane008]
  FullyConstrained = false
  MakeInternals = false
  MapMode = 5
  Placement = pos=(0,0,0) rot=(1,0,0;1.5708rad)
  sketch-geometry (1):
    g0: BSplineCurve PolesCount=3241 KnotsCount=3242 Degree=3 IsPeriodic=1
FEATURE [PartDesign::Pad] Pad008  label="HERE003"
  Direction = (0,-1,2e-16)
  Length = 7
  Length2 = 10
  Placement = pos=(0,0,0) rot=(1,0,0;1.5708rad)
  Profile = -> USE_Macro_v6_gear_profile009
  ReferenceAxis = -> USE_Macro_v6_gear_profile009 [N_Axis]
  Refine = true
  Suppressed = false
  Type = 0
FEATURE [PartDesign::Pocket] Pocket031
  BaseFeature = -> Pad008
  Direction = (0,1,-2e-16)
  Length = 5
  Length2 = 5
  Midplane = true
  Placement = pos=(0,0,0) rot=(1,0,0;1.5708rad)
  Profile = -> Sketch051
  ReferenceAxis = -> Sketch051 [N_Axis]
  Refine = true
  Suppressed = false
  Type = 1
FEATURE [PartDesign::PolarPattern] PolarPattern008
  Angle = 360
  Axis = -> Sketch051 [N_Axis]
  BaseFeature = -> Pocket031
  Mode = 0
  Occurrences = 10
  Offset = 120
  Originals = -> [Pocket031]
  Placement = pos=(0,0,0) rot=(1,0,0;1.5708rad)
  Refine = true
  Suppressed = false
  TransformMode = 0
FEATURE [Sketcher::SketchObject] Sketch052
  ArcFitTolerance = 1e-06
  AttachmentSupport = -> [PolarPattern008]
  FullyConstrained = false
  MakeInternals = false
  MapMode = 5
  Placement = pos=(0,-7,0) rot=(1,0,0;1.5708rad)
  sketch-geometry (139):
    g0: BSplineCurve PolesCount=3 KnotsCount=2 Degree=2 IsPeriodic=0
    g1: BSplineCurve PolesCount=3 KnotsCount=2 Degree=2 IsPeriodic=0
    g2: BSplineCurve PolesCount=3 KnotsCount=2 Degree=2 IsPeriodic=0
    g3: BSplineCurve PolesCount=3 KnotsCount=2 Degree=2 IsPeriodic=0
    g4: BSplineCurve PolesCount=3 KnotsCount=2 Degree=2 IsPeriodic=0
    g5: BSplineCurve PolesCount=3 KnotsCount=2 Degree=2 IsPeriodic=0
    g6: BSplineCurve PolesCount=3 KnotsCount=2 Degree=2 IsPeriodic=0
    g7: BSplineCurve PolesCount=3 KnotsCount=2 Degree=2 IsPeriodic=0
    g8: BSplineCurve PolesCount=3 KnotsCount=2 Degree=2 IsPeriodic=0
    g9: BSplineCurve PolesCount=3 KnotsCount=2 Degree=2 IsPeriodic=0
    g10: BSplineCurve PolesCount=3 KnotsCount=2 Degree=2 IsPeriodic=0
    g11: BSplineCurve PolesCount=3 KnotsCount=2 Degree=2 IsPeriodic=0
    g12: BSplineCurve PolesCount=3 KnotsCount=2 Degree=2 IsPeriodic=0
    g13: BSplineCurve PolesCount=3 KnotsCount=2 Degree=2 IsPeriodic=0
    g14: BSplineCurve PolesCount=3 KnotsCount=2 Degree=2 IsPeriodic=0
    g15: BSplineCurve PolesCount=3 KnotsCount=2 Degree=2 IsPeriodic=0
    g16: BSplineCurve PolesCount=3 KnotsCount=2 Degree=2 IsPeriodic=0
    g17: BSplineCurve PolesCount=3 KnotsCount=2 Degree=2 IsPeriodic=0
    g18: BSplineCurve PolesCount=3 KnotsCount=2 Degree=2 IsPeriodic=0
    g19: BSplineCurve PolesCount=3 KnotsCount=2 Degree=2 IsPeriodic=0
    g20: BSplineCurve PolesCount=3 KnotsCount=2 Degree=2 IsPeriodic=0
    g21: BSplineCurve PolesCount=3 KnotsCount=2 Degree=2 IsPeriodic=0
    g22: BSplineCurve PolesCount=3 KnotsCount=2 Degree=2 IsPeriodic=0
    g23: BSplineCurve PolesCount=3 KnotsCount=2 Degree=2 IsPeriodic=0
    g24: BSplineCurve PolesCount=3 KnotsCount=2 Degree=2 IsPeriodic=0
    g25: BSplineCurve PolesCount=3 KnotsCount=2 Degree=2 IsPeriodic=0
    g26: BSplineCurve PolesCount=3 KnotsCount=2 Degree=2 IsPeriodic=0
    g27: BSplineCurve PolesCount=3 KnotsCount=2 Degree=2 IsPeriodic=0
    g28: BSplineCurve PolesCount=3 KnotsCount=2 Degree=2 IsPeriodic=0
    g29: BSplineCurve PolesCount=3 KnotsCount=2 Degree=2 IsPeriodic=0
    g30: BSplineCurve PolesCount=3 KnotsCount=2 Degree=2 IsPeriodic=0
    g31: BSplineCurve PolesCount=3 KnotsCount=2 Degree=2 IsPeriodic=0
    g32: BSplineCurve PolesCount=3 KnotsCount=2 Degree=2 IsPeriodic=0
    g33: LineSegment StartX=-0.522777 StartY=16.9213 StartZ=0 EndX=-1.12136 EndY=16.9213 EndZ=0
    g34: LineSegment StartX=-0.522777 StartY=17.3313 StartZ=0 EndX=-0.522777 EndY=16.9213 EndZ=0
    g35: LineSegment StartX=-1.12136 StartY=17.3313 StartZ=0 EndX=-0.522777 EndY=17.3313 EndZ=0
    g36: LineSegment StartX=-1.12136 StartY=20 StartZ=0 EndX=-1.12136 EndY=17.3313 EndZ=0
    g37: LineSegment StartX=-1.59421 StartY=20 StartZ=0 EndX=-1.12136 EndY=20 EndZ=0
    g38: LineSegment StartX=-3.49654 StartY=17.3039 StartZ=0 EndX=-1.59421 EndY=20 EndZ=0
    g39: LineSegment StartX=-3.49654 StartY=16.9213 StartZ=0 EndX=-3.49654 EndY=17.3039 EndZ=0
    g40: LineSegment StartX=-1.56414 StartY=16.9213 StartZ=0 EndX=-3.49654 EndY=16.9213 EndZ=0
    g41: LineSegment StartX=-1.56414 StartY=16 StartZ=0 EndX=-1.56414 EndY=16.9213 EndZ=0
    g42: LineSegment StartX=-1.12136 StartY=16 StartZ=0 EndX=-1.56414 EndY=16 EndZ=0
    g43: LineSegment StartX=-1.12136 StartY=16.9213 StartZ=0 EndX=-1.12136 EndY=16 EndZ=0
    g44: LineSegment StartX=-1.56414 StartY=17.3313 StartZ=0 EndX=-1.56414 EndY=18.6303 EndZ=0
    g45: LineSegment StartX=-3.04555 StartY=17.3313 StartZ=0 EndX=-1.56414 EndY=17.3313 EndZ=0
    g46: LineSegment StartX=-1.81286 StartY=19.0678 StartZ=0 EndX=-3.04555 EndY=17.3313 EndZ=0
    g47: BSplineCurve PolesCount=3 KnotsCount=2 Degree=2 IsPeriodic=0
    g48: BSplineCurve PolesCount=3 KnotsCount=2 Degree=2 IsPeriodic=0
    g49: LineSegment StartX=-1.53681 StartY=19.5135 StartZ=0 EndX=-1.55867 EndY=19.5135 EndZ=0
    g50: BSplineCurve PolesCount=3 KnotsCount=2 Degree=2 IsPeriodic=0
    g51: BSplineCurve PolesCount=3 KnotsCount=2 Degree=2 IsPeriodic=0
    g52: BSplineCurve PolesCount=3 KnotsCount=2 Degree=2 IsPeriodic=0
    g53: BSplineCurve PolesCount=3 KnotsCount=2 Degree=2 IsPeriodic=0
    g54: BSplineCurve PolesCount=3 KnotsCount=2 Degree=2 IsPeriodic=0
    g55: BSplineCurve PolesCount=3 KnotsCount=2 Degree=2 IsPeriodic=0
    g56: BSplineCurve PolesCount=3 KnotsCount=2 Degree=2 IsPeriodic=0
    g57: BSplineCurve PolesCount=3 KnotsCount=2 Degree=2 IsPeriodic=0
    g58: BSplineCurve PolesCount=3 KnotsCount=2 Degree=2 IsPeriodic=0
    g59: LineSegment StartX=0.084184 StartY=19.3342 StartZ=0 EndX=-0.145408 EndY=19.6458 EndZ=0
    g60: BSplineCurve PolesCount=3 KnotsCount=2 Degree=2 IsPeriodic=0
    g61: BSplineCurve PolesCount=3 KnotsCount=2 Degree=2 IsPeriodic=0
    g62: BSplineCurve PolesCount=3 KnotsCount=2 Degree=2 IsPeriodic=0
    g63: BSplineCurve PolesCount=3 KnotsCount=2 Degree=2 IsPeriodic=0
    g64: BSplineCurve PolesCount=3 KnotsCount=2 Degree=2 IsPeriodic=0
    g65: BSplineCurve PolesCount=3 KnotsCount=2 Degree=2 IsPeriodic=0
    g66: BSplineCurve PolesCount=3 KnotsCount=2 Degree=2 IsPeriodic=0
    g67: BSplineCurve PolesCount=3 KnotsCount=2 Degree=2 IsPeriodic=0
    g68: LineSegment StartX=0.439504 StartY=18.254 StartZ=0 EndX=0.84129 EndY=18.254 EndZ=0
    g69: LineSegment StartX=0.439504 StartY=17.8659 StartZ=0 EndX=0.439504 EndY=18.254 EndZ=0
    g70: LineSegment StartX=0.838557 StartY=17.8659 StartZ=0 EndX=0.439504 EndY=17.8659 EndZ=0
    g71: BSplineCurve PolesCount=3 KnotsCount=2 Degree=2 IsPeriodic=0
    g72: BSplineCurve PolesCount=3 KnotsCount=2 Degree=2 IsPeriodic=0
    g73: BSplineCurve PolesCount=3 KnotsCount=2 Degree=2 IsPeriodic=0
    g74: BSplineCurve PolesCount=3 KnotsCount=2 Degree=2 IsPeriodic=0
    g75: BSplineCurve PolesCount=3 KnotsCount=2 Degree=2 IsPeriodic=0
    g76: BSplineCurve PolesCount=3 KnotsCount=2 Degree=2 IsPeriodic=0
    g77: BSplineCurve PolesCount=3 KnotsCount=2 Degree=2 IsPeriodic=0
    g78: LineSegment StartX=-0.170007 StartY=16.1574 StartZ=0 EndX=-0.170007 EndY=16.5838 EndZ=0
    g79: BSplineCurve PolesCount=3 KnotsCount=2 Degree=2 IsPeriodic=0
    g80: BSplineCurve PolesCount=3 KnotsCount=2 Degree=2 IsPeriodic=0
    g81: BSplineCurve PolesCount=3 KnotsCount=2 Degree=2 IsPeriodic=0
    g82: BSplineCurve PolesCount=3 KnotsCount=2 Degree=2 IsPeriodic=0
    g83: BSplineCurve PolesCount=3 KnotsCount=2 Degree=2 IsPeriodic=0
    g84: BSplineCurve PolesCount=3 KnotsCount=2 Degree=2 IsPeriodic=0
    g85: BSplineCurve PolesCount=3 KnotsCount=2 Degree=2 IsPeriodic=0
    g86: LineSegment StartX=1.49453 StartY=18.1009 StartZ=0 EndX=1.49453 EndY=18.0791 EndZ=0
    g87: BSplineCurve PolesCount=3 KnotsCount=2 Degree=2 IsPeriodic=0
    g88: BSplineCurve PolesCount=3 KnotsCount=2 Degree=2 IsPeriodic=0
    g89: BSplineCurve PolesCount=3 KnotsCount=2 Degree=2 IsPeriodic=0
    g90: BSplineCurve PolesCount=3 KnotsCount=2 Degree=2 IsPeriodic=0
    g91: BSplineCurve PolesCount=3 KnotsCount=2 Degree=2 IsPeriodic=0
    g92: BSplineCurve PolesCount=3 KnotsCount=2 Degree=2 IsPeriodic=0
    g93: BSplineCurve PolesCount=3 KnotsCount=2 Degree=2 IsPeriodic=0
    g94: BSplineCurve PolesCount=3 KnotsCount=2 Degree=2 IsPeriodic=0
    g95: BSplineCurve PolesCount=3 KnotsCount=2 Degree=2 IsPeriodic=0
    g96: BSplineCurve PolesCount=3 KnotsCount=2 Degree=2 IsPeriodic=0
    g97: BSplineCurve PolesCount=3 KnotsCount=2 Degree=2 IsPeriodic=0
    g98: BSplineCurve PolesCount=3 KnotsCount=2 Degree=2 IsPeriodic=0
    g99: BSplineCurve PolesCount=3 KnotsCount=2 Degree=2 IsPeriodic=0
    g100: BSplineCurve PolesCount=3 KnotsCount=2 Degree=2 IsPeriodic=0
    g101: BSplineCurve PolesCount=3 KnotsCount=2 Degree=2 IsPeriodic=0
    g102: BSplineCurve PolesCount=3 KnotsCount=2 Degree=2 IsPeriodic=0
    g103: LineSegment StartX=5.21465 StartY=17.9909 StartZ=0 EndX=5.18185 EndY=17.9909 EndZ=0
    g104: BSplineCurve PolesCount=3 KnotsCount=2 Degree=2 IsPeriodic=0
    g105: BSplineCurve PolesCount=3 KnotsCount=2 Degree=2 IsPeriodic=0
    g106: BSplineCurve PolesCount=3 KnotsCount=2 Degree=2 IsPeriodic=0
    g107: BSplineCurve PolesCount=3 KnotsCount=2 Degree=2 IsPeriodic=0
    g108: BSplineCurve PolesCount=3 KnotsCount=2 Degree=2 IsPeriodic=0
    g109: LineSegment StartX=3.33965 StartY=15.9962 StartZ=0 EndX=3.33965 EndY=16.3898 EndZ=0
    g110: BSplineCurve PolesCount=3 KnotsCount=2 Degree=2 IsPeriodic=0
    g111: BSplineCurve PolesCount=3 KnotsCount=2 Degree=2 IsPeriodic=0
    g112: BSplineCurve PolesCount=3 KnotsCount=2 Degree=2 IsPeriodic=0
    g113: BSplineCurve PolesCount=3 KnotsCount=2 Degree=2 IsPeriodic=0
    g114: BSplineCurve PolesCount=3 KnotsCount=2 Degree=2 IsPeriodic=0
    g115: BSplineCurve PolesCount=3 KnotsCount=2 Degree=2 IsPeriodic=0
    g116: BSplineCurve PolesCount=3 KnotsCount=2 Degree=2 IsPeriodic=0
    g117: BSplineCurve PolesCount=3 KnotsCount=2 Degree=2 IsPeriodic=0
    g118: BSplineCurve PolesCount=3 KnotsCount=2 Degree=2 IsPeriodic=0
    g119: BSplineCurve PolesCount=3 KnotsCount=2 Degree=2 IsPeriodic=0
    g120: BSplineCurve PolesCount=3 KnotsCount=2 Degree=2 IsPeriodic=0
    g121: BSplineCurve PolesCount=3 KnotsCount=2 Degree=2 IsPeriodic=0
    g122: BSplineCurve PolesCount=3 KnotsCount=2 Degree=2 IsPeriodic=0
    g123: BSplineCurve PolesCount=3 KnotsCount=2 Degree=2 IsPeriodic=0
    g124: BSplineCurve PolesCount=3 KnotsCount=2 Degree=2 IsPeriodic=0
    g125: BSplineCurve PolesCount=3 KnotsCount=2 Degree=2 IsPeriodic=0
    g126: BSplineCurve PolesCount=3 KnotsCount=2 Degree=2 IsPeriodic=0
    g127: LineSegment StartX=7.9344 StartY=16 StartZ=0 EndX=7.49162 EndY=16 EndZ=0
    g128: LineSegment StartX=7.9344 StartY=20 StartZ=0 EndX=7.9344 EndY=16 EndZ=0
    g129: LineSegment StartX=7.55722 StartY=20 StartZ=0 EndX=7.9344 EndY=20 EndZ=0
    g130: LineSegment StartX=6.47485 StartY=19.166 StartZ=0 EndX=7.55722 EndY=20 EndZ=0
    g131: LineSegment StartX=6.71265 StartY=18.8571 StartZ=0 EndX=6.47485 EndY=19.166 EndZ=0
    g132: LineSegment StartX=7.1691 StartY=19.2236 StartZ=0 EndX=6.71265 EndY=18.8571 EndZ=0
    g133: BSplineCurve PolesCount=3 KnotsCount=2 Degree=2 IsPeriodic=0
    g134: BSplineCurve PolesCount=3 KnotsCount=2 Degree=2 IsPeriodic=0
    g135: BSplineCurve PolesCount=3 KnotsCount=2 Degree=2 IsPeriodic=0
    g136: BSplineCurve PolesCount=3 KnotsCount=2 Degree=2 IsPeriodic=0
    g137: BSplineCurve PolesCount=3 KnotsCount=2 Degree=2 IsPeriodic=0
    g138: LineSegment StartX=7.49162 StartY=16 StartZ=0 EndX=7.49162 EndY=18.8349 EndZ=0
  constraints (163):
    c: Coincident(g0,g1)
    c: Coincident(g1,g2)
    c: Coincident(g2,g3)
    c: Coincident(g3,g4)
    c: Coincident(g4,g5)
    c: Coincident(g5,g6)
    c: Coincident(g6,g7)
    c: Coincident(g7,g8)
    c: Coincident(g8,g9)
    c: Coincident(g9,g10)
    c: Coincident(g10,g11)
    c: Coincident(g11,g12)
    c: Coincident(g12,g0)
    c: Coincident(g13,g14)
    c: Coincident(g14,g15)
    c: Coincident(g15,g16)
    c: Coincident(g16,g17)
    c: Coincident(g17,g18)
    c: Coincident(g18,g19)
    c: Coincident(g19,g20)
    c: Coincident(g20,g21)
    c: Coincident(g21,g22)
    c: Coincident(g22,g23)
    c: Coincident(g23,g24)
    c: Coincident(g24,g13)
    c: Coincident(g25,g26)
    c: Coincident(g26,g27)
    c: Coincident(g27,g28)
    c: Coincident(g28,g29)
    c: Coincident(g29,g30)
    c: Coincident(g30,g31)
    c: Coincident(g31,g32)
    c: Coincident(g32,g25)
    c: Horizontal(g33)
    c: Coincident(g33,g34)
    c: Vertical(g34)
    c: Coincident(g34,g35)
    c: Horizontal(g35)
    c: Coincident(g35,g36)
    c: Vertical(g36)
    c: Coincident(g36,g37)
    c: Horizontal(g37)
    c: Coincident(g37,g38)
    c: Coincident(g38,g39)
    c: Vertical(g39)
    c: Coincident(g39,g40)
    c: Horizontal(g40)
    c: Coincident(g40,g41)
    c: Vertical(g41)
    c: Coincident(g41,g42)
    c: Horizontal(g42)
    c: Coincident(g42,g43)
    c: Vertical(g43)
    c: Coincident(g43,g33)
    c: Vertical(g44)
    c: Coincident(g44,g45)
    c: Horizontal(g45)
    c: Coincident(g45,g46)
    c: Coincident(g46,g47)
    c: Coincident(g47,g48)
    c: Coincident(g48,g49)
    c: Horizontal(g49)
    c: Coincident(g49,g50)
    c: Coincident(g50,g51)
    c: Coincident(g51,g52)
    c: Coincident(g52,g53)
    c: Coincident(g53,g44)
    c: Coincident(g54,g55)
    c: Coincident(g55,g56)
    c: Coincident(g56,g57)
    c: Coincident(g57,g58)
    c: Coincident(g58,g59)
    c: Coincident(g59,g60)
    c: Coincident(g60,g61)
    c: Coincident(g61,g62)
    c: Coincident(g62,g63)
    c: Coincident(g63,g64)
    c: Coincident(g64,g65)
    c: Coincident(g65,g66)
    c: Coincident(g66,g67)
    c: Coincident(g67,g68)
    c: Horizontal(g68)
    c: Coincident(g68,g69)
    c: Vertical(g69)
    c: Coincident(g69,g70)
    c: Horizontal(g70)
    c: Coincident(g70,g71)
    c: Coincident(g71,g72)
    c: Coincident(g72,g73)
    c: Coincident(g73,g74)
    c: Coincident(g74,g75)
    c: Coincident(g75,g76)
    c: Coincident(g76,g77)
    c: Coincident(g77,g78)
    c: Vertical(g78)
    c: Coincident(g78,g79)
    c: Coincident(g79,g80)
    c: Coincident(g80,g81)
    c: Coincident(g81,g82)
    c: Coincident(g82,g83)
    c: Coincident(g83,g84)
    c: Coincident(g84,g85)
    c: Coincident(g85,g86)
    c: Vertical(g86)
    c: Coincident(g86,g87)
    c: Coincident(g87,g88)
    c: Coincident(g88,g54)
    c: Coincident(g89,g90)
    c: Coincident(g90,g91)
    c: Coincident(g91,g92)
    c: Coincident(g92,g93)
    c: Coincident(g93,g94)
    c: Coincident(g94,g95)
    c: Coincident(g95,g96)
    c: Coincident(g96,g97)
    c: Coincident(g97,g98)
    c: Coincident(g98,g99)
    c: Coincident(g99,g100)
    c: Coincident(g100,g101)
    c: Coincident(g101,g102)
    c: Coincident(g102,g103)
    c: Horizontal(g103)
    c: Coincident(g103,g104)
    c: Coincident(g104,g105)
    c: Coincident(g105,g106)
    c: Coincident(g106,g107)
    c: Coincident(g107,g108)
    c: Coincident(g108,g109)
    c: Vertical(g109)
    c: Coincident(g109,g110)
    c: Coincident(g110,g111)
    c: Coincident(g111,g112)
    c: Coincident(g112,g113)
    c: Coincident(g113,g114)
    c: Coincident(g114,g115)
    c: Coincident(g115,g89)
    c: Coincident(g116,g117)
    c: Coincident(g117,g118)
    c: Coincident(g118,g119)
    c: Coincident(g119,g120)
    c: Coincident(g120,g121)
    c: Coincident(g121,g122)
    c: Coincident(g122,g123)
    c: Coincident(g123,g124)
    c: Coincident(g124,g125)
    c: Coincident(g125,g126)
    c: Coincident(g126,g116)
    c: Horizontal(g127)
    c: Coincident(g127,g128)
    c: Vertical(g128)
    c: Coincident(g128,g129)
    c: Horizontal(g129)
    c: Coincident(g129,g130)
    c: Coincident(g130,g131)
    c: Coincident(g131,g132)
    c: Coincident(g132,g133)
    c: Coincident(g133,g134)
    c: Coincident(g134,g135)
    c: Coincident(g135,g136)
    c: Coincident(g136,g137)
    c: Coincident(g137,g138)
    c: Vertical(g138)
    c: Coincident(g138,g127)
FEATURE [PartDesign::Pocket] Pocket032
  BaseFeature = -> PolarPattern008
  Direction = (0,1,-2e-16)
  Length = 5
  Length2 = 5
  Placement = pos=(0,0,0) rot=(1,0,0;1.5708rad)
  Profile = -> Sketch052
  ReferenceAxis = -> Sketch052 [N_Axis]
  Refine = true
  Suppressed = false
  Type = 0
FEATURE [PartDesign::Body] Body008  label="Gear_0_4391"
  AllowCompound = false
  Group = -> [Sketch051,USE_Macro_v6_gear_profile009,Pad008,Pocket031,PolarPattern008,ShapeString007,Sketch052,Pocket032]
  Origin = -> Origin008
  Placement = pos=(0,-3,96) rot=(1,0,0;1.5708rad)
  Tip = -> Pocket032
